FCSTD DOCUMENT  (FreeCAD 0.20R29410 (Git))
Label: trafficModuleV3
License: All rights reserved
LicenseURL: http://en.wikipedia.org/wiki/All_rights_reserved
objects: Part::Feature×121, Sketcher::SketchObject×63, Part::Extrusion×29, Part::Cylinder×26, Part::MultiFuse×25, Part::MultiCommon×20, Part::Loft×17, App::Part×13, Part::Cut×12, Part::Box×7, Part::Cone×1, Part::Compound×1
note: 322 computed .brp shape members not serialized (recipe doc carries the construction recipe); baked Part::Feature solids carry a one-line shape summary decoded from their .brp

FEATURE [Sketcher::SketchObject] Sketch014
  FullyConstrained = true
  sketch-geometry (4):
    g0: LineSegment StartX=0 StartY=275 StartZ=0 EndX=275 EndY=275 EndZ=0
    g1: LineSegment StartX=275 StartY=275 StartZ=0 EndX=275 EndY=0 EndZ=0
    g2: LineSegment StartX=275 StartY=0 StartZ=0 EndX=0 EndY=0 EndZ=0
    g3: LineSegment StartX=0 StartY=0 StartZ=0 EndX=0 EndY=275 EndZ=0
  constraints (11):
    c: Coincident(g0,g1)
    c: Coincident(g1,g2)
    c: Coincident(g2,g3)
    c: Coincident(g3,g0)
    c: Horizontal(g0)
    c: Horizontal(g2)
    c: Vertical(g1)
    c: Vertical(g3)
    c: Coincident(g2,g-1)
    c: DistanceX(g2,g2) = 275
    c: DistanceY(g3,g3) = 275
FEATURE [Sketcher::SketchObject] Sketch015
  FullyConstrained = true
  Placement = pos=(0,0,175.1) rot=(0,0,1;0rad)
  sketch-geometry (5):
    g0: GeomPoint X=137.5 Y=137.5 Z=0
    g1: LineSegment StartX=137.55 StartY=137.55 StartZ=0 EndX=137.55 EndY=137.45 EndZ=0
    g2: LineSegment StartX=137.55 StartY=137.45 StartZ=0 EndX=137.45 EndY=137.45 EndZ=0
    g3: LineSegment StartX=137.45 StartY=137.45 StartZ=0 EndX=137.45 EndY=137.55 EndZ=0
    g4: LineSegment StartX=137.45 StartY=137.55 StartZ=0 EndX=137.55 EndY=137.55 EndZ=0
  constraints (14):
    c: Coincident(g1,g2)
    c: Horizontal(g2)
    c: Vertical(g1)
    c: DistanceX(g2,g2) = 0.1
    c: DistanceX(g2,g0) = 0.05
    c: DistanceY(g1,g1) = 0.1
    c: DistanceY(g1,g0) = -0.05
    c: DistanceX(g0) = 137.5
    c: DistanceY(g0) = 137.5
    c: Coincident(g3,g2)
    c: Vertical(g3)
    c: Coincident(g4,g3)
    c: Coincident(g4,g1)
    c: Horizontal(g4)
FEATURE [Part::Loft] Loft  label="outerLayer"
  Closed = false
  MaxDegree = 5
  Ruled = false
  Sections = -> [Sketch014,Sketch015]
  Solid = true
FEATURE [Part::Feature] Part__Feature025  label="CUI_VGS-35C-12"
  Placement = pos=(86,137.5,21.5) rot=(1,0,0;1.5708rad)
  shape: bbox 82.03 x 100 x 30.06 mm, 2215 faces, 10 solids (baked)
FEATURE [Part::Cylinder] Cylinder004 .. Cylinder009  x6 (patterned run collapsed; names and placements below)
  Angle = 360
  AttacherType = Attacher::AttachEngine3D
  FirstAngle = 0
  Height = 10
  Radius = 2
  SecondAngle = 0
FEATURE [Part::Cylinder] Cylinder010  label="Cylinder"
  Angle = 360
  AttacherType = Attacher::AttachEngine3D
  FirstAngle = 0
  Height = 10
  Radius = 2
  SecondAngle = 0
FEATURE [Part::Cylinder] Cylinder011 .. Cylinder018  x8 (patterned run collapsed; names and placements below)
  Angle = 360
  AttacherType = Attacher::AttachEngine3D
  FirstAngle = 0
  Height = 10
  Radius = 2
  SecondAngle = 0
FEATURE [Part::Feature] Part__Feature  label="MainBoard"
  shape: bbox 50 x 23 x 1.8 mm, 90 faces (baked)
FEATURE [Part::Feature] Part__Feature029  label="USB Type C Port (SMD Type)"
  Placement = pos=(-18.7,0.12,3.4) rot=(0.707107,-0.707107,0;3.14159rad)
  shape: bbox 7.901 x 8.941 x 4.201 mm, 394 faces, 24 solids (baked)
FEATURE [Part::Feature] Part__Feature030  label="LoRaSTM32Chip"
  Placement = pos=(8.97,0,1.8) rot=(0,0,1;0rad)
  shape: bbox 12 x 12 x 2.5 mm, 68 faces (baked)
FEATURE [Part::Feature] Part__Feature031  label="E10_433M_SMA122"
  Placement = pos=(13,-2.15,1.4) rot=(0,0,1;0rad)
  shape: bbox 11.33 x 1.55 x 1.55 mm, 34 faces (baked)
FEATURE [Part::Feature] Part__Feature032  label="E10_433M_SMA123"
  Placement = pos=(13,-2.15,1.4) rot=(0,0,1;0rad)
  shape: bbox 13.33 x 6.493 x 6.493 mm, 59 faces (baked)
FEATURE [Part::Feature] Part__Feature033  label="CP2012"
  Placement = pos=(-8.75,0.13,1.82) rot=(0,0,1;0rad)
  shape: bbox 4 x 4 x 0.7 mm, 6 faces (baked)
FEATURE [Part::Feature] Part__Feature034  label="u.Fl Antenna Connector - 523-A-1JB"
  Placement = pos=(24.2,5.8,1.8) rot=(0,0.707107,0.707107;3.14159rad)
  shape: bbox 3.1 x 3 x 1.25 mm, 82 faces, 5 solids (baked)
FEATURE [Part::Feature] Part__Feature035  label="Top Traces"
  shape: bbox 49.4 x 23 x 0.02 mm, 7906 faces, 207 solids (baked)
FEATURE [App::Part] LoRa_E5_Mini  label="LoRa-E5-Mini"
  Group = -> [Part__Feature,Part__Feature029,Part__Feature030,Part__Feature031,Part__Feature032,Part__Feature033,Part__Feature034,Part__Feature035,Cylinder004,Cylinder005,Cylinder006,Cylinder007,Cylinder008,Cylinder009,Cylinder010,Cylinder011,Cylinder012,Cylinder013,Cylinder014,Cylinder015,Cylinder016,Cylinder017,Cylinder018]
  Origin = -> Origin
  Placement = pos=(100,164,45) rot=(0,0,-1;4.71239rad)
FEATURE [Part::Feature] Part__Feature037  label="ips7100s"
  Placement = pos=(161.5,115,75) rot=(0,0,1;0rad)
  shape: bbox 48.08 x 13.98 x 44.07 mm, 1935 faces (baked)
FEATURE [Part::Feature] Part__Feature007  label="Heat Sink"
  shape: bbox 100 x 91 x 19 mm, 161 faces (baked)
FEATURE [Part::Feature] Part__Feature008  label="Battery Holder"
  shape: bbox 28.5 x 16 x 6 mm, 91 faces (baked)
FEATURE [Part::Feature] Part__Feature009  label="DC Jack"
  shape: bbox 7.6 x 11.5 x 9.75 mm, 10 faces (baked)
FEATURE [Part::Feature] Part__Feature010  label="PCB"
  shape: bbox 90 x 90 x 3.3 mm, 59 faces (baked)
FEATURE [Part::Feature] Part__Feature011  label="HDMI"
  shape: bbox 14.51 x 11.61 x 5.506 mm, 31 faces (baked)
FEATURE [Part::Feature] Part__Feature012  label="Ethernet"
  shape: bbox 15.9 x 21.4 x 13.5 mm, 25 faces (baked)
FEATURE [Part::Feature] Part__Feature013  label="USB 3.0 B"
  shape: bbox 14.55 x 17.5 x 16.15 mm, 36 faces (baked)
FEATURE [Part::Feature] Part__Feature014  label="USB 3.0 A"
  shape: bbox 14.55 x 17.5 x 16.15 mm, 36 faces (baked)
FEATURE [Part::Feature] Part__Feature015  label="Audio Jack"
  shape: bbox 6.5 x 14 x 4 mm, 10 faces (baked)
FEATURE [Part::Feature] Part__Feature016  label="Fan Plug"
  shape: bbox 3.75 x 7.5 x 4.75 mm, 32 faces (baked)
FEATURE [Part::Feature] Part__Feature017  label="REMOCON"
  shape: bbox 7.006 x 5.006 x 12.01 mm, 30 faces (baked)
FEATURE [Part::Feature] Part__Feature018  label="eMMC"
  shape: bbox 13.5 x 18.5 x 2.8 mm, 33 faces (baked)
FEATURE [Part::Feature] Part__Feature019  label="MicroUSB"
  shape: bbox 7.012 x 4.616 x 3.511 mm, 31 faces (baked)
FEATURE [Part::Feature] Part__Feature020  label="Switch"
  shape: bbox 9 x 5.74 x 3.5 mm, 11 faces (baked)
FEATURE [Part::Feature] Part__Feature021  label="MicroSD Card Socket"
  shape: bbox 11.5 x 5.5 x 3.5 mm, 11 faces (baked)
FEATURE [Part::Feature] Part__Feature022  label="7 Pin Header"
  shape: bbox 17.5 x 2.5 x 8 mm, 41 faces (baked)
FEATURE [Part::Feature] Part__Feature023  label="UART"
  shape: bbox 5 x 12.5 x 6 mm, 43 faces (baked)
FEATURE [Part::Feature] Part__Feature024  label="40 Pin Header"
  shape: bbox 5 x 50 x 8 mm, 206 faces (baked)
FEATURE [App::Part] Odroid_N2__v4  label="Odroid-N2+ v4"
  Group = -> [Part__Feature007,Part__Feature008,Part__Feature009,Part__Feature010,Part__Feature011,Part__Feature012,Part__Feature013,Part__Feature014,Part__Feature015,Part__Feature016,Part__Feature017,Part__Feature018,Part__Feature019,Part__Feature020,Part__Feature021,Part__Feature022,Part__Feature023,Part__Feature024]
  Origin = -> Origin002
  Placement = pos=(164,-676,-21.5) rot=(0,0,1;0rad)
FEATURE [Part::Cone] Cone
  Angle = 360
  AttacherType = Attacher::AttachEngine3D
  Height = 1.5
  Placement = pos=(0,0,25.5) rot=(0,0,1;0rad)
  Radius1 = 4
  Radius2 = 3.5
FEATURE [Part::Cylinder] Cylinder020
  Angle = 360
  AttacherType = Attacher::AttachEngine3D
  FirstAngle = 0
  Height = 22
  Placement = pos=(0,0,5) rot=(0,0,1;0rad)
  Radius = 3.2
  SecondAngle = 0
FEATURE [Part::Cylinder] Cylinder021
  Angle = 360
  AttacherType = Attacher::AttachEngine3D
  FirstAngle = 0
  Height = 2
  Placement = pos=(0,0,5) rot=(0,0,1;0rad)
  Radius = 3.55
  SecondAngle = 0
FEATURE [Part::Cylinder] Cylinder022
  Angle = 360
  AttacherType = Attacher::AttachEngine3D
  FirstAngle = 0
  Height = 1
  Placement = pos=(0,0,11) rot=(0,0,1;0rad)
  Radius = 3.55
  SecondAngle = 0
FEATURE [Part::Cylinder] Cylinder023
  Angle = 360
  AttacherType = Attacher::AttachEngine3D
  FirstAngle = 0
  Height = 8
  Placement = pos=(0,0,12) rot=(0,0,1;0rad)
  Radius = 3.25
  SecondAngle = 0
FEATURE [Part::Cylinder] Cylinder024
  Angle = 360
  AttacherType = Attacher::AttachEngine3D
  FirstAngle = 0
  Height = 5.5
  Placement = pos=(0,0,20) rot=(0,0,1;0rad)
  Radius = 4
  SecondAngle = 0
FEATURE [Part::Cylinder] Cylinder025
  Angle = 360
  AttacherType = Attacher::AttachEngine3D
  FirstAngle = 0
  Height = 2
  Placement = pos=(0,0,3) rot=(0,0,1;0rad)
  Radius = 1
  SecondAngle = 0
FEATURE [Part::MultiFuse] Fusion002
  Shapes = -> [Cone,Cylinder020,Cylinder021,Cylinder022,Cylinder023,Cylinder024]
FEATURE [Part::MultiFuse] Fusion055  label="mic"
  Placement = pos=(137.5,137.5,108.25) rot=(0,0,1;3.14159rad)
  Shapes = -> [Cylinder025,Fusion002]
FEATURE [Part::Feature] Part__Feature040  label="CeramicBody (1)"
  shape: bbox 1.8 x 1.23 x 1.23 mm, 10 faces (baked)
FEATURE [Part::Feature] Part__Feature126  label="scd30"
  Placement = pos=(137.5,170,95) rot=(1,0,0;3.14159rad)
  shape: bbox 35.11 x 7.027 x 23.02 mm, 2292 faces, 25 solids (baked)
FEATURE [Part::Feature] Part__Feature127  label="Board"
  shape: bbox 25.4 x 25.4 x 1.57 mm, 211 faces (baked)
FEATURE [Part::Feature] Part__Feature128  label="QFN24_4MM"
  Placement = pos=(12.1412,14.4526,1.57) rot=(0,0,1;3.92699rad)
  shape: bbox 5.657 x 5.657 x 0.9 mm, 172 faces (baked)
FEATURE [Part::Feature] Part__Feature129  label="Part 5"
  shape: bbox 0.48 x 0.6603 x 0.6 mm, 14 faces (baked)
FEATURE [Part::Feature] Part__Feature130  label="Part 6"
  shape: bbox 0.48 x 0.6603 x 0.6 mm, 14 faces (baked)
FEATURE [Part::Feature] Part__Feature131  label="Part 4"
  shape: bbox 0.48 x 0.6603 x 0.6 mm, 14 faces (baked)
FEATURE [Part::Feature] Part__Feature132  label="Part 3"
  shape: bbox 0.48 x 0.6603 x 0.6 mm, 14 faces (baked)
FEATURE [Part::Feature] Part__Feature133  label="Part 010"
  shape: bbox 0.48 x 0.6603 x 0.6 mm, 14 faces (baked)
FEATURE [Part::Feature] Part__Feature134  label="Part 011"
  shape: bbox 3 x 1.4 x 1 mm, 10 faces (baked)
FEATURE [Part::Feature] Part__Feature135  label="Pin1"
  shape: bbox 0.6224 x 1.252 x 1.252 mm, 37 faces (baked)
FEATURE [Part::Feature] Part__Feature136  label="Pin2"
  shape: bbox 0.6224 x 1.252 x 1.252 mm, 37 faces (baked)
FEATURE [Part::Feature] Part__Feature137  label="CeramicBody"
  shape: bbox 1.8 x 1.23 x 1.23 mm, 10 faces (baked)
FEATURE [Part::Feature] Part__Feature138  label="0603-NO (1)"
  Placement = pos=(23.241,6.223,1.57) rot=(0,0,1;0rad)
  shape: bbox 1.7 x 0.9 x 0.55 mm, 52 faces, 3 solids (baked)
FEATURE [Part::Feature] Part__Feature139  label="0603-NO (2)"
  Placement = pos=(13.3858,8.4328,1.57) rot=(0,0,1;0rad)
  shape: bbox 1.7 x 0.9 x 0.55 mm, 52 faces, 3 solids (baked)
FEATURE [Part::Feature] Part__Feature140  label="0603-NO (3)"
  Placement = pos=(1.905,18.923,1.57) rot=(0,0,1;3.14159rad)
  shape: bbox 1.7 x 0.9 x 0.55 mm, 52 faces, 3 solids (baked)
FEATURE [Part::Feature] Part__Feature141  label="Pin1 (1)"
  shape: bbox 0.6224 x 1.252 x 1.252 mm, 37 faces (baked)
FEATURE [Part::Feature] Part__Feature142  label="Pin2 (1)"
  shape: bbox 0.6224 x 1.252 x 1.252 mm, 37 faces (baked)
FEATURE [Part::Feature] Part__Feature143  label="Pin1 (2)"
  shape: bbox 0.6224 x 1.252 x 1.252 mm, 37 faces (baked)
FEATURE [Part::Feature] Part__Feature144  label="Pin2 (2)"
  shape: bbox 0.6224 x 1.252 x 1.252 mm, 37 faces (baked)
FEATURE [Part::Feature] Part__Feature145  label="CeramicBody (2)"
  shape: bbox 1.8 x 1.23 x 1.23 mm, 10 faces (baked)
FEATURE [Part::Feature] Part__Feature146  label="CHIPLED_0603_NOOUTLINE"
  Placement = pos=(23.368,8.509,1.57) rot=(0,0,1;1.5708rad)
  shape: bbox 1.616 x 0.8 x 0.4 mm, 133 faces (baked)
FEATURE [Part::Feature] Part__Feature147  label="CHIPLED_0603_NOOUTLINE (1)"
  Placement = pos=(1.905,16.764,1.57) rot=(0,0,-1;1.5708rad)
  shape: bbox 1.616 x 0.8 x 0.4 mm, 133 faces (baked)
FEATURE [Part::Feature] Part__Feature148  label="JST_SH4"
  Placement = pos=(22.86,12.7,1.57) rot=(0,0,1;1.5708rad)
  shape: bbox 4.95 x 6 x 2.96 mm, 229 faces, 7 solids (baked)
FEATURE [Part::Feature] Part__Feature149  label="JST_SH4 (1)"
  Placement = pos=(2.54,12.7,1.57) rot=(0,0,-1;1.5708rad)
  shape: bbox 4.95 x 6 x 2.96 mm, 229 faces, 7 solids (baked)
FEATURE [Part::Feature] Part__Feature150  label="NEO3535_REVERSE"
  Placement = pos=(12.7,23.114,0) rot=(0,1,0;3.14159rad)
  shape: bbox 5.88 x 2.8 x 1.78 mm, 41 faces, 5 solids (baked)
FEATURE [Part::Feature] Part__Feature151  label="RESPACK_4X0603"
  Placement = pos=(22.86,18.415,1.57) rot=(0,0,1;3.14159rad)
  shape: bbox 3.2 x 1.6 x 0.61 mm, 172 faces (baked)
FEATURE [Part::Feature] Part__Feature152  label="SOT363"
  Placement = pos=(17.399,12.192,1.57) rot=(0,0,-1;1.5708rad)
  shape: bbox 2.208 x 2.208 x 1.121 mm, 178 faces, 4 solids (baked)
FEATURE [Part::Feature] Part__Feature153  label="Printed Circuit Board001"
  shape: bbox 25.4 x 17.78 x 1.6 mm, 42 faces (baked)
FEATURE [Part::Feature] Part__Feature154  label="EAHC2835WD007"
  shape: bbox 3.513 x 2.813 x 0.7485 mm, 108 faces, 4 solids (baked)
FEATURE [Part::Feature] Part__Feature155  label="AS7341 v003"
  Placement = pos=(0,-0.339822,1.6) rot=(0,0,1;0rad)
  shape: bbox 2 x 3.1 x 1.1 mm, 267 faces, 26 solids (baked)
FEATURE [Part::Feature] Part__Feature156  label="CAPC-0805-T0.95-BN v004"
  Placement = pos=(-5.01759,-3.15294,1.6) rot=(0,0,1;0rad)
  shape: bbox 2.1 x 1.35 x 0.95 mm, 42 faces (baked)
FEATURE [Part::Feature] Part__Feature157  label="CAPC-0805-T0.95-BN v005"
  Placement = pos=(-5.48627,2.66154,1.6) rot=(0,0,-1;1.5708rad)
  shape: bbox 1.35 x 2.1 x 0.95 mm, 42 faces (baked)
FEATURE [Part::Feature] Part__Feature158  label="CAPC-0805-T0.95-BN v006"
  Placement = pos=(-3.43627,2.66154,1.6) rot=(0,0,-1;1.5708rad)
  shape: bbox 1.35 x 2.1 x 0.95 mm, 42 faces (baked)
FEATURE [Part::Feature] Part__Feature159  label="CAPC-0603-T0.9-BN v002"
  Placement = pos=(-1.69987,-3.28475,1.6) rot=(0,0,1;0rad)
  shape: bbox 1.7 x 0.9 x 0.9 mm, 42 faces (baked)
FEATURE [Part::Feature] Part__Feature160  label="BODY_MF06A001"
  Placement = pos=(0,0,0.762) rot=(0.57735,-0.57735,-0.57735;2.0944rad)
  shape: bbox 1.601 x 2.921 x 1.016 mm, 42 faces (baked)
FEATURE [Part::Feature] Part__Feature161  label="LEAD_MF06A006"
  Placement = pos=(-0.9652,-0.9525,0.1016) rot=(0.57735,-0.57735,-0.57735;2.0944rad)
  shape: bbox 0.6223 x 0.3749 x 0.8636 mm, 14 faces (baked)
FEATURE [Part::Feature] Part__Feature162  label="LEAD_MF06A007"
  Placement = pos=(-0.9652,0,0.1016) rot=(0.57735,-0.57735,-0.57735;2.0944rad)
  shape: bbox 0.6223 x 0.3749 x 0.8636 mm, 14 faces (baked)
FEATURE [Part::Feature] Part__Feature163  label="LEAD_MF06A008"
  Placement = pos=(-0.9652,0.9525,0.1016) rot=(0.57735,-0.57735,-0.57735;2.0944rad)
  shape: bbox 0.6223 x 0.3749 x 0.8636 mm, 14 faces (baked)
FEATURE [Part::Feature] Part__Feature164  label="LEAD_MF06A009"
  Placement = pos=(0.9652,-0.9525,0.1016) rot=(0.57735,0.57735,0.57735;2.0944rad)
  shape: bbox 0.6223 x 0.3749 x 0.8636 mm, 14 faces (baked)
FEATURE [Part::Feature] Part__Feature165  label="LEAD_MF06A010"
  Placement = pos=(0.9652,0,0.1016) rot=(0.57735,0.57735,0.57735;2.0944rad)
  shape: bbox 0.6223 x 0.3749 x 0.8636 mm, 14 faces (baked)
FEATURE [Part::Feature] Part__Feature166  label="LEAD_MF06A011"
  Placement = pos=(0.9652,0.9525,0.1016) rot=(0.57735,0.57735,0.57735;2.0944rad)
  shape: bbox 0.6223 x 0.3749 x 0.8636 mm, 14 faces (baked)
FEATURE [Part::Feature] Part__Feature167  label="SOT363 v003"
  Placement = pos=(4.97054,-0.645171,1.675) rot=(0,0,1;3.14159rad)
  shape: bbox 2.1 x 2 x 1.1 mm, 94 faces, 7 solids (baked)
FEATURE [Part::Feature] Part__Feature168  label="LED 0603 single color v002"
  Placement = pos=(-9.18406,3.72778,1.60762) rot=(0,0,1;1.5708rad)
  shape: bbox 1.961 x 0.7932 x 0.7145 mm, 63 faces, 5 solids (baked)
FEATURE [Part::Feature] Part__Feature169  label="RESC-0603 v003"
  Placement = pos=(4.83432,-3.67461,1.6) rot=(0,0,1;0rad)
  shape: bbox 1.7 x 0.9 x 0.55 mm, 52 faces, 3 solids (baked)
FEATURE [Part::Feature] Part__Feature170  label="RESC-0603 v004"
  Placement = pos=(-7.14949,3.61248,1.6) rot=(0,0,-1;1.5708rad)
  shape: bbox 0.9 x 1.7 x 0.55 mm, 52 faces, 3 solids (baked)
FEATURE [Part::Feature] Part__Feature171  label="YC164_RESPACK v002"
  Placement = pos=(2.99591,1.52916,1.6) rot=(0,0,1;0rad)
  shape: bbox 3.2 x 1.6 x 0.61 mm, 172 faces (baked)
FEATURE [Part::Feature] Part__Feature172  label="qwicc v004"
  Placement = pos=(-10.8364,0.0607456,1.65) rot=(0,0,-1;1.5708rad)
  shape: bbox 4.95 x 6 x 2.96 mm, 229 faces, 7 solids (baked)
FEATURE [Part::Feature] Part__Feature173  label="qwicc v005"
  Placement = pos=(10.8256,0.00556102,1.65) rot=(0,0,1;1.5708rad)
  shape: bbox 4.95 x 6 x 2.96 mm, 229 faces, 7 solids (baked)
FEATURE [App::Part] _603_NO  label="0603-NO"
  Group = -> [Part__Feature135,Part__Feature136,Part__Feature137]
  Origin = -> Origin012
  Placement = pos=(16.51,8.382,1.57) rot=(0,0,1;0rad)
FEATURE [App::Part] _6700497  label="36700497"
  Group = -> [Part__Feature129,Part__Feature130,Part__Feature131,Part__Feature132,Part__Feature133,Part__Feature134]
  Origin = -> Origin010
  Placement = pos=(0,0,0) rot=(0,0,1;3.14159rad)
FEATURE [App::Part] SOT23_5  label="SOT23-5"
  Group = -> [_6700497]
  Origin = -> Origin011
  Placement = pos=(2.54,6.985,1.57) rot=(0,0,1;3.14159rad)
FEATURE [App::Part] _805_NO  label="0805-NO"
  Group = -> [Part__Feature141,Part__Feature142,Part__Feature040]
  Origin = -> Origin013
  Placement = pos=(7.874,13.589,1.57) rot=(0,0,1;1.5708rad)
FEATURE [App::Part] _805_NO__1_  label="0805-NO (1)"
  Group = -> [Part__Feature143,Part__Feature144,Part__Feature145]
  Origin = -> Origin014
  Placement = pos=(12.827,6.223,1.57) rot=(0,0,1;3.14159rad)
FEATURE [App::Part] Packages
  Group = -> [Part__Feature128,SOT23_5,_603_NO,Part__Feature138,Part__Feature139,Part__Feature140,_805_NO,_805_NO__1_,Part__Feature146,Part__Feature147,Part__Feature148,Part__Feature149,Part__Feature150,Part__Feature151,Part__Feature152]
  Origin = -> Origin015
FEATURE [App::Part] Adafruit_I2C_QT_Rotary_Encoder_v2  label="gps"
  Group = -> [Part__Feature127,Packages]
  Origin = -> Origin016
  Placement = pos=(167.5,167.5,74) rot=(0,0,1;0rad)
FEATURE [App::Part] sot_23_6_v003  label="sot-23-6 v003"
  Group = -> [Part__Feature160,Part__Feature161,Part__Feature162,Part__Feature163,Part__Feature164,Part__Feature165,Part__Feature166]
  Origin = -> Origin017
  Placement = pos=(-4.47945,-0.603742,1.69152) rot=(0,0,1;0rad)
FEATURE [App::Part] Adafruit_AS7341_STEMMA_QT_v003  label="bme280"
  Group = -> [Part__Feature153,Part__Feature154,Part__Feature155,Part__Feature156,Part__Feature157,Part__Feature158,Part__Feature159,sot_23_6_v003,Part__Feature167,Part__Feature168,Part__Feature169,Part__Feature170,Part__Feature171,Part__Feature172,Part__Feature173]
  Origin = -> Origin018
  Placement = pos=(170.5,137.5,95) rot=(-0.707107,0,-0.707107;3.14159rad)
FEATURE [Part::Feature] Part__Feature174  label="Printed Circuit Board002"
  shape: bbox 25.4 x 17.78 x 1.6 mm, 42 faces (baked)
FEATURE [Part::Feature] Part__Feature175  label="EAHC2835WD008"
  shape: bbox 3.513 x 2.813 x 0.7485 mm, 108 faces, 4 solids (baked)
FEATURE [Part::Feature] Part__Feature176  label="AS7341 v004"
  Placement = pos=(0,-0.339822,1.6) rot=(0,0,1;0rad)
  shape: bbox 2 x 3.1 x 1.1 mm, 267 faces, 26 solids (baked)
FEATURE [Part::Feature] Part__Feature177  label="CAPC-0805-T0.95-BN v007"
  Placement = pos=(-5.01759,-3.15294,1.6) rot=(0,0,1;0rad)
  shape: bbox 2.1 x 1.35 x 0.95 mm, 42 faces (baked)
FEATURE [Part::Feature] Part__Feature178  label="CAPC-0805-T0.95-BN v008"
  Placement = pos=(-5.48627,2.66154,1.6) rot=(0,0,-1;1.5708rad)
  shape: bbox 1.35 x 2.1 x 0.95 mm, 42 faces (baked)
FEATURE [Part::Feature] Part__Feature179  label="CAPC-0805-T0.95-BN v009"
  Placement = pos=(-3.43627,2.66154,1.6) rot=(0,0,-1;1.5708rad)
  shape: bbox 1.35 x 2.1 x 0.95 mm, 42 faces (baked)
FEATURE [Part::Feature] Part__Feature180  label="CAPC-0603-T0.9-BN v003"
  Placement = pos=(-1.69987,-3.28475,1.6) rot=(0,0,1;0rad)
  shape: bbox 1.7 x 0.9 x 0.9 mm, 42 faces (baked)
FEATURE [Part::Feature] Part__Feature181  label="BODY_MF06A002"
  Placement = pos=(0,0,0.762) rot=(0.57735,-0.57735,-0.57735;2.0944rad)
  shape: bbox 1.601 x 2.921 x 1.016 mm, 42 faces (baked)
FEATURE [Part::Feature] Part__Feature182  label="LEAD_MF06A012"
  Placement = pos=(-0.9652,-0.9525,0.1016) rot=(0.57735,-0.57735,-0.57735;2.0944rad)
  shape: bbox 0.6223 x 0.3749 x 0.8636 mm, 14 faces (baked)
FEATURE [Part::Feature] Part__Feature183  label="LEAD_MF06A013"
  Placement = pos=(-0.9652,0,0.1016) rot=(0.57735,-0.57735,-0.57735;2.0944rad)
  shape: bbox 0.6223 x 0.3749 x 0.8636 mm, 14 faces (baked)
FEATURE [Part::Feature] Part__Feature184  label="LEAD_MF06A014"
  Placement = pos=(-0.9652,0.9525,0.1016) rot=(0.57735,-0.57735,-0.57735;2.0944rad)
  shape: bbox 0.6223 x 0.3749 x 0.8636 mm, 14 faces (baked)
FEATURE [Part::Feature] Part__Feature185  label="LEAD_MF06A015"
  Placement = pos=(0.9652,-0.9525,0.1016) rot=(0.57735,0.57735,0.57735;2.0944rad)
  shape: bbox 0.6223 x 0.3749 x 0.8636 mm, 14 faces (baked)
FEATURE [Part::Feature] Part__Feature186  label="LEAD_MF06A016"
  Placement = pos=(0.9652,0,0.1016) rot=(0.57735,0.57735,0.57735;2.0944rad)
  shape: bbox 0.6223 x 0.3749 x 0.8636 mm, 14 faces (baked)
FEATURE [Part::Feature] Part__Feature187  label="LEAD_MF06A017"
  Placement = pos=(0.9652,0.9525,0.1016) rot=(0.57735,0.57735,0.57735;2.0944rad)
  shape: bbox 0.6223 x 0.3749 x 0.8636 mm, 14 faces (baked)
FEATURE [Part::Feature] Part__Feature188  label="SOT363 v004"
  Placement = pos=(4.97054,-0.645171,1.675) rot=(0,0,1;3.14159rad)
  shape: bbox 2.1 x 2 x 1.1 mm, 94 faces, 7 solids (baked)
FEATURE [Part::Feature] Part__Feature189  label="LED 0603 single color v003"
  Placement = pos=(-9.18406,3.72778,1.60762) rot=(0,0,1;1.5708rad)
  shape: bbox 1.961 x 0.7932 x 0.7145 mm, 63 faces, 5 solids (baked)
FEATURE [Part::Feature] Part__Feature190  label="RESC-0603 v005"
  Placement = pos=(4.83432,-3.67461,1.6) rot=(0,0,1;0rad)
  shape: bbox 1.7 x 0.9 x 0.55 mm, 52 faces, 3 solids (baked)
FEATURE [Part::Feature] Part__Feature191  label="RESC-0603 v006"
  Placement = pos=(-7.14949,3.61248,1.6) rot=(0,0,-1;1.5708rad)
  shape: bbox 0.9 x 1.7 x 0.55 mm, 52 faces, 3 solids (baked)
FEATURE [Part::Feature] Part__Feature192  label="YC164_RESPACK v003"
  Placement = pos=(2.99591,1.52916,1.6) rot=(0,0,1;0rad)
  shape: bbox 3.2 x 1.6 x 0.61 mm, 172 faces (baked)
FEATURE [Part::Feature] Part__Feature193  label="qwicc v006"
  Placement = pos=(-10.8364,0.0607456,1.65) rot=(0,0,-1;1.5708rad)
  shape: bbox 4.95 x 6 x 2.96 mm, 229 faces, 7 solids (baked)
FEATURE [Part::Feature] Part__Feature194  label="qwicc v007"
  Placement = pos=(10.8256,0.00556102,1.65) rot=(0,0,1;1.5708rad)
  shape: bbox 4.95 x 6 x 2.96 mm, 229 faces, 7 solids (baked)
FEATURE [App::Part] sot_23_6_v004  label="sot-23-6 v004"
  Group = -> [Part__Feature181,Part__Feature182,Part__Feature183,Part__Feature184,Part__Feature185,Part__Feature186,Part__Feature187]
  Origin = -> Origin019
  Placement = pos=(-4.47945,-0.603742,1.69152) rot=(0,0,1;0rad)
FEATURE [App::Part] Adafruit_AS7341_STEMMA_QT_v004  label="bme281"
  Group = -> [Part__Feature174,Part__Feature175,Part__Feature176,Part__Feature177,Part__Feature178,Part__Feature179,Part__Feature180,sot_23_6_v004,Part__Feature188,Part__Feature189,Part__Feature190,Part__Feature191,Part__Feature192,Part__Feature193,Part__Feature194]
  Origin = -> Origin020
  Placement = pos=(104.5,137.5,95) rot=(0,1,0;4.71239rad)
FEATURE [Sketcher::SketchObject] Sketch016
  FullyConstrained = true
  sketch-geometry (4):
    g0: LineSegment StartX=0 StartY=275 StartZ=0 EndX=275 EndY=275 EndZ=0
    g1: LineSegment StartX=275 StartY=275 StartZ=0 EndX=275 EndY=0 EndZ=0
    g2: LineSegment StartX=275 StartY=0 StartZ=0 EndX=0 EndY=0 EndZ=0
    g3: LineSegment StartX=0 StartY=0 StartZ=0 EndX=0 EndY=275 EndZ=0
  constraints (11):
    c: Coincident(g0,g1)
    c: Coincident(g1,g2)
    c: Coincident(g2,g3)
    c: Coincident(g3,g0)
    c: Horizontal(g0)
    c: Horizontal(g2)
    c: Vertical(g1)
    c: Vertical(g3)
    c: Coincident(g2,g-1)
    c: DistanceX(g2,g2) = 275
    c: DistanceY(g3,g3) = 275
FEATURE [Sketcher::SketchObject] Sketch017
  FullyConstrained = true
  Placement = pos=(0,0,175.1) rot=(0,0,1;0rad)
  sketch-geometry (5):
    g0: GeomPoint X=137.5 Y=137.5 Z=0
    g1: LineSegment StartX=137.55 StartY=137.55 StartZ=0 EndX=137.55 EndY=137.45 EndZ=0
    g2: LineSegment StartX=137.55 StartY=137.45 StartZ=0 EndX=137.45 EndY=137.45 EndZ=0
    g3: LineSegment StartX=137.45 StartY=137.45 StartZ=0 EndX=137.45 EndY=137.55 EndZ=0
    g4: LineSegment StartX=137.45 StartY=137.55 StartZ=0 EndX=137.55 EndY=137.55 EndZ=0
  constraints (14):
    c: Coincident(g1,g2)
    c: Horizontal(g2)
    c: Vertical(g1)
    c: DistanceX(g2,g2) = 0.1
    c: DistanceX(g2,g0) = 0.05
    c: DistanceY(g1,g1) = 0.1
    c: DistanceY(g1,g0) = -0.05
    c: DistanceX(g0) = 137.5
    c: DistanceY(g0) = 137.5
    c: Coincident(g3,g2)
    c: Vertical(g3)
    c: Coincident(g4,g3)
    c: Coincident(g4,g1)
    c: Horizontal(g4)
FEATURE [Part::Loft] Loft001  label="outerLayer001"
  Closed = false
  MaxDegree = 5
  Ruled = false
  Sections = -> [Sketch016,Sketch017]
  Solid = true
FEATURE [Sketcher::SketchObject] Sketch018
  FullyConstrained = true
  sketch-geometry (4):
    g0: LineSegment StartX=0 StartY=275 StartZ=0 EndX=275 EndY=275 EndZ=0
    g1: LineSegment StartX=275 StartY=275 StartZ=0 EndX=275 EndY=0 EndZ=0
    g2: LineSegment StartX=275 StartY=0 StartZ=0 EndX=0 EndY=0 EndZ=0
    g3: LineSegment StartX=0 StartY=0 StartZ=0 EndX=0 EndY=275 EndZ=0
  constraints (11):
    c: Coincident(g0,g1)
    c: Coincident(g1,g2)
    c: Coincident(g2,g3)
    c: Coincident(g3,g0)
    c: Horizontal(g0)
    c: Horizontal(g2)
    c: Vertical(g1)
    c: Vertical(g3)
    c: Coincident(g2,g-1)
    c: DistanceX(g2,g2) = 275
    c: DistanceY(g3,g3) = 275
FEATURE [Sketcher::SketchObject] Sketch019
  FullyConstrained = true
  Placement = pos=(0,0,175.1) rot=(0,0,1;0rad)
  sketch-geometry (5):
    g0: GeomPoint X=137.5 Y=137.5 Z=0
    g1: LineSegment StartX=137.55 StartY=137.55 StartZ=0 EndX=137.55 EndY=137.45 EndZ=0
    g2: LineSegment StartX=137.55 StartY=137.45 StartZ=0 EndX=137.45 EndY=137.45 EndZ=0
    g3: LineSegment StartX=137.45 StartY=137.45 StartZ=0 EndX=137.45 EndY=137.55 EndZ=0
    g4: LineSegment StartX=137.45 StartY=137.55 StartZ=0 EndX=137.55 EndY=137.55 EndZ=0
  constraints (14):
    c: Coincident(g1,g2)
    c: Horizontal(g2)
    c: Vertical(g1)
    c: DistanceX(g2,g2) = 0.1
    c: DistanceX(g2,g0) = 0.05
    c: DistanceY(g1,g1) = 0.1
    c: DistanceY(g1,g0) = -0.05
    c: DistanceX(g0) = 137.5
    c: DistanceY(g0) = 137.5
    c: Coincident(g3,g2)
    c: Vertical(g3)
    c: Coincident(g4,g3)
    c: Coincident(g4,g1)
    c: Horizontal(g4)
FEATURE [Part::Loft] Loft002  label="outerLayer002"
  Closed = false
  MaxDegree = 5
  Placement = pos=(0,0,-8) rot=(0,0,1;0rad)
  Ruled = false
  Sections = -> [Sketch018,Sketch019]
  Solid = true
FEATURE [Part::Cut] Cut  label="Shell"
  Base = -> Loft001
  Tool = -> Loft002
FEATURE [Sketcher::SketchObject] Sketch020
  FullyConstrained = true
  sketch-geometry (4):
    g0: LineSegment StartX=0 StartY=275 StartZ=0 EndX=275 EndY=275 EndZ=0
    g1: LineSegment StartX=275 StartY=275 StartZ=0 EndX=275 EndY=0 EndZ=0
    g2: LineSegment StartX=275 StartY=0 StartZ=0 EndX=0 EndY=0 EndZ=0
    g3: LineSegment StartX=0 StartY=0 StartZ=0 EndX=0 EndY=275 EndZ=0
  constraints (11):
    c: Coincident(g0,g1)
    c: Coincident(g1,g2)
    c: Coincident(g2,g3)
    c: Coincident(g3,g0)
    c: Horizontal(g0)
    c: Horizontal(g2)
    c: Vertical(g1)
    c: Vertical(g3)
    c: Coincident(g2,g-1)
    c: DistanceX(g2,g2) = 275
    c: DistanceY(g3,g3) = 275
FEATURE [Part::Extrusion] Extrude  label="level01s"
  Base = -> Sketch020
  Dir = (0,0,1)
  DirMode = 2
  FaceMakerClass = Part::FaceMakerBullseye
  LengthFwd = 10
  LengthRev = 0
  Placement = pos=(0,0,64) rot=(0,0,1;0rad)
  Solid = true
  Symmetric = false
FEATURE [Sketcher::SketchObject] Sketch021
  FullyConstrained = true
  sketch-geometry (4):
    g0: LineSegment StartX=0 StartY=275 StartZ=0 EndX=275 EndY=275 EndZ=0
    g1: LineSegment StartX=275 StartY=275 StartZ=0 EndX=275 EndY=0 EndZ=0
    g2: LineSegment StartX=275 StartY=0 StartZ=0 EndX=0 EndY=0 EndZ=0
    g3: LineSegment StartX=0 StartY=0 StartZ=0 EndX=0 EndY=275 EndZ=0
  constraints (11):
    c: Coincident(g0,g1)
    c: Coincident(g1,g2)
    c: Coincident(g2,g3)
    c: Coincident(g3,g0)
    c: Horizontal(g0)
    c: Horizontal(g2)
    c: Vertical(g1)
    c: Vertical(g3)
    c: Coincident(g2,g-1)
    c: DistanceX(g2,g2) = 275
    c: DistanceY(g3,g3) = 275
FEATURE [Sketcher::SketchObject] Sketch022
  FullyConstrained = true
  Placement = pos=(0,0,175.1) rot=(0,0,1;0rad)
  sketch-geometry (5):
    g0: GeomPoint X=137.5 Y=137.5 Z=0
    g1: LineSegment StartX=137.55 StartY=137.55 StartZ=0 EndX=137.55 EndY=137.45 EndZ=0
    g2: LineSegment StartX=137.55 StartY=137.45 StartZ=0 EndX=137.45 EndY=137.45 EndZ=0
    g3: LineSegment StartX=137.45 StartY=137.45 StartZ=0 EndX=137.45 EndY=137.55 EndZ=0
    g4: LineSegment StartX=137.45 StartY=137.55 StartZ=0 EndX=137.55 EndY=137.55 EndZ=0
  constraints (14):
    c: Coincident(g1,g2)
    c: Horizontal(g2)
    c: Vertical(g1)
    c: DistanceX(g2,g2) = 0.1
    c: DistanceX(g2,g0) = 0.05
    c: DistanceY(g1,g1) = 0.1
    c: DistanceY(g1,g0) = -0.05
    c: DistanceX(g0) = 137.5
    c: DistanceY(g0) = 137.5
    c: Coincident(g3,g2)
    c: Vertical(g3)
    c: Coincident(g4,g3)
    c: Coincident(g4,g1)
    c: Horizontal(g4)
FEATURE [Part::Loft] Loft003  label="outerLayer003"
  Closed = false
  MaxDegree = 5
  Placement = pos=(0,0,-8.25) rot=(0,0,1;0rad)
  Ruled = false
  Sections = -> [Sketch021,Sketch022]
  Solid = true
FEATURE [Part::MultiCommon] Common  label="level1"
  Shapes = -> [Extrude,Loft003]
FEATURE [Sketcher::SketchObject] Sketch
  FullyConstrained = true
  sketch-geometry (4):
    g0: Circle CenterX=75 CenterY=200 CenterZ=0 NormalX=0 NormalY=0 NormalZ=1 AngleXU=0 Radius=7.5
    g1: Circle CenterX=125 CenterY=200 CenterZ=0 NormalX=0 NormalY=0 NormalZ=1 AngleXU=0 Radius=7.5
    g2: Circle CenterX=75 CenterY=75 CenterZ=0 NormalX=0 NormalY=0 NormalZ=1 AngleXU=0 Radius=7.5
    g3: Circle CenterX=200 CenterY=75 CenterZ=0 NormalX=0 NormalY=0 NormalZ=1 AngleXU=0 Radius=7.5
  constraints (12):
    c: Equal(g0,g1)
    c: Equal(g0,g2)
    c: Equal(g0,g3)
    c: Diameter(g0) = 15
    c: DistanceX(g2) = 75
    c: DistanceY(g2) = 75
    c: DistanceX(g2,g0) = 0
    c: DistanceY(g0) = 200
    c: DistanceY(g1,g0) = 0
    c: DistanceX(g0,g1) = 50
    c: DistanceY(g2,g3) = 0
    c: DistanceX(g3) = 200
FEATURE [Part::Extrusion] Extrude001
  Base = -> Sketch
  Dir = (0,0,1)
  DirMode = 2
  FaceMakerClass = Part::FaceMakerBullseye
  LengthFwd = 63.75
  LengthRev = 0
  Solid = true
  Symmetric = false
FEATURE [Sketcher::SketchObject] Sketch023
  FullyConstrained = true
  sketch-geometry (4):
    g0: LineSegment StartX=0 StartY=275 StartZ=0 EndX=275 EndY=275 EndZ=0
    g1: LineSegment StartX=275 StartY=275 StartZ=0 EndX=275 EndY=0 EndZ=0
    g2: LineSegment StartX=275 StartY=0 StartZ=0 EndX=0 EndY=0 EndZ=0
    g3: LineSegment StartX=0 StartY=0 StartZ=0 EndX=0 EndY=275 EndZ=0
  constraints (11):
    c: Coincident(g0,g1)
    c: Coincident(g1,g2)
    c: Coincident(g2,g3)
    c: Coincident(g3,g0)
    c: Horizontal(g0)
    c: Horizontal(g2)
    c: Vertical(g1)
    c: Vertical(g3)
    c: Coincident(g2,g-1)
    c: DistanceX(g2,g2) = 275
    c: DistanceY(g3,g3) = 275
FEATURE [Sketcher::SketchObject] Sketch024
  FullyConstrained = true
  Placement = pos=(0,0,175.1) rot=(0,0,1;0rad)
  sketch-geometry (5):
    g0: GeomPoint X=137.5 Y=137.5 Z=0
    g1: LineSegment StartX=137.55 StartY=137.55 StartZ=0 EndX=137.55 EndY=137.45 EndZ=0
    g2: LineSegment StartX=137.55 StartY=137.45 StartZ=0 EndX=137.45 EndY=137.45 EndZ=0
    g3: LineSegment StartX=137.45 StartY=137.45 StartZ=0 EndX=137.45 EndY=137.55 EndZ=0
    g4: LineSegment StartX=137.45 StartY=137.55 StartZ=0 EndX=137.55 EndY=137.55 EndZ=0
  constraints (14):
    c: Coincident(g1,g2)
    c: Horizontal(g2)
    c: Vertical(g1)
    c: DistanceX(g2,g2) = 0.1
    c: DistanceX(g2,g0) = 0.05
    c: DistanceY(g1,g1) = 0.1
    c: DistanceY(g1,g0) = -0.05
    c: DistanceX(g0) = 137.5
    c: DistanceY(g0) = 137.5
    c: Coincident(g3,g2)
    c: Vertical(g3)
    c: Coincident(g4,g3)
    c: Coincident(g4,g1)
    c: Horizontal(g4)
FEATURE [Part::Loft] Loft004  label="outerLayer004"
  Closed = false
  MaxDegree = 5
  Placement = pos=(0,0,-8.25) rot=(0,0,1;0rad)
  Ruled = false
  Sections = -> [Sketch023,Sketch024]
  Solid = true
FEATURE [Sketcher::SketchObject] Sketch025
  FullyConstrained = true
  sketch-geometry (4):
    g0: LineSegment StartX=0 StartY=275 StartZ=0 EndX=275 EndY=275 EndZ=0
    g1: LineSegment StartX=275 StartY=275 StartZ=0 EndX=275 EndY=0 EndZ=0
    g2: LineSegment StartX=275 StartY=0 StartZ=0 EndX=0 EndY=0 EndZ=0
    g3: LineSegment StartX=0 StartY=0 StartZ=0 EndX=0 EndY=275 EndZ=0
  constraints (11):
    c: Coincident(g0,g1)
    c: Coincident(g1,g2)
    c: Coincident(g2,g3)
    c: Coincident(g3,g0)
    c: Horizontal(g0)
    c: Horizontal(g2)
    c: Vertical(g1)
    c: Vertical(g3)
    c: Coincident(g2,g-1)
    c: DistanceX(g2,g2) = 275
    c: DistanceY(g3,g3) = 275
FEATURE [Part::Extrusion] Extrude002  label="level01s001"
  Base = -> Sketch025
  Dir = (0,0,1)
  DirMode = 2
  FaceMakerClass = Part::FaceMakerBullseye
  LengthFwd = 5
  LengthRev = 0
  Solid = true
  Symmetric = false
FEATURE [Part::MultiCommon] Common001  label="BaseLevel"
  Shapes = -> [Loft004,Extrude002]
FEATURE [Part::MultiFuse] Fusion  label="level2"
  Shapes = -> [Extrude001,Common001]
FEATURE [Sketcher::SketchObject] Sketch026
  FullyConstrained = true
  Placement = pos=(0,0,0) rot=(1,0,0;1.5708rad)
  sketch-geometry (6):
    g0: LineSegment StartX=46 StartY=5 StartZ=0 EndX=40 EndY=5 EndZ=0
    g1: LineSegment StartX=40 StartY=5 StartZ=0 EndX=40 EndY=41.5 EndZ=0
    g2: LineSegment StartX=40 StartY=41.5 StartZ=0 EndX=115 EndY=41.5 EndZ=0
    g3: LineSegment StartX=115 StartY=41.5 StartZ=0 EndX=115 EndY=35.5 EndZ=0
    g4: LineSegment StartX=115 StartY=35.5 StartZ=0 EndX=46 EndY=35.5 EndZ=0
    g5: LineSegment StartX=46 StartY=35.5 StartZ=0 EndX=46 EndY=5 EndZ=0
  constraints (18):
    c: Horizontal(g0)
    c: Coincident(g1,g0)
    c: Vertical(g1)
    c: Coincident(g2,g1)
    c: Horizontal(g2)
    c: Coincident(g3,g2)
    c: Coincident(g4,g3)
    c: Horizontal(g4)
    c: Coincident(g5,g4)
    c: Coincident(g5,g0)
    c: Vertical(g5)
    c: Vertical(g3)
    c: DistanceY(g0) = 5
    c: DistanceY(g3,g3) = 6
    c: DistanceX(g0,g0) = 6
    c: DistanceX(g1) = 40
    c: DistanceX(g2) = 115
    c: DistanceY(g4) = 35.5
FEATURE [Part::Extrusion] Extrude003
  Base = -> Sketch026
  Dir = (0,-1,2e-16)
  DirMode = 2
  FaceMakerClass = Part::FaceMakerBullseye
  LengthFwd = 45
  LengthRev = 0
  Placement = pos=(0,190,0) rot=(0,0,1;0rad)
  Solid = true
  Symmetric = false
FEATURE [Part::MultiFuse] Fusion056  label="level2s"
  Shapes = -> [Fusion,Extrude003]
FEATURE [Sketcher::SketchObject] Sketch027
  FullyConstrained = true
  sketch-geometry (15):
    g0: Circle CenterX=51.75 CenterY=92.5 CenterZ=0 NormalX=0 NormalY=0 NormalZ=1 AngleXU=0 Radius=1.625
    g1: Circle CenterX=87.75 CenterY=108.5 CenterZ=0 NormalX=0 NormalY=0 NormalZ=1 AngleXU=0 Radius=1.625
    g2: Circle CenterX=121.75 CenterY=185.5 CenterZ=0 NormalX=0 NormalY=0 NormalZ=1 AngleXU=0 Radius=2
    g3: Circle CenterX=147.3 CenterY=147.75 CenterZ=0 NormalX=0 NormalY=0 NormalZ=1 AngleXU=0 Radius=1.625
    g4: Circle CenterX=218.8 CenterY=147.75 CenterZ=0 NormalX=0 NormalY=0 NormalZ=1 AngleXU=0 Radius=1.625
    g5: Circle CenterX=218.8 CenterY=219.25 CenterZ=0 NormalX=0 NormalY=0 NormalZ=1 AngleXU=0 Radius=1.625
    g6: Circle CenterX=147.3 CenterY=219.25 CenterZ=0 NormalX=0 NormalY=0 NormalZ=1 AngleXU=0 Radius=1.625
    g7: Circle CenterX=75 CenterY=200 CenterZ=0 NormalX=0 NormalY=0 NormalZ=1 AngleXU=0 Radius=2.8
    g8: Circle CenterX=125 CenterY=200 CenterZ=0 NormalX=0 NormalY=0 NormalZ=1 AngleXU=0 Radius=2.8
    g9: Circle CenterX=200 CenterY=75 CenterZ=0 NormalX=0 NormalY=0 NormalZ=1 AngleXU=0 Radius=2.8
    g10: Circle CenterX=75 CenterY=75 CenterZ=0 NormalX=0 NormalY=0 NormalZ=1 AngleXU=0 Radius=2.8
    g11: Circle CenterX=91 CenterY=186.5 CenterZ=0 NormalX=0 NormalY=0 NormalZ=1 AngleXU=0 Radius=1.65
    g12: Circle CenterX=109 CenterY=186.5 CenterZ=0 NormalX=0 NormalY=0 NormalZ=1 AngleXU=0 Radius=1.65
    g13: Circle CenterX=91 CenterY=151.5 CenterZ=0 NormalX=0 NormalY=0 NormalZ=1 AngleXU=0 Radius=1.65
    g14: Circle CenterX=109 CenterY=151.5 CenterZ=0 NormalX=0 NormalY=0 NormalZ=1 AngleXU=0 Radius=1.65
  constraints (42):
    c: Equal(g0,g1)
    c: Equal(g0, g3-g6) x4
    c: Diameter(g0) = 3.25
    c: DistanceX(g0) = 51.75
    c: DistanceY(g0) = 92.5
    c: DistanceY(g0,g1) = 16
    c: DistanceX(g0,g1) = 36
    c: DistanceY(g1,g2) = 77
    c: DistanceX(g1,g2) = 34
    c: Diameter(g2) = 4
    c: DistanceY(g3) = 147.75
    c: DistanceX(g3) = 147.3
    c: DistanceX(g3,g4) = 71.5
    c: DistanceY(g4,g3) = 0
    c: DistanceX(g3,g6) = 0
    c: DistanceY(g3,g6) = 71.5
    c: DistanceY(g6,g5) = 0
    c: DistanceX(g4,g5) = 0
    c: DistanceY(g10) = 75
    c: DistanceY(g10,g9) = 0
    c: DistanceX(g10) = 75
    c: DistanceX(g10,g9) = 125
    c: DistanceY(g10,g7) = 125
    c: DistanceX(g7,g10) = 0
    c: DistanceX(g7,g8) = 50
    c: DistanceY(g8,g7) = 0
    c: Equal(g7,g8)
    c: Equal(g7,g10)
    c: Equal(g7,g9)
    c: Diameter(g7) = 5.6
    c: Equal(g11,g12)
    c: Equal(g11,g13)
    c: Equal(g11,g14)
    c: Diameter(g11) = 3.3
    c: DistanceY(g13) = 151.5
    c: DistanceX(g13) = 91
    c: DistanceY(g14,g13) = 0
    c: DistanceX(g13,g14) = 18
    c: DistanceY(g13,g11) = 35
    c: DistanceX(g13,g11) = 0
    c: DistanceY(g11,g12) = 0
    c: DistanceX(g12,g14) = 0
FEATURE [Part::Extrusion] Extrude004
  Base = -> Sketch027
  Dir = (0,0,1)
  DirMode = 2
  FaceMakerClass = Part::FaceMakerBullseye
  LengthFwd = 80
  LengthRev = 0
  Solid = true
  Symmetric = false
FEATURE [Part::Cut] Cut001  label="level02"
  Base = -> Fusion056
  Tool = -> Extrude004
FEATURE [Sketcher::SketchObject] Sketch029
  FullyConstrained = true
  Placement = pos=(0,0,0) rot=(1,0,0;1.5708rad)
  sketch-geometry (8):
    g0: LineSegment StartX=105 StartY=74 StartZ=0 EndX=111 EndY=74 EndZ=0
    g1: LineSegment StartX=164 StartY=115.5 StartZ=0 EndX=164 EndY=74 EndZ=0
    g2: LineSegment StartX=164 StartY=74 StartZ=0 EndX=170 EndY=74 EndZ=0
    g3: LineSegment StartX=170 StartY=74 StartZ=0 EndX=170 EndY=119 EndZ=0
    g4: LineSegment StartX=170 StartY=119 StartZ=0 EndX=105 EndY=119 EndZ=0
    g5: LineSegment StartX=105 StartY=119 StartZ=0 EndX=105 EndY=74 EndZ=0
    g6: LineSegment StartX=111 StartY=74 StartZ=0 EndX=111 EndY=115.5 EndZ=0
    g7: LineSegment StartX=111 StartY=115.5 StartZ=0 EndX=164 EndY=115.5 EndZ=0
  constraints (24):
    c: Horizontal(g0)
    c: Vertical(g1)
    c: Horizontal(g2)
    c: Vertical(g3)
    c: Coincident(g4,g3)
    c: Horizontal(g4)
    c: Coincident(g5,g4)
    c: Coincident(g5,g0)
    c: Vertical(g5)
    c: Coincident(g1,g2)
    c: Coincident(g2,g3)
    c: DistanceY(g0,g1) = 0
    c: DistanceY(g0) = 74
    c: DistanceX(g0) = 105
    c: DistanceX(g1,g2) = 6
    c: DistanceX(g2) = 170
    c: Vertical(g6)
    c: Coincident(g7,g6)
    c: Horizontal(g7)
    c: Coincident(g1,g7)
    c: DistanceY(g1,g3) = 3.5
    c: DistanceX(g4,g6) = 6
    c: Coincident(g0,g6)
    c: DistanceY(g0,g6) = 41.5
FEATURE [Part::Extrusion] Extrude005
  Base = -> Sketch029
  Dir = (0,-1,-6e-16)
  DirMode = 2
  FaceMakerClass = Part::FaceMakerBullseye
  LengthFwd = 20
  LengthRev = 0
  Placement = pos=(0,127.5,0) rot=(0,0,1;0rad)
  Reversed = true
  Solid = true
  Symmetric = false
FEATURE [Sketcher::SketchObject] Sketch030
  FullyConstrained = true
  Placement = pos=(0,0,0) rot=(1,0,0;1.5708rad)
  sketch-geometry (10):
    g0: LineSegment StartX=112 StartY=84 StartZ=0 EndX=122 EndY=84 EndZ=0
    g1: LineSegment StartX=122 StartY=84 StartZ=0 EndX=122 EndY=74 EndZ=0
    g2: LineSegment StartX=122 StartY=74 StartZ=0 EndX=112 EndY=74 EndZ=0
    g3: LineSegment StartX=112 StartY=74 StartZ=0 EndX=112 EndY=84 EndZ=0
    g4: LineSegment StartX=153 StartY=120 StartZ=0 EndX=163 EndY=120 EndZ=0
    g5: LineSegment StartX=163 StartY=120 StartZ=0 EndX=163 EndY=74 EndZ=0
    g6: LineSegment StartX=163 StartY=74 StartZ=0 EndX=153 EndY=74 EndZ=0
    g7: LineSegment StartX=153 StartY=74 StartZ=0 EndX=153 EndY=120 EndZ=0
    g8: Circle CenterX=117.1 CenterY=78.6 CenterZ=0 NormalX=0 NormalY=0 NormalZ=1 AngleXU=0 Radius=1.6
    g9: Circle CenterX=157.85 CenterY=115.4 CenterZ=0 NormalX=0 NormalY=0 NormalZ=1 AngleXU=0 Radius=1.6
  constraints (30):
    c: Coincident(g0,g1)
    c: Coincident(g1,g2)
    c: Coincident(g2,g3)
    c: Coincident(g3,g0)
    c: Horizontal(g0)
    c: Horizontal(g2)
    c: Vertical(g1)
    c: Vertical(g3)
    c: Coincident(g4,g5)
    c: Coincident(g5,g6)
    c: Coincident(g6,g7)
    c: Coincident(g7,g4)
    c: Horizontal(g4)
    c: Horizontal(g6)
    c: Vertical(g5)
    c: Vertical(g7)
    c: DistanceX(g2) = 112
    c: DistanceY(g2,g0) = 10
    c: DistanceX(g2,g0) = 10
    c: DistanceY(g2) = 74
    c: DistanceY(g1,g6) = 0
    c: DistanceX(g1,g6) = 31
    c: DistanceX(g4,g4) = 10
    c: DistanceY(g6,g4) = 46
    c: Equal(g8,g9)
    c: Diameter(g8) = 3.2
    c: DistanceY(g2,g8) = 4.6
    c: DistanceX(g2,g8) = 5.1
    c: DistanceX(g8,g9) = 40.75
    c: DistanceY(g8,g9) = 36.8
FEATURE [Part::Extrusion] Extrude006
  Base = -> Sketch030
  Dir = (0,-1,-6e-16)
  DirMode = 2
  FaceMakerClass = Part::FaceMakerBullseye
  LengthFwd = 10
  LengthRev = 0
  Placement = pos=(0,115.25,0) rot=(0,0,1;0rad)
  Reversed = true
  Solid = true
  Symmetric = false
FEATURE [Sketcher::SketchObject] Sketch031
  FullyConstrained = true
  Placement = pos=(0,0,0) rot=(1,0,0;1.5708rad)
  sketch-geometry (10):
    g0: LineSegment StartX=118 StartY=109 StartZ=0 EndX=128 EndY=109 EndZ=0
    g1: LineSegment StartX=128 StartY=109 StartZ=0 EndX=128 EndY=74 EndZ=0
    g2: LineSegment StartX=128 StartY=74 StartZ=0 EndX=118 EndY=74 EndZ=0
    g3: LineSegment StartX=118 StartY=74 StartZ=0 EndX=118 EndY=109 EndZ=0
    g4: LineSegment StartX=150 StartY=92 StartZ=0 EndX=160 EndY=92 EndZ=0
    g5: LineSegment StartX=160 StartY=92 StartZ=0 EndX=160 EndY=74 EndZ=0
    g6: LineSegment StartX=160 StartY=74 StartZ=0 EndX=150 EndY=74 EndZ=0
    g7: LineSegment StartX=150 StartY=74 StartZ=0 EndX=150 EndY=92 EndZ=0
    g8: Circle CenterX=122.95 CenterY=104.43 CenterZ=0 NormalX=0 NormalY=0 NormalZ=1 AngleXU=0 Radius=1.6
    g9: Circle CenterX=154.95 CenterY=88.19 CenterZ=0 NormalX=0 NormalY=0 NormalZ=1 AngleXU=0 Radius=1.6
  constraints (30):
    c: Coincident(g0,g1)
    c: Coincident(g1,g2)
    c: Coincident(g2,g3)
    c: Coincident(g3,g0)
    c: Horizontal(g0)
    c: Horizontal(g2)
    c: Vertical(g1)
    c: Vertical(g3)
    c: Coincident(g4,g5)
    c: Coincident(g5,g6)
    c: Coincident(g6,g7)
    c: Coincident(g7,g4)
    c: Horizontal(g4)
    c: Horizontal(g6)
    c: Vertical(g5)
    c: Vertical(g7)
    c: DistanceY(g2) = 74
    c: DistanceY(g2,g0) = 35
    c: DistanceX(g2,g2) = 10
    c: DistanceX(g2) = 118
    c: DistanceX(g1,g6) = 22
    c: DistanceX(g4,g4) = 10
    c: DistanceY(g6,g4) = 18
    c: DistanceY(g1,g6) = 0
    c: DistanceX(g2,g8) = 4.95
    c: DistanceY(g2,g8) = 30.43
    c: DistanceX(g8,g9) = 32
    c: DistanceY(g9,g8) = 16.24
    c: Equal(g8,g9)
    c: Diameter(g8) = 3.2
FEATURE [Part::Extrusion] Extrude007
  Base = -> Sketch031
  Dir = (0,-1,-3e-16)
  DirMode = 2
  FaceMakerClass = Part::FaceMakerBullseye
  LengthFwd = 10
  LengthRev = 0
  Placement = pos=(0,162.5,0) rot=(0,0,1;0rad)
  Solid = true
  Symmetric = false
FEATURE [Part::MultiFuse] Fusion057  label="levell1s"
  Shapes = -> [Extrude005,Extrude006,Extrude007,Common]
FEATURE [Sketcher::SketchObject] Sketch032
  FullyConstrained = true
  MapMode = 2
  Support = -> [Fusion057]
  sketch-geometry (17):
    g0: ArcOfCircle CenterX=137.5 CenterY=137.5 CenterZ=0 NormalX=0 NormalY=0 NormalZ=1 AngleXU=0 Radius=3.2 StartAngle=3.14159 EndAngle=6.28319
    g1: LineSegment StartX=134.3 StartY=137.5 StartZ=0 EndX=134.3 EndY=147.5 EndZ=0
    g2: LineSegment StartX=134.3 StartY=147.5 StartZ=0 EndX=140.7 EndY=147.5 EndZ=0
    g3: LineSegment StartX=140.7 StartY=147.5 StartZ=0 EndX=140.7 EndY=137.5 EndZ=0
    g4: Circle CenterX=75 CenterY=75 CenterZ=0 NormalX=0 NormalY=0 NormalZ=1 AngleXU=0 Radius=2.125
    g5: Circle CenterX=200 CenterY=75 CenterZ=0 NormalX=0 NormalY=0 NormalZ=1 AngleXU=0 Radius=2.125
    g6: Circle CenterX=75 CenterY=200 CenterZ=0 NormalX=0 NormalY=0 NormalZ=1 AngleXU=0 Radius=2.125
    g7: Circle CenterX=125 CenterY=200 CenterZ=0 NormalX=0 NormalY=0 NormalZ=1 AngleXU=0 Radius=2.125
    g8: Circle CenterX=200 CenterY=200 CenterZ=0 NormalX=0 NormalY=0 NormalZ=1 AngleXU=0 Radius=2.125
    g9: Circle CenterX=170.05 CenterY=190.35 CenterZ=0 NormalX=0 NormalY=0 NormalZ=1 AngleXU=0 Radius=1.6
    g10: Circle CenterX=190.35 CenterY=190.35 CenterZ=0 NormalX=0 NormalY=0 NormalZ=1 AngleXU=0 Radius=1.6
    g11: Circle CenterX=190.4 CenterY=170.05 CenterZ=0 NormalX=0 NormalY=0 NormalZ=1 AngleXU=0 Radius=1.6
    g12: Circle CenterX=170.05 CenterY=170.05 CenterZ=0 NormalX=0 NormalY=0 NormalZ=1 AngleXU=0 Radius=1.6
    g13: Circle CenterX=137.5 CenterY=85 CenterZ=0 NormalX=0 NormalY=0 NormalZ=1 AngleXU=0 Radius=2
    g14: Circle CenterX=137.5 CenterY=190 CenterZ=0 NormalX=0 NormalY=0 NormalZ=1 AngleXU=0 Radius=2
    g15: Circle CenterX=85 CenterY=137.5 CenterZ=0 NormalX=0 NormalY=0 NormalZ=1 AngleXU=0 Radius=2
    g16: Circle CenterX=190 CenterY=137.5 CenterZ=0 NormalX=0 NormalY=0 NormalZ=1 AngleXU=0 Radius=2
  constraints (52):
    c: Coincident(g1,g0)
    c: Vertical(g1)
    c: Coincident(g2,g1)
    c: Horizontal(g2)
    c: Coincident(g3,g2)
    c: Coincident(g3,g0)
    c: Vertical(g3)
    c: DistanceX(g0,g0) = 6.4
    c: Diameter(g0) = 6.4
    c: DistanceY(g0,g0) = 0
    c: DistanceX(g0) = 137.5
    c: DistanceY(g0) = 137.5
    c: DistanceY(g0,g1) = 10
    c: DistanceX(g4) = 75
    c: DistanceY(g4) = 75
    c: DistanceX(g4,g5) = 125
    c: DistanceX(g4,g6) = 0
    c: DistanceY(g4,g6) = 125
    c: DistanceY(g7,g6) = 0
    c: DistanceY(g7,g8) = 0
    c: DistanceX(g8,g5) = 0
    c: Equal(g5,g4)
    c: Equal(g5,g6)
    c: Equal(g5,g7)
    c: Equal(g5,g8)
    c: Diameter(g5) = 4.25
    c: DistanceX(g6,g7) = 50
    c: DistanceY(g5,g4) = 0
    c: DistanceX(g10,g8) = 9.65
    c: DistanceY(g11,g10) = 20.3
    c: DistanceY(g10,g8) = 9.65
    c: Equal(g9,g10)
    c: Equal(g9,g11)
    c: Equal(g9,g12)
    c: Diameter(g9) = 3.2
    c: DistanceX(g12,g11) = 20.35
    c: DistanceY(g12,g9) = 20.3
    c: DistanceX(g9,g10) = 20.3
    c: DistanceY(g12,g11) = 0
    c: DistanceX(g12,g9) = 0
    c: DistanceX(g0,g13) = 0
    c: DistanceX(g0,g14) = 0
    c: Equal(g13,g14)
    c: Diameter(g13) = 4
    c: DistanceY(g4,g13) = 10
    c: DistanceY(g14,g7) = 10
    c: DistanceY(g15,g0) = 0
    c: DistanceY(g16,g0) = 0
    c: DistanceX(g6,g15) = 10
    c: DistanceX(g16,g8) = 10
    c: Equal(g15,g16)
    c: Diameter(g15) = 4
FEATURE [Part::Extrusion] Extrude008
  Base = -> Sketch032
  Dir = (0,0,1)
  DirMode = 2
  FaceMakerClass = Part::FaceMakerBullseye
  LengthFwd = 60
  LengthRev = 0
  Placement = pos=(0,0,64) rot=(0,0,1;0rad)
  Solid = true
  Symmetric = false
FEATURE [Part::Cut] Cut002
  Base = -> Fusion057
  Tool = -> Extrude008
FEATURE [Sketcher::SketchObject] Sketch033
  FullyConstrained = true
  MapMode = 4
  Placement = pos=(0,0,0) rot=(0.57735,0.57735,0.57735;2.0944rad)
  Support = -> [Cut002]
  sketch-geometry (4):
    g0: Circle CenterX=131.15 CenterY=84.85 CenterZ=0 NormalX=0 NormalY=0 NormalZ=1 AngleXU=0 Radius=1.6
    g1: Circle CenterX=143.85 CenterY=84.85 CenterZ=0 NormalX=0 NormalY=0 NormalZ=1 AngleXU=0 Radius=1.6
    g2: Circle CenterX=143.85 CenterY=105.15 CenterZ=0 NormalX=0 NormalY=0 NormalZ=1 AngleXU=0 Radius=1.6
    g3: Circle CenterX=131.15 CenterY=105.15 CenterZ=0 NormalX=0 NormalY=0 NormalZ=1 AngleXU=0 Radius=1.6
  constraints (12):
    c: Equal(g0,g1)
    c: Equal(g0,g2)
    c: Equal(g0,g3)
    c: Diameter(g0) = 3.2
    c: DistanceX(g0) = 131.15
    c: DistanceY(g0) = 84.85
    c: DistanceY(g0,g1) = 0
    c: DistanceX(g0,g1) = 12.7
    c: DistanceX(g0,g3) = 0
    c: DistanceX(g2,g1) = 0
    c: DistanceY(g0,g3) = 20.3
    c: DistanceY(g3,g2) = 0
FEATURE [Part::Extrusion] Extrude009
  Base = -> Sketch033
  Dir = (1,0,0)
  DirMode = 2
  FaceMakerClass = Part::FaceMakerBullseye
  LengthFwd = 75
  LengthRev = 0
  Placement = pos=(100,0,0) rot=(0,0,1;0rad)
  Solid = true
  Symmetric = false
FEATURE [Part::Cut] Cut003  label="level01s002"
  Base = -> Cut002
  Tool = -> Extrude009
FEATURE [Sketcher::SketchObject] Sketch035
  FullyConstrained = true
  Placement = pos=(0,0,0) rot=(1,0,0;1.5708rad)
  sketch-geometry (36):
    g0: LineSegment StartX=50 StartY=66 StartZ=0 EndX=97.5 EndY=93.4241 EndZ=0
    g1: LineSegment StartX=97.5 StartY=93.4241 StartZ=0 EndX=97.5 EndY=97.4241 EndZ=0
    g2: LineSegment StartX=97.5 StartY=97.4241 StartZ=0 EndX=50 EndY=70 EndZ=0
    g3: LineSegment StartX=50 StartY=70 StartZ=0 EndX=50 EndY=66 EndZ=0
    g4: LineSegment StartX=50 StartY=78 StartZ=0 EndX=97.5 EndY=105.424 EndZ=0
    g5: LineSegment StartX=97.5 StartY=105.424 StartZ=0 EndX=97.5 EndY=101.424 EndZ=0
    g6: LineSegment StartX=97.5 StartY=101.424 StartZ=0 EndX=50 EndY=74 EndZ=0
    g7: LineSegment StartX=50 StartY=78 StartZ=0 EndX=50 EndY=74 EndZ=0
    g8: LineSegment StartX=50 StartY=86 StartZ=0 EndX=50 EndY=82 EndZ=0
    g9: LineSegment StartX=50 StartY=82 StartZ=0 EndX=97.5 EndY=109.424 EndZ=0
    g10: LineSegment StartX=97.5 StartY=109.424 StartZ=0 EndX=97.5 EndY=113.424 EndZ=0
    g11: LineSegment StartX=97.5 StartY=113.424 StartZ=0 EndX=50 EndY=86 EndZ=0
    g12: LineSegment StartX=75 StartY=120.424 StartZ=0 EndX=137.5 EndY=156.509 EndZ=0
    g13: LineSegment StartX=75 StartY=120.424 StartZ=0 EndX=75 EndY=116.424 EndZ=0
    g14: LineSegment StartX=75 StartY=116.424 StartZ=0 EndX=137.5 EndY=152.509 EndZ=0
    g15: LineSegment StartX=75 StartY=112.424 StartZ=0 EndX=137.5 EndY=148.509 EndZ=0
    g16: LineSegment StartX=137.5 StartY=144.509 StartZ=0 EndX=75 EndY=108.424 EndZ=0
    g17: LineSegment StartX=75 StartY=108.424 StartZ=0 EndX=75 EndY=112.424 EndZ=0
    g18: LineSegment StartX=137.5 StartY=156.509 StartZ=0 EndX=200 EndY=120.424 EndZ=0
    g19: LineSegment StartX=200 StartY=120.424 StartZ=0 EndX=200 EndY=116.424 EndZ=0
    g20: LineSegment StartX=200 StartY=116.424 StartZ=0 EndX=137.5 EndY=152.509 EndZ=0
    g21: LineSegment StartX=137.5 StartY=148.509 StartZ=0 EndX=200 EndY=112.424 EndZ=0
    g22: LineSegment StartX=200 StartY=112.424 StartZ=0 EndX=200 EndY=108.424 EndZ=0
    g23: LineSegment StartX=200 StartY=108.424 StartZ=0 EndX=137.5 EndY=144.509 EndZ=0
    g24: LineSegment StartX=177.5 StartY=113.424 StartZ=0 EndX=225 EndY=86 EndZ=0
    g25: LineSegment StartX=225 StartY=86 StartZ=0 EndX=225 EndY=82 EndZ=0
    g26: LineSegment StartX=225 StartY=82 StartZ=0 EndX=177.5 EndY=109.424 EndZ=0
    g27: LineSegment StartX=177.5 StartY=109.424 StartZ=0 EndX=177.5 EndY=113.424 EndZ=0
    g28: LineSegment StartX=177.5 StartY=105.424 StartZ=0 EndX=225 EndY=78 EndZ=0
    g29: LineSegment StartX=225 StartY=78 StartZ=0 EndX=225 EndY=74 EndZ=0
    g30: LineSegment StartX=225 StartY=74 StartZ=0 EndX=177.5 EndY=101.424 EndZ=0
    g31: LineSegment StartX=177.5 StartY=101.424 StartZ=0 EndX=177.5 EndY=105.424 EndZ=0
    g32: LineSegment StartX=177.5 StartY=97.4241 StartZ=0 EndX=225 EndY=70 EndZ=0
    g33: LineSegment StartX=225 StartY=70 StartZ=0 EndX=225 EndY=66 EndZ=0
    g34: LineSegment StartX=225 StartY=66 StartZ=0 EndX=177.5 EndY=93.4241 EndZ=0
    g35: LineSegment StartX=177.5 StartY=97.4241 StartZ=0 EndX=177.5 EndY=93.4241 EndZ=0
  constraints (108):
    c: Angle(g0) = 0.523599
    c: DistanceX(g0) = 50
    c: Coincident(g1,g0)
    c: Vertical(g1)
    c: Coincident(g2,g1)
    c: Coincident(g3,g2)
    c: Vertical(g3)
    c: DistanceY(g0,g2) = 4
    c: Parallel(g0,g2)
    c: Coincident(g0,g3)
    c: Coincident(g5,g4)
    c: Coincident(g7,g4)
    c: Coincident(g7,g6)
    c: Coincident(g10,g9)
    c: Coincident(g11,g8)
    c: Vertical(g8)
    c: Vertical(g7)
    c: Vertical(g5)
    c: Vertical(g10)
    c: Coincident(g5,g6)
    c: Coincident(g10,g11)
    c: Coincident(g8,g9)
    c: Parallel(g2,g6)
    c: Parallel(g6,g4)
    c: Parallel(g4,g9)
    c: Parallel(g9,g11)
    c: DistanceX(g6,g2) = 0
    c: DistanceX(g8,g4) = 0
    c: DistanceY(g2,g6) = 4
    c: DistanceY(g6,g4) = 4
    c: DistanceY(g4,g8) = 4
    c: DistanceY(g8,g8) = 4
    c: DistanceX(g5,g1) = 0
    c: DistanceX(g4,g9) = 0
    c: DistanceY(g0) = 66
    c: Coincident(g13,g12)
    c: Vertical(g13)
    c: Coincident(g17,g16)
    c: Coincident(g17,g15)
    c: DistanceY(g16,g10) = 5
    c: Vertical(g17)
    c: Parallel(g16,g11)
    c: DistanceY(g16,g15) = 4
    c: DistanceY(g15,g13) = 4
    c: Coincident(g13,g14)
    c: Parallel(g12,g14)
    c: Parallel(g14,g15)
    c: Parallel(g15,g16)
    c: DistanceY(g13,g12) = 4
    c: DistanceX(g15,g13) = 0
    c: DistanceX(g16,g16) = 62.5
    c: DistanceX(g14,g15) = 0
    c: Coincident(g18,g12)
    c: Coincident(g19,g18)
    c: Vertical(g19)
    c: Coincident(g20,g19)
    c: Coincident(g20,g14)
    c: Coincident(g21,g15)
    c: Coincident(g22,g21)
    c: Coincident(g23,g22)
    c: Coincident(g23,g16)
    c: Parallel(g23,g21)
    c: Parallel(g21,g20)
    c: Parallel(g20,g18)
    c: DistanceX(g14,g12) = 0
    c: DistanceX(g21,g19) = 0
    c: Vertical(g22)
    c: Coincident(g25,g24)
    c: Coincident(g26,g25)
    c: Coincident(g27,g26)
    c: Coincident(g27,g24)
    c: Vertical(g27)
    c: Coincident(g29,g28)
    c: Vertical(g29)
    c: Coincident(g31,g30)
    c: Coincident(g31,g28)
    c: Coincident(g33,g32)
    c: Vertical(g33)
    c: Coincident(g34,g33)
    c: Coincident(g35,g32)
    c: Coincident(g35,g34)
    c: DistanceY(g10,g24) = 0
    c: Vertical(g35)
    c: Vertical(g31)
    c: DistanceX(g28,g24) = 0
    c: DistanceX(g32,g30) = 0
    c: Vertical(g25)
    c: DistanceY(g26,g24) = 4
    c: DistanceY(g28,g26) = 4
    c: DistanceY(g30,g28) = 4
    c: DistanceY(g32,g30) = 4
    c: DistanceY(g34,g32) = 4
    c: Parallel(g34,g32)
    c: Parallel(g32,g30)
    c: Parallel(g30,g28)
    c: Parallel(g28,g26)
    c: Parallel(g26,g24)
    c: Parallel(g24,g23)
    c: Coincident(g29,g30)
    c: DistanceY(g33,g0) = 0
    c: DistanceX(g32,g29) = 0
    c: DistanceX(g28,g25) = 0
    c: DistanceX(g12) = 137.5
    c: DistanceY(g16,g15) = 4
    c: DistanceX(g12,g18) = 125
    c: DistanceY(g22,g16) = 0
    c: DistanceX(g10) = 97.5
    c: DistanceX(g10,g24) = 80
FEATURE [Part::Extrusion] Extrude010
  Base = -> Sketch035
  Dir = (0,-1,2e-16)
  DirMode = 2
  FaceMakerClass = Part::FaceMakerBullseye
  LengthFwd = 275
  LengthRev = 0
  Reversed = true
  Solid = true
  Symmetric = false
FEATURE [Sketcher::SketchObject] Sketch036
  FullyConstrained = true
  Placement = pos=(0,0,0) rot=(1,0,0;1.5708rad)
  sketch-geometry (36):
    g0: LineSegment StartX=50 StartY=66 StartZ=0 EndX=97.5 EndY=93.4241 EndZ=0
    g1: LineSegment StartX=97.5 StartY=93.4241 StartZ=0 EndX=97.5 EndY=97.4241 EndZ=0
    g2: LineSegment StartX=97.5 StartY=97.4241 StartZ=0 EndX=50 EndY=70 EndZ=0
    g3: LineSegment StartX=50 StartY=70 StartZ=0 EndX=50 EndY=66 EndZ=0
    g4: LineSegment StartX=50 StartY=78 StartZ=0 EndX=97.5 EndY=105.424 EndZ=0
    g5: LineSegment StartX=97.5 StartY=105.424 StartZ=0 EndX=97.5 EndY=101.424 EndZ=0
    g6: LineSegment StartX=97.5 StartY=101.424 StartZ=0 EndX=50 EndY=74 EndZ=0
    g7: LineSegment StartX=50 StartY=78 StartZ=0 EndX=50 EndY=74 EndZ=0
    g8: LineSegment StartX=50 StartY=86 StartZ=0 EndX=50 EndY=82 EndZ=0
    g9: LineSegment StartX=50 StartY=82 StartZ=0 EndX=97.5 EndY=109.424 EndZ=0
    g10: LineSegment StartX=97.5 StartY=109.424 StartZ=0 EndX=97.5 EndY=113.424 EndZ=0
    g11: LineSegment StartX=97.5 StartY=113.424 StartZ=0 EndX=50 EndY=86 EndZ=0
    g12: LineSegment StartX=75 StartY=120.424 StartZ=0 EndX=75 EndY=116.424 EndZ=0
    g13: LineSegment StartX=75 StartY=112.424 StartZ=0 EndX=137.5 EndY=148.509 EndZ=0
    g14: LineSegment StartX=137.5 StartY=144.509 StartZ=0 EndX=75 EndY=108.424 EndZ=0
    g15: LineSegment StartX=75 StartY=108.424 StartZ=0 EndX=75 EndY=112.424 EndZ=0
    g16: LineSegment StartX=137.5 StartY=148.509 StartZ=0 EndX=200 EndY=112.424 EndZ=0
    g17: LineSegment StartX=200 StartY=112.424 StartZ=0 EndX=200 EndY=108.424 EndZ=0
    g18: LineSegment StartX=200 StartY=108.424 StartZ=0 EndX=137.5 EndY=144.509 EndZ=0
    g19: LineSegment StartX=177.5 StartY=113.424 StartZ=0 EndX=225 EndY=86 EndZ=0
    g20: LineSegment StartX=225 StartY=86 StartZ=0 EndX=225 EndY=82 EndZ=0
    g21: LineSegment StartX=225 StartY=82 StartZ=0 EndX=177.5 EndY=109.424 EndZ=0
    g22: LineSegment StartX=177.5 StartY=109.424 StartZ=0 EndX=177.5 EndY=113.424 EndZ=0
    g23: LineSegment StartX=177.5 StartY=105.424 StartZ=0 EndX=225 EndY=78 EndZ=0
    g24: LineSegment StartX=225 StartY=78 StartZ=0 EndX=225 EndY=74 EndZ=0
    g25: LineSegment StartX=225 StartY=74 StartZ=0 EndX=177.5 EndY=101.424 EndZ=0
    g26: LineSegment StartX=177.5 StartY=101.424 StartZ=0 EndX=177.5 EndY=105.424 EndZ=0
    g27: LineSegment StartX=177.5 StartY=97.4241 StartZ=0 EndX=225 EndY=70 EndZ=0
    g28: LineSegment StartX=225 StartY=70 StartZ=0 EndX=225 EndY=66 EndZ=0
    g29: LineSegment StartX=225 StartY=66 StartZ=0 EndX=177.5 EndY=93.4241 EndZ=0
    g30: LineSegment StartX=177.5 StartY=97.4241 StartZ=0 EndX=177.5 EndY=93.4241 EndZ=0
    g31: LineSegment StartX=75 StartY=116.424 StartZ=0 EndX=137.5 EndY=152.509 EndZ=0
    g32: LineSegment StartX=137.5 StartY=152.509 StartZ=0 EndX=200 EndY=116.424 EndZ=0
    g33: LineSegment StartX=200 StartY=116.424 StartZ=0 EndX=200 EndY=120.424 EndZ=0
    g34: LineSegment StartX=200 StartY=120.424 StartZ=0 EndX=137.5 EndY=156.509 EndZ=0
    g35: LineSegment StartX=137.5 StartY=156.509 StartZ=0 EndX=75 EndY=120.424 EndZ=0
  constraints (108):
    c: Angle(g0) = 0.523599
    c: DistanceX(g0) = 50
    c: Coincident(g1,g0)
    c: Vertical(g1)
    c: Coincident(g2,g1)
    c: Coincident(g3,g2)
    c: Vertical(g3)
    c: DistanceY(g0,g2) = 4
    c: Parallel(g0,g2)
    c: Coincident(g0,g3)
    c: Coincident(g5,g4)
    c: Coincident(g7,g4)
    c: Coincident(g7,g6)
    c: Coincident(g10,g9)
    c: Coincident(g11,g8)
    c: Vertical(g8)
    c: Vertical(g7)
    c: Vertical(g5)
    c: Vertical(g10)
    c: Coincident(g5,g6)
    c: Coincident(g10,g11)
    c: Coincident(g8,g9)
    c: Parallel(g2,g6)
    c: Parallel(g6,g4)
    c: Parallel(g4,g9)
    c: Parallel(g9,g11)
    c: DistanceX(g6,g2) = 0
    c: DistanceX(g8,g4) = 0
    c: DistanceY(g2,g6) = 4
    c: DistanceY(g6,g4) = 4
    c: DistanceY(g4,g8) = 4
    c: DistanceY(g8,g8) = 4
    c: DistanceX(g5,g1) = 0
    c: DistanceX(g4,g9) = 0
    c: DistanceY(g0) = 66
    c: Vertical(g12)
    c: Coincident(g15,g14)
    c: Coincident(g15,g13)
    c: DistanceY(g14,g10) = 5
    c: Vertical(g15)
    c: Parallel(g14,g11)
    c: DistanceY(g14,g13) = 4
    c: DistanceY(g13,g12) = 4
    c: Parallel(g13,g14)
    c: DistanceY(g12,g12) = 4
    c: DistanceX(g13,g12) = 0
    c: DistanceX(g14,g14) = 62.5
    c: Coincident(g16,g13)
    c: Coincident(g17,g16)
    c: Coincident(g18,g17)
    c: Coincident(g18,g14)
    c: Parallel(g18,g16)
    c: Vertical(g17)
    c: Coincident(g20,g19)
    c: Coincident(g21,g20)
    c: Coincident(g22,g21)
    c: Coincident(g22,g19)
    c: Vertical(g22)
    c: Coincident(g24,g23)
    c: Vertical(g24)
    c: Coincident(g26,g25)
    c: Coincident(g26,g23)
    c: Coincident(g28,g27)
    c: Vertical(g28)
    c: Coincident(g29,g28)
    c: Coincident(g30,g27)
    c: Coincident(g30,g29)
    c: DistanceY(g10,g19) = 0
    c: Vertical(g30)
    c: Vertical(g26)
    c: DistanceX(g23,g19) = 0
    c: DistanceX(g27,g25) = 0
    c: Vertical(g20)
    c: DistanceY(g21,g19) = 4
    c: DistanceY(g23,g21) = 4
    c: DistanceY(g25,g23) = 4
    c: DistanceY(g27,g25) = 4
    c: DistanceY(g29,g27) = 4
    c: Parallel(g29,g27)
    c: Parallel(g27,g25)
    c: Parallel(g25,g23)
    c: Parallel(g23,g21)
    c: Parallel(g21,g19)
    c: Parallel(g19,g18)
    c: Coincident(g24,g25)
    c: DistanceY(g28,g0) = 0
    c: DistanceX(g27,g24) = 0
    c: DistanceX(g23,g20) = 0
    c: DistanceX(g13) = 137.5
    c: DistanceX(g14,g10) = 22.5
    c: DistanceX(g19,g17) = 22.5
    c: DistanceX(g14,g17) = 125
    c: DistanceX(g14,g13) = 0
    c: DistanceY(g17,g14) = 0
    c: Coincident(g31,g12)
    c: Coincident(g32,g31)
    c: Vertical(g33)
    c: Coincident(g34,g33)
    c: Coincident(g35,g12)
    c: DistanceX(g13,g31) = 0
    c: Coincident(g34,g35)
    c: DistanceX(g34,g31) = 0
    c: Parallel(g13,g31)
    c: Parallel(g31,g35)
    c: Parallel(g16,g32)
    c: Parallel(g32,g34)
    c: Coincident(g32,g33)
    c: DistanceX(g16,g32) = 0
FEATURE [Part::Extrusion] Extrude011
  Base = -> Sketch036
  Dir = (0,-1,2e-16)
  DirMode = 2
  FaceMakerClass = Part::FaceMakerBullseye
  LengthFwd = 275
  LengthRev = 0
  Placement = pos=(275,0,0) rot=(0,0,1;1.5708rad)
  Reversed = true
  Solid = true
  Symmetric = false
FEATURE [Part::MultiFuse] Fusion058  label="keeps-legacy"
  Shapes = -> [Extrude010,Extrude011]
FEATURE [Sketcher::SketchObject] Sketch037
  FullyConstrained = true
  sketch-geometry (4):
    g0: LineSegment StartX=0 StartY=275 StartZ=0 EndX=275 EndY=275 EndZ=0
    g1: LineSegment StartX=275 StartY=275 StartZ=0 EndX=275 EndY=0 EndZ=0
    g2: LineSegment StartX=275 StartY=0 StartZ=0 EndX=0 EndY=0 EndZ=0
    g3: LineSegment StartX=0 StartY=0 StartZ=0 EndX=0 EndY=275 EndZ=0
  constraints (11):
    c: Coincident(g0,g1)
    c: Coincident(g1,g2)
    c: Coincident(g2,g3)
    c: Coincident(g3,g0)
    c: Horizontal(g0)
    c: Horizontal(g2)
    c: Vertical(g1)
    c: Vertical(g3)
    c: Coincident(g2,g-1)
    c: DistanceX(g2,g2) = 275
    c: DistanceY(g3,g3) = 275
FEATURE [Sketcher::SketchObject] Sketch038
  FullyConstrained = true
  Placement = pos=(0,0,175.1) rot=(0,0,1;0rad)
  sketch-geometry (5):
    g0: GeomPoint X=137.5 Y=137.5 Z=0
    g1: LineSegment StartX=137.55 StartY=137.55 StartZ=0 EndX=137.55 EndY=137.45 EndZ=0
    g2: LineSegment StartX=137.55 StartY=137.45 StartZ=0 EndX=137.45 EndY=137.45 EndZ=0
    g3: LineSegment StartX=137.45 StartY=137.45 StartZ=0 EndX=137.45 EndY=137.55 EndZ=0
    g4: LineSegment StartX=137.45 StartY=137.55 StartZ=0 EndX=137.55 EndY=137.55 EndZ=0
  constraints (14):
    c: Coincident(g1,g2)
    c: Horizontal(g2)
    c: Vertical(g1)
    c: DistanceX(g2,g2) = 0.1
    c: DistanceX(g2,g0) = 0.05
    c: DistanceY(g1,g1) = 0.1
    c: DistanceY(g1,g0) = -0.05
    c: DistanceX(g0) = 137.5
    c: DistanceY(g0) = 137.5
    c: Coincident(g3,g2)
    c: Vertical(g3)
    c: Coincident(g4,g3)
    c: Coincident(g4,g1)
    c: Horizontal(g4)
FEATURE [Part::Loft] Loft005  label="outerLayer005"
  Closed = false
  MaxDegree = 5
  Ruled = false
  Sections = -> [Sketch037,Sketch038]
  Solid = true
FEATURE [Sketcher::SketchObject] Sketch039
  FullyConstrained = true
  Placement = pos=(0,0,0) rot=(1,0,0;1.5708rad)
  sketch-geometry (28):
    g0: LineSegment StartX=50 StartY=70 StartZ=0 EndX=97.5 EndY=97.4241 EndZ=0
    g1: LineSegment StartX=97.5 StartY=97.4241 StartZ=0 EndX=97.5 EndY=101.424 EndZ=0
    g2: LineSegment StartX=97.5 StartY=101.424 StartZ=0 EndX=50 EndY=74 EndZ=0
    g3: LineSegment StartX=50 StartY=74 StartZ=0 EndX=50 EndY=70 EndZ=0
    g4: LineSegment StartX=50 StartY=82 StartZ=0 EndX=97.5 EndY=109.424 EndZ=0
    g5: LineSegment StartX=97.5 StartY=109.424 StartZ=0 EndX=97.5 EndY=105.424 EndZ=0
    g6: LineSegment StartX=97.5 StartY=105.424 StartZ=0 EndX=50 EndY=78 EndZ=0
    g7: LineSegment StartX=50 StartY=82 StartZ=0 EndX=50 EndY=78 EndZ=0
    g8: LineSegment StartX=75 StartY=116.424 StartZ=0 EndX=137.5 EndY=152.509 EndZ=0
    g9: LineSegment StartX=137.5 StartY=148.509 StartZ=0 EndX=75 EndY=112.424 EndZ=0
    g10: LineSegment StartX=75 StartY=112.424 StartZ=0 EndX=75 EndY=116.424 EndZ=0
    g11: LineSegment StartX=137.5 StartY=152.509 StartZ=0 EndX=200 EndY=116.424 EndZ=0
    g12: LineSegment StartX=200 StartY=116.424 StartZ=0 EndX=200 EndY=112.424 EndZ=0
    g13: LineSegment StartX=200 StartY=112.424 StartZ=0 EndX=137.5 EndY=148.509 EndZ=0
    g14: LineSegment StartX=177.5 StartY=109.424 StartZ=0 EndX=225 EndY=82 EndZ=0
    g15: LineSegment StartX=225 StartY=82 StartZ=0 EndX=225 EndY=78 EndZ=0
    g16: LineSegment StartX=225 StartY=78 StartZ=0 EndX=177.5 EndY=105.424 EndZ=0
    g17: LineSegment StartX=177.5 StartY=105.424 StartZ=0 EndX=177.5 EndY=109.424 EndZ=0
    g18: LineSegment StartX=177.5 StartY=101.424 StartZ=0 EndX=225 EndY=74 EndZ=0
    g19: LineSegment StartX=225 StartY=74 StartZ=0 EndX=225 EndY=70 EndZ=0
    g20: LineSegment StartX=225 StartY=70 StartZ=0 EndX=177.5 EndY=97.4241 EndZ=0
    g21: LineSegment StartX=177.5 StartY=101.424 StartZ=0 EndX=177.5 EndY=97.4241 EndZ=0
    g22: LineSegment StartX=75 StartY=120.424 StartZ=0 EndX=137.5 EndY=156.509 EndZ=0
    g23: LineSegment StartX=137.5 StartY=156.509 StartZ=0 EndX=200 EndY=120.424 EndZ=0
    g24: LineSegment StartX=200 StartY=120.424 StartZ=0 EndX=200 EndY=124.424 EndZ=0
    g25: LineSegment StartX=200 StartY=124.424 StartZ=0 EndX=137.5 EndY=160.509 EndZ=0
    g26: LineSegment StartX=137.5 StartY=160.509 StartZ=0 EndX=75 EndY=124.424 EndZ=0
    g27: LineSegment StartX=75 StartY=124.424 StartZ=0 EndX=75 EndY=120.424 EndZ=0
  constraints (84):
    c: Angle(g0) = 0.523599
    c: DistanceX(g0) = 50
    c: Coincident(g1,g0)
    c: Vertical(g1)
    c: Coincident(g2,g1)
    c: Coincident(g3,g2)
    c: Vertical(g3)
    c: DistanceY(g0,g2) = 4
    c: Parallel(g0,g2)
    c: Coincident(g0,g3)
    c: Coincident(g5,g4)
    c: Coincident(g7,g4)
    c: Coincident(g7,g6)
    c: Vertical(g7)
    c: Vertical(g5)
    c: Coincident(g5,g6)
    c: Parallel(g2,g6)
    c: Parallel(g6,g4)
    c: DistanceX(g6,g2) = 0
    c: DistanceY(g2,g6) = 4
    c: DistanceY(g6,g4) = 4
    c: DistanceX(g5,g1) = 0
    c: DistanceY(g0) = 70
    c: Coincident(g10,g9)
    c: Coincident(g10,g8)
    c: Vertical(g10)
    c: DistanceY(g9,g8) = 4
    c: Parallel(g8,g9)
    c: DistanceX(g9,g9) = 62.5
    c: Coincident(g11,g8)
    c: Coincident(g12,g11)
    c: Coincident(g13,g12)
    c: Coincident(g13,g9)
    c: Parallel(g13,g11)
    c: Vertical(g12)
    c: Coincident(g15,g14)
    c: Vertical(g15)
    c: Coincident(g17,g16)
    c: Coincident(g17,g14)
    c: Coincident(g19,g18)
    c: Vertical(g19)
    c: Coincident(g20,g19)
    c: Coincident(g21,g18)
    c: Coincident(g21,g20)
    c: Vertical(g21)
    c: Vertical(g17)
    c: DistanceX(g18,g16) = 0
    c: DistanceY(g16,g14) = 4
    c: DistanceY(g18,g16) = 4
    c: DistanceY(g20,g18) = 4
    c: Parallel(g20,g18)
    c: Parallel(g18,g16)
    c: Parallel(g16,g14)
    c: Coincident(g15,g16)
    c: DistanceY(g19,g0) = 0
    c: DistanceX(g18,g15) = 0
    c: DistanceY(g4,g9) = 3
    c: DistanceY(g4,g14) = 0
    c: DistanceY(g9,g12) = 0
    c: DistanceX(g9,g8) = 0
    c: Angle(g9) = -2.61799
    c: DistanceX(g9,g4) = 22.5
    c: DistanceX(g14,g12) = 22.5
    c: DistanceX(g9,g14) = 87.5
    c: DistanceX(g8) = 137.5
    c: DistanceX(g9,g12) = 125
    c: Coincident(g23,g22)
    c: Coincident(g24,g23)
    c: Vertical(g24)
    c: Coincident(g26,g25)
    c: Coincident(g27,g22)
    c: Vertical(g27)
    c: DistanceX(g22,g8) = 0
    c: DistanceX(g8,g22) = 0
    c: DistanceX(g25,g22) = 0
    c: Coincident(g24,g25)
    c: Coincident(g26,g27)
    c: DistanceY(g8,g22) = 4
    c: DistanceY(g22,g25) = 4
    c: DistanceY(g11,g23) = 4
    c: DistanceY(g23,g24) = 4
    c: DistanceX(g23,g11) = 0
    c: DistanceY(g8,g22) = 4
    c: DistanceY(g22,g26) = 4
FEATURE [Part::Extrusion] Extrude012  label="cuts"
  Base = -> Sketch039
  Dir = (0,-1,2e-16)
  DirMode = 2
  FaceMakerClass = Part::FaceMakerBullseye
  LengthFwd = 275
  LengthRev = 0
  Reversed = true
  Solid = true
  Symmetric = false
FEATURE [Sketcher::SketchObject] Sketch040
  FullyConstrained = true
  Placement = pos=(0,0,0) rot=(1,0,0;1.5708rad)
  sketch-geometry (28):
    g0: LineSegment StartX=50 StartY=70 StartZ=0 EndX=97.5 EndY=97.4241 EndZ=0
    g1: LineSegment StartX=97.5 StartY=97.4241 StartZ=0 EndX=97.5 EndY=101.424 EndZ=0
    g2: LineSegment StartX=97.5 StartY=101.424 StartZ=0 EndX=50 EndY=74 EndZ=0
    g3: LineSegment StartX=50 StartY=74 StartZ=0 EndX=50 EndY=70 EndZ=0
    g4: LineSegment StartX=50 StartY=82 StartZ=0 EndX=97.5 EndY=109.424 EndZ=0
    g5: LineSegment StartX=97.5 StartY=109.424 StartZ=0 EndX=97.5 EndY=105.424 EndZ=0
    g6: LineSegment StartX=97.5 StartY=105.424 StartZ=0 EndX=50 EndY=78 EndZ=0
    g7: LineSegment StartX=50 StartY=82 StartZ=0 EndX=50 EndY=78 EndZ=0
    g8: LineSegment StartX=75 StartY=116.424 StartZ=0 EndX=137.5 EndY=152.509 EndZ=0
    g9: LineSegment StartX=137.5 StartY=148.509 StartZ=0 EndX=75 EndY=112.424 EndZ=0
    g10: LineSegment StartX=75 StartY=112.424 StartZ=0 EndX=75 EndY=116.424 EndZ=0
    g11: LineSegment StartX=137.5 StartY=152.509 StartZ=0 EndX=200 EndY=116.424 EndZ=0
    g12: LineSegment StartX=200 StartY=116.424 StartZ=0 EndX=200 EndY=112.424 EndZ=0
    g13: LineSegment StartX=200 StartY=112.424 StartZ=0 EndX=137.5 EndY=148.509 EndZ=0
    g14: LineSegment StartX=177.5 StartY=109.424 StartZ=0 EndX=225 EndY=82 EndZ=0
    g15: LineSegment StartX=225 StartY=82 StartZ=0 EndX=225 EndY=78 EndZ=0
    g16: LineSegment StartX=225 StartY=78 StartZ=0 EndX=177.5 EndY=105.424 EndZ=0
    g17: LineSegment StartX=177.5 StartY=105.424 StartZ=0 EndX=177.5 EndY=109.424 EndZ=0
    g18: LineSegment StartX=177.5 StartY=101.424 StartZ=0 EndX=225 EndY=74 EndZ=0
    g19: LineSegment StartX=225 StartY=74 StartZ=0 EndX=225 EndY=70 EndZ=0
    g20: LineSegment StartX=225 StartY=70 StartZ=0 EndX=177.5 EndY=97.4241 EndZ=0
    g21: LineSegment StartX=177.5 StartY=101.424 StartZ=0 EndX=177.5 EndY=97.4241 EndZ=0
    g22: LineSegment StartX=75 StartY=120.424 StartZ=0 EndX=75 EndY=124.424 EndZ=0
    g23: LineSegment StartX=75 StartY=124.424 StartZ=0 EndX=137.5 EndY=160.509 EndZ=0
    g24: LineSegment StartX=137.5 StartY=160.509 StartZ=0 EndX=200 EndY=124.424 EndZ=0
    g25: LineSegment StartX=200 StartY=124.424 StartZ=0 EndX=200 EndY=120.424 EndZ=0
    g26: LineSegment StartX=200 StartY=120.424 StartZ=0 EndX=137.5 EndY=156.509 EndZ=0
    g27: LineSegment StartX=137.5 StartY=156.509 StartZ=0 EndX=75 EndY=120.424 EndZ=0
  constraints (84):
    c: Angle(g0) = 0.523599
    c: DistanceX(g0) = 50
    c: Coincident(g1,g0)
    c: Vertical(g1)
    c: Coincident(g2,g1)
    c: Coincident(g3,g2)
    c: Vertical(g3)
    c: DistanceY(g0,g2) = 4
    c: Parallel(g0,g2)
    c: Coincident(g0,g3)
    c: Coincident(g5,g4)
    c: Coincident(g7,g4)
    c: Coincident(g7,g6)
    c: Vertical(g7)
    c: Vertical(g5)
    c: Coincident(g5,g6)
    c: Parallel(g2,g6)
    c: Parallel(g6,g4)
    c: DistanceX(g6,g2) = 0
    c: DistanceY(g2,g6) = 4
    c: DistanceY(g6,g4) = 4
    c: DistanceX(g5,g1) = 0
    c: DistanceY(g0) = 70
    c: Coincident(g10,g9)
    c: Coincident(g10,g8)
    c: Vertical(g10)
    c: DistanceY(g9,g8) = 4
    c: Parallel(g8,g9)
    c: DistanceX(g9,g9) = 62.5
    c: Coincident(g11,g8)
    c: Coincident(g12,g11)
    c: Coincident(g13,g12)
    c: Coincident(g13,g9)
    c: Parallel(g13,g11)
    c: Vertical(g12)
    c: Coincident(g15,g14)
    c: Vertical(g15)
    c: Coincident(g17,g16)
    c: Coincident(g17,g14)
    c: Coincident(g19,g18)
    c: Vertical(g19)
    c: Coincident(g20,g19)
    c: Coincident(g21,g18)
    c: Coincident(g21,g20)
    c: Vertical(g21)
    c: Vertical(g17)
    c: DistanceX(g18,g16) = 0
    c: DistanceY(g16,g14) = 4
    c: DistanceY(g18,g16) = 4
    c: DistanceY(g20,g18) = 4
    c: Parallel(g20,g18)
    c: Parallel(g18,g16)
    c: Parallel(g16,g14)
    c: Coincident(g15,g16)
    c: DistanceY(g19,g0) = 0
    c: DistanceX(g18,g15) = 0
    c: DistanceX(g14,g14) = 47.5
    c: DistanceX(g4,g4) = 47.5
    c: DistanceX(g4,g14) = 80
    c: Parallel(g9,g4)
    c: DistanceX(g9,g8) = 0
    c: DistanceY(g4,g9) = 3
    c: DistanceY(g14,g12) = 3
    c: DistanceY(g14,g4) = 0
    c: DistanceX(g8) = 137.5
    c: DistanceX(g9,g12) = 125
    c: Vertical(g22)
    c: Coincident(g23,g22)
    c: Coincident(g24,g23)
    c: Coincident(g25,g24)
    c: Vertical(g25)
    c: Coincident(g26,g25)
    c: Coincident(g27,g22)
    c: DistanceX(g22,g8) = 0
    c: DistanceY(g8,g22) = 4
    c: DistanceY(g22,g22) = 4
    c: Coincident(g26,g27)
    c: DistanceX(g26,g8) = 0
    c: DistanceY(g26,g23) = 4
    c: DistanceY(g8,g26) = 4
    c: DistanceX(g23,g26) = 0
    c: DistanceX(g25,g11) = 0
    c: DistanceY(g11,g25) = 4
    c: DistanceY(g25,g24) = 4
FEATURE [Part::Extrusion] Extrude013  label="cuts001"
  Base = -> Sketch040
  Dir = (0,-1,2e-16)
  DirMode = 2
  FaceMakerClass = Part::FaceMakerBullseye
  LengthFwd = 275
  LengthRev = 0
  Placement = pos=(275,0,0) rot=(0,0,1;1.5708rad)
  Reversed = true
  Solid = true
  Symmetric = false
FEATURE [Sketcher::SketchObject] Sketch041
  FullyConstrained = true
  sketch-geometry (4):
    g0: LineSegment StartX=0 StartY=275 StartZ=0 EndX=275 EndY=275 EndZ=0
    g1: LineSegment StartX=275 StartY=275 StartZ=0 EndX=275 EndY=0 EndZ=0
    g2: LineSegment StartX=275 StartY=0 StartZ=0 EndX=0 EndY=0 EndZ=0
    g3: LineSegment StartX=0 StartY=0 StartZ=0 EndX=0 EndY=275 EndZ=0
  constraints (11):
    c: Coincident(g0,g1)
    c: Coincident(g1,g2)
    c: Coincident(g2,g3)
    c: Coincident(g3,g0)
    c: Horizontal(g0)
    c: Horizontal(g2)
    c: Vertical(g1)
    c: Vertical(g3)
    c: Coincident(g2,g-1)
    c: DistanceX(g2,g2) = 275
    c: DistanceY(g3,g3) = 275
FEATURE [Sketcher::SketchObject] Sketch042
  FullyConstrained = true
  Placement = pos=(0,0,175.1) rot=(0,0,1;0rad)
  sketch-geometry (5):
    g0: GeomPoint X=137.5 Y=137.5 Z=0
    g1: LineSegment StartX=137.55 StartY=137.55 StartZ=0 EndX=137.55 EndY=137.45 EndZ=0
    g2: LineSegment StartX=137.55 StartY=137.45 StartZ=0 EndX=137.45 EndY=137.45 EndZ=0
    g3: LineSegment StartX=137.45 StartY=137.45 StartZ=0 EndX=137.45 EndY=137.55 EndZ=0
    g4: LineSegment StartX=137.45 StartY=137.55 StartZ=0 EndX=137.55 EndY=137.55 EndZ=0
  constraints (14):
    c: Coincident(g1,g2)
    c: Horizontal(g2)
    c: Vertical(g1)
    c: DistanceX(g2,g2) = 0.1
    c: DistanceX(g2,g0) = 0.05
    c: DistanceY(g1,g1) = 0.1
    c: DistanceY(g1,g0) = -0.05
    c: DistanceX(g0) = 137.5
    c: DistanceY(g0) = 137.5
    c: Coincident(g3,g2)
    c: Vertical(g3)
    c: Coincident(g4,g3)
    c: Coincident(g4,g1)
    c: Horizontal(g4)
FEATURE [Part::Loft] Loft006  label="outerLayer006"
  Closed = false
  MaxDegree = 5
  Ruled = false
  Sections = -> [Sketch041,Sketch042]
  Solid = true
FEATURE [Sketcher::SketchObject] Sketch043
  FullyConstrained = true
  sketch-geometry (4):
    g0: LineSegment StartX=0 StartY=275 StartZ=0 EndX=275 EndY=275 EndZ=0
    g1: LineSegment StartX=275 StartY=275 StartZ=0 EndX=275 EndY=0 EndZ=0
    g2: LineSegment StartX=275 StartY=0 StartZ=0 EndX=0 EndY=0 EndZ=0
    g3: LineSegment StartX=0 StartY=0 StartZ=0 EndX=0 EndY=275 EndZ=0
  constraints (11):
    c: Coincident(g0,g1)
    c: Coincident(g1,g2)
    c: Coincident(g2,g3)
    c: Coincident(g3,g0)
    c: Horizontal(g0)
    c: Horizontal(g2)
    c: Vertical(g1)
    c: Vertical(g3)
    c: Coincident(g2,g-1)
    c: DistanceX(g2,g2) = 275
    c: DistanceY(g3,g3) = 275
FEATURE [Sketcher::SketchObject] Sketch044
  FullyConstrained = true
  Placement = pos=(0,0,175.1) rot=(0,0,1;0rad)
  sketch-geometry (5):
    g0: GeomPoint X=137.5 Y=137.5 Z=0
    g1: LineSegment StartX=137.55 StartY=137.55 StartZ=0 EndX=137.55 EndY=137.45 EndZ=0
    g2: LineSegment StartX=137.55 StartY=137.45 StartZ=0 EndX=137.45 EndY=137.45 EndZ=0
    g3: LineSegment StartX=137.45 StartY=137.45 StartZ=0 EndX=137.45 EndY=137.55 EndZ=0
    g4: LineSegment StartX=137.45 StartY=137.55 StartZ=0 EndX=137.55 EndY=137.55 EndZ=0
  constraints (14):
    c: Coincident(g1,g2)
    c: Horizontal(g2)
    c: Vertical(g1)
    c: DistanceX(g2,g2) = 0.1
    c: DistanceX(g2,g0) = 0.05
    c: DistanceY(g1,g1) = 0.1
    c: DistanceY(g1,g0) = -0.05
    c: DistanceX(g0) = 137.5
    c: DistanceY(g0) = 137.5
    c: Coincident(g3,g2)
    c: Vertical(g3)
    c: Coincident(g4,g3)
    c: Coincident(g4,g1)
    c: Horizontal(g4)
FEATURE [Part::Loft] Loft007  label="outerLayer007"
  Closed = false
  MaxDegree = 5
  Placement = pos=(0,0,-8) rot=(0,0,1;0rad)
  Ruled = false
  Sections = -> [Sketch043,Sketch044]
  Solid = true
FEATURE [Part::Cut] Cut004  label="Shell001"
  Base = -> Loft006
  Tool = -> Loft007
FEATURE [Sketcher::SketchObject] Sketch045
  FullyConstrained = true
  Placement = pos=(0,0,0) rot=(1,0,0;1.5708rad)
  sketch-geometry (3):
    g0: LineSegment StartX=15 StartY=0 StartZ=0 EndX=260 EndY=0 EndZ=0
    g1: LineSegment StartX=260 StartY=0 StartZ=0 EndX=137.5 EndY=160 EndZ=0
    g2: LineSegment StartX=137.5 StartY=160 StartZ=0 EndX=15 EndY=0 EndZ=0
  constraints (9):
    c: Horizontal(g0)
    c: Coincident(g1,g0)
    c: Coincident(g2,g1)
    c: DistanceX(g0) = 260
    c: DistanceX(g1) = 137.5
    c: DistanceY(g1) = 160
    c: Coincident(g0,g2)
    c: DistanceY(g0,g-1) = 0
    c: DistanceX(g-1,g0) = 15
FEATURE [Part::Extrusion] Extrude014
  Base = -> Sketch045
  Dir = (0,-1,-6e-16)
  DirMode = 2
  FaceMakerClass = Part::FaceMakerBullseye
  LengthFwd = 275
  LengthRev = 0
  Placement = pos=(0,0,0) rot=(0,0,1;1.5708rad)
  Solid = true
  Symmetric = false
FEATURE [Sketcher::SketchObject] Sketch046
  FullyConstrained = true
  Placement = pos=(0,0,0) rot=(1,0,0;1.5708rad)
  sketch-geometry (3):
    g0: LineSegment StartX=15 StartY=0 StartZ=0 EndX=260 EndY=0 EndZ=0
    g1: LineSegment StartX=260 StartY=0 StartZ=0 EndX=137.5 EndY=160 EndZ=0
    g2: LineSegment StartX=137.5 StartY=160 StartZ=0 EndX=15 EndY=0 EndZ=0
  constraints (9):
    c: Horizontal(g0)
    c: Coincident(g1,g0)
    c: Coincident(g2,g1)
    c: DistanceX(g0) = 260
    c: DistanceX(g1) = 137.5
    c: DistanceY(g1) = 160
    c: Coincident(g0,g2)
    c: DistanceY(g0,g-1) = 0
    c: DistanceX(g-1,g0) = 15
FEATURE [Part::Extrusion] Extrude015
  Base = -> Sketch046
  Dir = (0,-1,2e-16)
  DirMode = 2
  FaceMakerClass = Part::FaceMakerBullseye
  LengthFwd = 275
  LengthRev = 0
  Reversed = true
  Solid = true
  Symmetric = false
FEATURE [Part::MultiCommon] Common003  label="cuts002"
  Shapes = -> [Extrude014,Extrude012]
FEATURE [Part::MultiCommon] Common004  label="cuts003"
  Shapes = -> [Extrude015,Extrude013]
FEATURE [Part::MultiFuse] Fusion059  label="cuts004"
  Shapes = -> [Common004,Common003]
FEATURE [Sketcher::SketchObject] Sketch047
  FullyConstrained = true
  Placement = pos=(0,0,0) rot=(1,0,0;1.5708rad)
  sketch-geometry (28):
    g0: LineSegment StartX=50 StartY=70 StartZ=0 EndX=97.5 EndY=97.4241 EndZ=0
    g1: LineSegment StartX=97.5 StartY=97.4241 StartZ=0 EndX=97.5 EndY=101.424 EndZ=0
    g2: LineSegment StartX=97.5 StartY=101.424 StartZ=0 EndX=50 EndY=74 EndZ=0
    g3: LineSegment StartX=50 StartY=74 StartZ=0 EndX=50 EndY=70 EndZ=0
    g4: LineSegment StartX=50 StartY=82 StartZ=0 EndX=97.5 EndY=109.424 EndZ=0
    g5: LineSegment StartX=97.5 StartY=109.424 StartZ=0 EndX=97.5 EndY=105.424 EndZ=0
    g6: LineSegment StartX=97.5 StartY=105.424 StartZ=0 EndX=50 EndY=78 EndZ=0
    g7: LineSegment StartX=50 StartY=82 StartZ=0 EndX=50 EndY=78 EndZ=0
    g8: LineSegment StartX=75 StartY=116.424 StartZ=0 EndX=137.5 EndY=152.509 EndZ=0
    g9: LineSegment StartX=137.5 StartY=148.509 StartZ=0 EndX=75 EndY=112.424 EndZ=0
    g10: LineSegment StartX=75 StartY=112.424 StartZ=0 EndX=75 EndY=116.424 EndZ=0
    g11: LineSegment StartX=137.5 StartY=152.509 StartZ=0 EndX=200 EndY=116.424 EndZ=0
    g12: LineSegment StartX=200 StartY=116.424 StartZ=0 EndX=200 EndY=112.424 EndZ=0
    g13: LineSegment StartX=200 StartY=112.424 StartZ=0 EndX=137.5 EndY=148.509 EndZ=0
    g14: LineSegment StartX=177.5 StartY=109.424 StartZ=0 EndX=225 EndY=82 EndZ=0
    g15: LineSegment StartX=225 StartY=82 StartZ=0 EndX=225 EndY=78 EndZ=0
    g16: LineSegment StartX=225 StartY=78 StartZ=0 EndX=177.5 EndY=105.424 EndZ=0
    g17: LineSegment StartX=177.5 StartY=105.424 StartZ=0 EndX=177.5 EndY=109.424 EndZ=0
    g18: LineSegment StartX=177.5 StartY=101.424 StartZ=0 EndX=225 EndY=74 EndZ=0
    g19: LineSegment StartX=225 StartY=74 StartZ=0 EndX=225 EndY=70 EndZ=0
    g20: LineSegment StartX=225 StartY=70 StartZ=0 EndX=177.5 EndY=97.4241 EndZ=0
    g21: LineSegment StartX=177.5 StartY=101.424 StartZ=0 EndX=177.5 EndY=97.4241 EndZ=0
    g22: LineSegment StartX=75 StartY=120.424 StartZ=0 EndX=137.5 EndY=156.509 EndZ=0
    g23: LineSegment StartX=137.5 StartY=156.509 StartZ=0 EndX=200 EndY=120.424 EndZ=0
    g24: LineSegment StartX=200 StartY=120.424 StartZ=0 EndX=200 EndY=124.424 EndZ=0
    g25: LineSegment StartX=200 StartY=124.424 StartZ=0 EndX=137.5 EndY=160.509 EndZ=0
    g26: LineSegment StartX=137.5 StartY=160.509 StartZ=0 EndX=75 EndY=124.424 EndZ=0
    g27: LineSegment StartX=75 StartY=124.424 StartZ=0 EndX=75 EndY=120.424 EndZ=0
  constraints (84):
    c: Angle(g0) = 0.523599
    c: DistanceX(g0) = 50
    c: Coincident(g1,g0)
    c: Vertical(g1)
    c: Coincident(g2,g1)
    c: Coincident(g3,g2)
    c: Vertical(g3)
    c: DistanceY(g0,g2) = 4
    c: Parallel(g0,g2)
    c: Coincident(g0,g3)
    c: Coincident(g5,g4)
    c: Coincident(g7,g4)
    c: Coincident(g7,g6)
    c: Vertical(g7)
    c: Vertical(g5)
    c: Coincident(g5,g6)
    c: Parallel(g2,g6)
    c: Parallel(g6,g4)
    c: DistanceX(g6,g2) = 0
    c: DistanceY(g2,g6) = 4
    c: DistanceY(g6,g4) = 4
    c: DistanceX(g5,g1) = 0
    c: DistanceY(g0) = 70
    c: Coincident(g10,g9)
    c: Coincident(g10,g8)
    c: Vertical(g10)
    c: DistanceY(g9,g8) = 4
    c: Parallel(g8,g9)
    c: DistanceX(g9,g9) = 62.5
    c: Coincident(g11,g8)
    c: Coincident(g12,g11)
    c: Coincident(g13,g12)
    c: Coincident(g13,g9)
    c: Parallel(g13,g11)
    c: Vertical(g12)
    c: Coincident(g15,g14)
    c: Vertical(g15)
    c: Coincident(g17,g16)
    c: Coincident(g17,g14)
    c: Coincident(g19,g18)
    c: Vertical(g19)
    c: Coincident(g20,g19)
    c: Coincident(g21,g18)
    c: Coincident(g21,g20)
    c: Vertical(g21)
    c: Vertical(g17)
    c: DistanceX(g18,g16) = 0
    c: DistanceY(g16,g14) = 4
    c: DistanceY(g18,g16) = 4
    c: DistanceY(g20,g18) = 4
    c: Parallel(g20,g18)
    c: Parallel(g18,g16)
    c: Parallel(g16,g14)
    c: Coincident(g15,g16)
    c: DistanceY(g19,g0) = 0
    c: DistanceX(g18,g15) = 0
    c: DistanceY(g4,g9) = 3
    c: DistanceY(g4,g14) = 0
    c: DistanceY(g9,g12) = 0
    c: DistanceX(g9,g8) = 0
    c: Angle(g9) = -2.61799
    c: DistanceX(g9,g4) = 22.5
    c: DistanceX(g14,g12) = 22.5
    c: DistanceX(g9,g14) = 87.5
    c: DistanceX(g8) = 137.5
    c: DistanceX(g9,g12) = 125
    c: Coincident(g23,g22)
    c: Coincident(g24,g23)
    c: Vertical(g24)
    c: Coincident(g26,g25)
    c: Coincident(g27,g22)
    c: Vertical(g27)
    c: DistanceX(g22,g8) = 0
    c: DistanceX(g8,g22) = 0
    c: DistanceX(g25,g22) = 0
    c: Coincident(g24,g25)
    c: Coincident(g26,g27)
    c: DistanceY(g8,g22) = 4
    c: DistanceY(g22,g25) = 4
    c: DistanceY(g11,g23) = 4
    c: DistanceY(g23,g24) = 4
    c: DistanceX(g23,g11) = 0
    c: DistanceY(g8,g22) = 4
    c: DistanceY(g22,g26) = 4
FEATURE [Part::Extrusion] Extrude016  label="cuts007"
  Base = -> Sketch047
  Dir = (0,-1,2e-16)
  DirMode = 2
  FaceMakerClass = Part::FaceMakerBullseye
  LengthFwd = 275
  LengthRev = 0
  Reversed = true
  Solid = true
  Symmetric = false
FEATURE [Sketcher::SketchObject] Sketch048
  FullyConstrained = true
  Placement = pos=(0,0,0) rot=(1,0,0;1.5708rad)
  sketch-geometry (28):
    g0: LineSegment StartX=50 StartY=70 StartZ=0 EndX=97.5 EndY=97.4241 EndZ=0
    g1: LineSegment StartX=97.5 StartY=97.4241 StartZ=0 EndX=97.5 EndY=101.424 EndZ=0
    g2: LineSegment StartX=97.5 StartY=101.424 StartZ=0 EndX=50 EndY=74 EndZ=0
    g3: LineSegment StartX=50 StartY=74 StartZ=0 EndX=50 EndY=70 EndZ=0
    g4: LineSegment StartX=50 StartY=82 StartZ=0 EndX=97.5 EndY=109.424 EndZ=0
    g5: LineSegment StartX=97.5 StartY=109.424 StartZ=0 EndX=97.5 EndY=105.424 EndZ=0
    g6: LineSegment StartX=97.5 StartY=105.424 StartZ=0 EndX=50 EndY=78 EndZ=0
    g7: LineSegment StartX=50 StartY=82 StartZ=0 EndX=50 EndY=78 EndZ=0
    g8: LineSegment StartX=75 StartY=116.424 StartZ=0 EndX=137.5 EndY=152.509 EndZ=0
    g9: LineSegment StartX=137.5 StartY=148.509 StartZ=0 EndX=75 EndY=112.424 EndZ=0
    g10: LineSegment StartX=75 StartY=112.424 StartZ=0 EndX=75 EndY=116.424 EndZ=0
    g11: LineSegment StartX=137.5 StartY=152.509 StartZ=0 EndX=200 EndY=116.424 EndZ=0
    g12: LineSegment StartX=200 StartY=116.424 StartZ=0 EndX=200 EndY=112.424 EndZ=0
    g13: LineSegment StartX=200 StartY=112.424 StartZ=0 EndX=137.5 EndY=148.509 EndZ=0
    g14: LineSegment StartX=177.5 StartY=109.424 StartZ=0 EndX=225 EndY=82 EndZ=0
    g15: LineSegment StartX=225 StartY=82 StartZ=0 EndX=225 EndY=78 EndZ=0
    g16: LineSegment StartX=225 StartY=78 StartZ=0 EndX=177.5 EndY=105.424 EndZ=0
    g17: LineSegment StartX=177.5 StartY=105.424 StartZ=0 EndX=177.5 EndY=109.424 EndZ=0
    g18: LineSegment StartX=177.5 StartY=101.424 StartZ=0 EndX=225 EndY=74 EndZ=0
    g19: LineSegment StartX=225 StartY=74 StartZ=0 EndX=225 EndY=70 EndZ=0
    g20: LineSegment StartX=225 StartY=70 StartZ=0 EndX=177.5 EndY=97.4241 EndZ=0
    g21: LineSegment StartX=177.5 StartY=101.424 StartZ=0 EndX=177.5 EndY=97.4241 EndZ=0
    g22: LineSegment StartX=75 StartY=120.424 StartZ=0 EndX=75 EndY=124.424 EndZ=0
    g23: LineSegment StartX=75 StartY=124.424 StartZ=0 EndX=137.5 EndY=160.509 EndZ=0
    g24: LineSegment StartX=137.5 StartY=160.509 StartZ=0 EndX=200 EndY=124.424 EndZ=0
    g25: LineSegment StartX=200 StartY=124.424 StartZ=0 EndX=200 EndY=120.424 EndZ=0
    g26: LineSegment StartX=200 StartY=120.424 StartZ=0 EndX=137.5 EndY=156.509 EndZ=0
    g27: LineSegment StartX=137.5 StartY=156.509 StartZ=0 EndX=75 EndY=120.424 EndZ=0
  constraints (84):
    c: Angle(g0) = 0.523599
    c: DistanceX(g0) = 50
    c: Coincident(g1,g0)
    c: Vertical(g1)
    c: Coincident(g2,g1)
    c: Coincident(g3,g2)
    c: Vertical(g3)
    c: DistanceY(g0,g2) = 4
    c: Parallel(g0,g2)
    c: Coincident(g0,g3)
    c: Coincident(g5,g4)
    c: Coincident(g7,g4)
    c: Coincident(g7,g6)
    c: Vertical(g7)
    c: Vertical(g5)
    c: Coincident(g5,g6)
    c: Parallel(g2,g6)
    c: Parallel(g6,g4)
    c: DistanceX(g6,g2) = 0
    c: DistanceY(g2,g6) = 4
    c: DistanceY(g6,g4) = 4
    c: DistanceX(g5,g1) = 0
    c: DistanceY(g0) = 70
    c: Coincident(g10,g9)
    c: Coincident(g10,g8)
    c: Vertical(g10)
    c: DistanceY(g9,g8) = 4
    c: Parallel(g8,g9)
    c: DistanceX(g9,g9) = 62.5
    c: Coincident(g11,g8)
    c: Coincident(g12,g11)
    c: Coincident(g13,g12)
    c: Coincident(g13,g9)
    c: Parallel(g13,g11)
    c: Vertical(g12)
    c: Coincident(g15,g14)
    c: Vertical(g15)
    c: Coincident(g17,g16)
    c: Coincident(g17,g14)
    c: Coincident(g19,g18)
    c: Vertical(g19)
    c: Coincident(g20,g19)
    c: Coincident(g21,g18)
    c: Coincident(g21,g20)
    c: Vertical(g21)
    c: Vertical(g17)
    c: DistanceX(g18,g16) = 0
    c: DistanceY(g16,g14) = 4
    c: DistanceY(g18,g16) = 4
    c: DistanceY(g20,g18) = 4
    c: Parallel(g20,g18)
    c: Parallel(g18,g16)
    c: Parallel(g16,g14)
    c: Coincident(g15,g16)
    c: DistanceY(g19,g0) = 0
    c: DistanceX(g18,g15) = 0
    c: DistanceX(g14,g14) = 47.5
    c: DistanceX(g4,g4) = 47.5
    c: DistanceX(g4,g14) = 80
    c: Parallel(g9,g4)
    c: DistanceX(g9,g8) = 0
    c: DistanceY(g4,g9) = 3
    c: DistanceY(g14,g12) = 3
    c: DistanceY(g14,g4) = 0
    c: DistanceX(g8) = 137.5
    c: DistanceX(g9,g12) = 125
    c: Vertical(g22)
    c: Coincident(g23,g22)
    c: Coincident(g24,g23)
    c: Coincident(g25,g24)
    c: Vertical(g25)
    c: Coincident(g26,g25)
    c: Coincident(g27,g22)
    c: DistanceX(g22,g8) = 0
    c: DistanceY(g8,g22) = 4
    c: DistanceY(g22,g22) = 4
    c: Coincident(g26,g27)
    c: DistanceX(g26,g8) = 0
    c: DistanceY(g26,g23) = 4
    c: DistanceY(g8,g26) = 4
    c: DistanceX(g23,g26) = 0
    c: DistanceX(g25,g11) = 0
    c: DistanceY(g11,g25) = 4
    c: DistanceY(g25,g24) = 4
FEATURE [Part::Extrusion] Extrude017  label="cuts008"
  Base = -> Sketch048
  Dir = (0,-1,2e-16)
  DirMode = 2
  FaceMakerClass = Part::FaceMakerBullseye
  LengthFwd = 275
  LengthRev = 0
  Placement = pos=(275,0,0) rot=(0,0,1;1.5708rad)
  Reversed = true
  Solid = true
  Symmetric = false
FEATURE [Sketcher::SketchObject] Sketch049
  FullyConstrained = true
  Placement = pos=(0,0,0) rot=(1,0,0;1.5708rad)
  sketch-geometry (3):
    g0: LineSegment StartX=15 StartY=0 StartZ=0 EndX=260 EndY=0 EndZ=0
    g1: LineSegment StartX=260 StartY=0 StartZ=0 EndX=137.5 EndY=160 EndZ=0
    g2: LineSegment StartX=137.5 StartY=160 StartZ=0 EndX=15 EndY=0 EndZ=0
  constraints (9):
    c: Horizontal(g0)
    c: Coincident(g1,g0)
    c: Coincident(g2,g1)
    c: DistanceX(g0) = 260
    c: DistanceX(g1) = 137.5
    c: DistanceY(g1) = 160
    c: Coincident(g0,g2)
    c: DistanceY(g0,g-1) = 0
    c: DistanceX(g-1,g0) = 15
FEATURE [Part::Extrusion] Extrude018
  Base = -> Sketch049
  Dir = (0,-1,-6e-16)
  DirMode = 2
  FaceMakerClass = Part::FaceMakerBullseye
  LengthFwd = 275
  LengthRev = 0
  Placement = pos=(0,0,0) rot=(0,0,1;1.5708rad)
  Solid = true
  Symmetric = false
FEATURE [Part::MultiCommon] Common005  label="cuts005"
  Shapes = -> [Extrude018,Extrude016]
FEATURE [Sketcher::SketchObject] Sketch050
  FullyConstrained = true
  Placement = pos=(0,0,0) rot=(1,0,0;1.5708rad)
  sketch-geometry (3):
    g0: LineSegment StartX=15 StartY=0 StartZ=0 EndX=260 EndY=0 EndZ=0
    g1: LineSegment StartX=260 StartY=0 StartZ=0 EndX=137.5 EndY=160 EndZ=0
    g2: LineSegment StartX=137.5 StartY=160 StartZ=0 EndX=15 EndY=0 EndZ=0
  constraints (9):
    c: Horizontal(g0)
    c: Coincident(g1,g0)
    c: Coincident(g2,g1)
    c: DistanceX(g0) = 260
    c: DistanceX(g1) = 137.5
    c: DistanceY(g1) = 160
    c: Coincident(g0,g2)
    c: DistanceY(g0,g-1) = 0
    c: DistanceX(g-1,g0) = 15
FEATURE [Part::Extrusion] Extrude019
  Base = -> Sketch050
  Dir = (0,-1,2e-16)
  DirMode = 2
  FaceMakerClass = Part::FaceMakerBullseye
  LengthFwd = 275
  LengthRev = 0
  Reversed = true
  Solid = true
  Symmetric = false
FEATURE [Part::MultiCommon] Common006  label="cuts006"
  Shapes = -> [Extrude019,Extrude017]
FEATURE [Part::MultiFuse] Fusion060  label="keep001"
  Placement = pos=(0,0,4) rot=(0,0,1;0rad)
  Shapes = -> [Common006,Common005]
FEATURE [Part::MultiCommon] Common007  label="keeps001"
  Shapes = -> [Loft005,Fusion060]
FEATURE [Part::MultiFuse] Fusion061  label="shell"
  Shapes = -> [Cut004,Common007]
FEATURE [Part::Cut] Cut005  label="shell001-Legacy"
  Base = -> Fusion061
  Tool = -> Fusion059
FEATURE [Sketcher::SketchObject] Sketch051
  FullyConstrained = true
  sketch-geometry (4):
    g0: LineSegment StartX=0 StartY=275 StartZ=0 EndX=275 EndY=275 EndZ=0
    g1: LineSegment StartX=275 StartY=275 StartZ=0 EndX=275 EndY=0 EndZ=0
    g2: LineSegment StartX=275 StartY=0 StartZ=0 EndX=0 EndY=0 EndZ=0
    g3: LineSegment StartX=0 StartY=0 StartZ=0 EndX=0 EndY=275 EndZ=0
  constraints (11):
    c: Coincident(g0,g1)
    c: Coincident(g1,g2)
    c: Coincident(g2,g3)
    c: Coincident(g3,g0)
    c: Horizontal(g0)
    c: Horizontal(g2)
    c: Vertical(g1)
    c: Vertical(g3)
    c: Coincident(g2,g-1)
    c: DistanceX(g2,g2) = 275
    c: DistanceY(g3,g3) = 275
FEATURE [Sketcher::SketchObject] Sketch052
  FullyConstrained = true
  Placement = pos=(0,0,175.1) rot=(0,0,1;0rad)
  sketch-geometry (5):
    g0: GeomPoint X=137.5 Y=137.5 Z=0
    g1: LineSegment StartX=137.55 StartY=137.55 StartZ=0 EndX=137.55 EndY=137.45 EndZ=0
    g2: LineSegment StartX=137.55 StartY=137.45 StartZ=0 EndX=137.45 EndY=137.45 EndZ=0
    g3: LineSegment StartX=137.45 StartY=137.45 StartZ=0 EndX=137.45 EndY=137.55 EndZ=0
    g4: LineSegment StartX=137.45 StartY=137.55 StartZ=0 EndX=137.55 EndY=137.55 EndZ=0
  constraints (14):
    c: Coincident(g1,g2)
    c: Horizontal(g2)
    c: Vertical(g1)
    c: DistanceX(g2,g2) = 0.1
    c: DistanceX(g2,g0) = 0.05
    c: DistanceY(g1,g1) = 0.1
    c: DistanceY(g1,g0) = -0.05
    c: DistanceX(g0) = 137.5
    c: DistanceY(g0) = 137.5
    c: Coincident(g3,g2)
    c: Vertical(g3)
    c: Coincident(g4,g3)
    c: Coincident(g4,g1)
    c: Horizontal(g4)
FEATURE [Part::Loft] Loft008  label="outerLayer008"
  Closed = false
  MaxDegree = 5
  Ruled = false
  Sections = -> [Sketch051,Sketch052]
  Solid = true
FEATURE [Sketcher::SketchObject] Sketch053
  FullyConstrained = true
  sketch-geometry (4):
    g0: LineSegment StartX=0 StartY=275 StartZ=0 EndX=275 EndY=275 EndZ=0
    g1: LineSegment StartX=275 StartY=275 StartZ=0 EndX=275 EndY=0 EndZ=0
    g2: LineSegment StartX=275 StartY=0 StartZ=0 EndX=0 EndY=0 EndZ=0
    g3: LineSegment StartX=0 StartY=0 StartZ=0 EndX=0 EndY=275 EndZ=0
  constraints (11):
    c: Coincident(g0,g1)
    c: Coincident(g1,g2)
    c: Coincident(g2,g3)
    c: Coincident(g3,g0)
    c: Horizontal(g0)
    c: Horizontal(g2)
    c: Vertical(g1)
    c: Vertical(g3)
    c: Coincident(g2,g-1)
    c: DistanceX(g2,g2) = 275
    c: DistanceY(g3,g3) = 275
FEATURE [Sketcher::SketchObject] Sketch054
  FullyConstrained = true
  Placement = pos=(0,0,175.1) rot=(0,0,1;0rad)
  sketch-geometry (5):
    g0: GeomPoint X=137.5 Y=137.5 Z=0
    g1: LineSegment StartX=137.55 StartY=137.55 StartZ=0 EndX=137.55 EndY=137.45 EndZ=0
    g2: LineSegment StartX=137.55 StartY=137.45 StartZ=0 EndX=137.45 EndY=137.45 EndZ=0
    g3: LineSegment StartX=137.45 StartY=137.45 StartZ=0 EndX=137.45 EndY=137.55 EndZ=0
    g4: LineSegment StartX=137.45 StartY=137.55 StartZ=0 EndX=137.55 EndY=137.55 EndZ=0
  constraints (14):
    c: Coincident(g1,g2)
    c: Horizontal(g2)
    c: Vertical(g1)
    c: DistanceX(g2,g2) = 0.1
    c: DistanceX(g2,g0) = 0.05
    c: DistanceY(g1,g1) = 0.1
    c: DistanceY(g1,g0) = -0.05
    c: DistanceX(g0) = 137.5
    c: DistanceY(g0) = 137.5
    c: Coincident(g3,g2)
    c: Vertical(g3)
    c: Coincident(g4,g3)
    c: Coincident(g4,g1)
    c: Horizontal(g4)
FEATURE [Part::Loft] Loft009  label="outerLayer009"
  Closed = false
  MaxDegree = 5
  Placement = pos=(0,0,-8) rot=(0,0,1;0rad)
  Ruled = false
  Sections = -> [Sketch053,Sketch054]
  Solid = true
FEATURE [Part::Cut] Cut006  label="Shell002"
  Base = -> Loft008
  Tool = -> Loft009
FEATURE [Part::MultiCommon] Common008  label="keepLegacy"
  Shapes = -> [Fusion058,Cut006]
FEATURE [Sketcher::SketchObject] Sketch055
  FullyConstrained = true
  Placement = pos=(0,0,0) rot=(1,0,0;1.5708rad)
  sketch-geometry (28):
    g0: LineSegment StartX=50 StartY=70 StartZ=0 EndX=97.5 EndY=97.4241 EndZ=0
    g1: LineSegment StartX=97.5 StartY=97.4241 StartZ=0 EndX=97.5 EndY=101.424 EndZ=0
    g2: LineSegment StartX=97.5 StartY=101.424 StartZ=0 EndX=50 EndY=74 EndZ=0
    g3: LineSegment StartX=50 StartY=74 StartZ=0 EndX=50 EndY=70 EndZ=0
    g4: LineSegment StartX=50 StartY=82 StartZ=0 EndX=97.5 EndY=109.424 EndZ=0
    g5: LineSegment StartX=97.5 StartY=109.424 StartZ=0 EndX=97.5 EndY=105.424 EndZ=0
    g6: LineSegment StartX=97.5 StartY=105.424 StartZ=0 EndX=50 EndY=78 EndZ=0
    g7: LineSegment StartX=50 StartY=82 StartZ=0 EndX=50 EndY=78 EndZ=0
    g8: LineSegment StartX=75 StartY=116.424 StartZ=0 EndX=137.5 EndY=152.509 EndZ=0
    g9: LineSegment StartX=137.5 StartY=148.509 StartZ=0 EndX=75 EndY=112.424 EndZ=0
    g10: LineSegment StartX=75 StartY=112.424 StartZ=0 EndX=75 EndY=116.424 EndZ=0
    g11: LineSegment StartX=137.5 StartY=152.509 StartZ=0 EndX=200 EndY=116.424 EndZ=0
    g12: LineSegment StartX=200 StartY=116.424 StartZ=0 EndX=200 EndY=112.424 EndZ=0
    g13: LineSegment StartX=200 StartY=112.424 StartZ=0 EndX=137.5 EndY=148.509 EndZ=0
    g14: LineSegment StartX=177.5 StartY=109.424 StartZ=0 EndX=225 EndY=82 EndZ=0
    g15: LineSegment StartX=225 StartY=82 StartZ=0 EndX=225 EndY=78 EndZ=0
    g16: LineSegment StartX=225 StartY=78 StartZ=0 EndX=177.5 EndY=105.424 EndZ=0
    g17: LineSegment StartX=177.5 StartY=105.424 StartZ=0 EndX=177.5 EndY=109.424 EndZ=0
    g18: LineSegment StartX=177.5 StartY=101.424 StartZ=0 EndX=225 EndY=74 EndZ=0
    g19: LineSegment StartX=225 StartY=74 StartZ=0 EndX=225 EndY=70 EndZ=0
    g20: LineSegment StartX=225 StartY=70 StartZ=0 EndX=177.5 EndY=97.4241 EndZ=0
    g21: LineSegment StartX=177.5 StartY=101.424 StartZ=0 EndX=177.5 EndY=97.4241 EndZ=0
    g22: LineSegment StartX=75 StartY=120.424 StartZ=0 EndX=137.5 EndY=156.509 EndZ=0
    g23: LineSegment StartX=137.5 StartY=156.509 StartZ=0 EndX=200 EndY=120.424 EndZ=0
    g24: LineSegment StartX=200 StartY=120.424 StartZ=0 EndX=200 EndY=124.424 EndZ=0
    g25: LineSegment StartX=200 StartY=124.424 StartZ=0 EndX=137.5 EndY=160.509 EndZ=0
    g26: LineSegment StartX=137.5 StartY=160.509 StartZ=0 EndX=75 EndY=124.424 EndZ=0
    g27: LineSegment StartX=75 StartY=124.424 StartZ=0 EndX=75 EndY=120.424 EndZ=0
  constraints (84):
    c: Angle(g0) = 0.523599
    c: DistanceX(g0) = 50
    c: Coincident(g1,g0)
    c: Vertical(g1)
    c: Coincident(g2,g1)
    c: Coincident(g3,g2)
    c: Vertical(g3)
    c: DistanceY(g0,g2) = 4
    c: Parallel(g0,g2)
    c: Coincident(g0,g3)
    c: Coincident(g5,g4)
    c: Coincident(g7,g4)
    c: Coincident(g7,g6)
    c: Vertical(g7)
    c: Vertical(g5)
    c: Coincident(g5,g6)
    c: Parallel(g2,g6)
    c: Parallel(g6,g4)
    c: DistanceX(g6,g2) = 0
    c: DistanceY(g2,g6) = 4
    c: DistanceY(g6,g4) = 4
    c: DistanceX(g5,g1) = 0
    c: DistanceY(g0) = 70
    c: Coincident(g10,g9)
    c: Coincident(g10,g8)
    c: Vertical(g10)
    c: DistanceY(g9,g8) = 4
    c: Parallel(g8,g9)
    c: DistanceX(g9,g9) = 62.5
    c: Coincident(g11,g8)
    c: Coincident(g12,g11)
    c: Coincident(g13,g12)
    c: Coincident(g13,g9)
    c: Parallel(g13,g11)
    c: Vertical(g12)
    c: Coincident(g15,g14)
    c: Vertical(g15)
    c: Coincident(g17,g16)
    c: Coincident(g17,g14)
    c: Coincident(g19,g18)
    c: Vertical(g19)
    c: Coincident(g20,g19)
    c: Coincident(g21,g18)
    c: Coincident(g21,g20)
    c: Vertical(g21)
    c: Vertical(g17)
    c: DistanceX(g18,g16) = 0
    c: DistanceY(g16,g14) = 4
    c: DistanceY(g18,g16) = 4
    c: DistanceY(g20,g18) = 4
    c: Parallel(g20,g18)
    c: Parallel(g18,g16)
    c: Parallel(g16,g14)
    c: Coincident(g15,g16)
    c: DistanceY(g19,g0) = 0
    c: DistanceX(g18,g15) = 0
    c: DistanceY(g4,g9) = 3
    c: DistanceY(g4,g14) = 0
    c: DistanceY(g9,g12) = 0
    c: DistanceX(g9,g8) = 0
    c: Angle(g9) = -2.61799
    c: DistanceX(g9,g4) = 22.5
    c: DistanceX(g14,g12) = 22.5
    c: DistanceX(g9,g14) = 87.5
    c: DistanceX(g8) = 137.5
    c: DistanceX(g9,g12) = 125
    c: Coincident(g23,g22)
    c: Coincident(g24,g23)
    c: Vertical(g24)
    c: Coincident(g26,g25)
    c: Coincident(g27,g22)
    c: Vertical(g27)
    c: DistanceX(g22,g8) = 0
    c: DistanceX(g8,g22) = 0
    c: DistanceX(g25,g22) = 0
    c: Coincident(g24,g25)
    c: Coincident(g26,g27)
    c: DistanceY(g8,g22) = 4
    c: DistanceY(g22,g25) = 4
    c: DistanceY(g11,g23) = 4
    c: DistanceY(g23,g24) = 4
    c: DistanceX(g23,g11) = 0
    c: DistanceY(g8,g22) = 4
    c: DistanceY(g22,g26) = 4
FEATURE [Part::Extrusion] Extrude020  label="cuts011"
  Base = -> Sketch055
  Dir = (0,-1,2e-16)
  DirMode = 2
  FaceMakerClass = Part::FaceMakerBullseye
  LengthFwd = 275
  LengthRev = 0
  Reversed = true
  Solid = true
  Symmetric = false
FEATURE [Sketcher::SketchObject] Sketch056
  FullyConstrained = true
  Placement = pos=(0,0,0) rot=(1,0,0;1.5708rad)
  sketch-geometry (28):
    g0: LineSegment StartX=50 StartY=70 StartZ=0 EndX=97.5 EndY=97.4241 EndZ=0
    g1: LineSegment StartX=97.5 StartY=97.4241 StartZ=0 EndX=97.5 EndY=101.424 EndZ=0
    g2: LineSegment StartX=97.5 StartY=101.424 StartZ=0 EndX=50 EndY=74 EndZ=0
    g3: LineSegment StartX=50 StartY=74 StartZ=0 EndX=50 EndY=70 EndZ=0
    g4: LineSegment StartX=50 StartY=82 StartZ=0 EndX=97.5 EndY=109.424 EndZ=0
    g5: LineSegment StartX=97.5 StartY=109.424 StartZ=0 EndX=97.5 EndY=105.424 EndZ=0
    g6: LineSegment StartX=97.5 StartY=105.424 StartZ=0 EndX=50 EndY=78 EndZ=0
    g7: LineSegment StartX=50 StartY=82 StartZ=0 EndX=50 EndY=78 EndZ=0
    g8: LineSegment StartX=75 StartY=116.424 StartZ=0 EndX=137.5 EndY=152.509 EndZ=0
    g9: LineSegment StartX=137.5 StartY=148.509 StartZ=0 EndX=75 EndY=112.424 EndZ=0
    g10: LineSegment StartX=75 StartY=112.424 StartZ=0 EndX=75 EndY=116.424 EndZ=0
    g11: LineSegment StartX=137.5 StartY=152.509 StartZ=0 EndX=200 EndY=116.424 EndZ=0
    g12: LineSegment StartX=200 StartY=116.424 StartZ=0 EndX=200 EndY=112.424 EndZ=0
    g13: LineSegment StartX=200 StartY=112.424 StartZ=0 EndX=137.5 EndY=148.509 EndZ=0
    g14: LineSegment StartX=177.5 StartY=109.424 StartZ=0 EndX=225 EndY=82 EndZ=0
    g15: LineSegment StartX=225 StartY=82 StartZ=0 EndX=225 EndY=78 EndZ=0
    g16: LineSegment StartX=225 StartY=78 StartZ=0 EndX=177.5 EndY=105.424 EndZ=0
    g17: LineSegment StartX=177.5 StartY=105.424 StartZ=0 EndX=177.5 EndY=109.424 EndZ=0
    g18: LineSegment StartX=177.5 StartY=101.424 StartZ=0 EndX=225 EndY=74 EndZ=0
    g19: LineSegment StartX=225 StartY=74 StartZ=0 EndX=225 EndY=70 EndZ=0
    g20: LineSegment StartX=225 StartY=70 StartZ=0 EndX=177.5 EndY=97.4241 EndZ=0
    g21: LineSegment StartX=177.5 StartY=101.424 StartZ=0 EndX=177.5 EndY=97.4241 EndZ=0
    g22: LineSegment StartX=75 StartY=120.424 StartZ=0 EndX=75 EndY=124.424 EndZ=0
    g23: LineSegment StartX=75 StartY=124.424 StartZ=0 EndX=137.5 EndY=160.509 EndZ=0
    g24: LineSegment StartX=137.5 StartY=160.509 StartZ=0 EndX=200 EndY=124.424 EndZ=0
    g25: LineSegment StartX=200 StartY=124.424 StartZ=0 EndX=200 EndY=120.424 EndZ=0
    g26: LineSegment StartX=200 StartY=120.424 StartZ=0 EndX=137.5 EndY=156.509 EndZ=0
    g27: LineSegment StartX=137.5 StartY=156.509 StartZ=0 EndX=75 EndY=120.424 EndZ=0
  constraints (84):
    c: Angle(g0) = 0.523599
    c: DistanceX(g0) = 50
    c: Coincident(g1,g0)
    c: Vertical(g1)
    c: Coincident(g2,g1)
    c: Coincident(g3,g2)
    c: Vertical(g3)
    c: DistanceY(g0,g2) = 4
    c: Parallel(g0,g2)
    c: Coincident(g0,g3)
    c: Coincident(g5,g4)
    c: Coincident(g7,g4)
    c: Coincident(g7,g6)
    c: Vertical(g7)
    c: Vertical(g5)
    c: Coincident(g5,g6)
    c: Parallel(g2,g6)
    c: Parallel(g6,g4)
    c: DistanceX(g6,g2) = 0
    c: DistanceY(g2,g6) = 4
    c: DistanceY(g6,g4) = 4
    c: DistanceX(g5,g1) = 0
    c: DistanceY(g0) = 70
    c: Coincident(g10,g9)
    c: Coincident(g10,g8)
    c: Vertical(g10)
    c: DistanceY(g9,g8) = 4
    c: Parallel(g8,g9)
    c: DistanceX(g9,g9) = 62.5
    c: Coincident(g11,g8)
    c: Coincident(g12,g11)
    c: Coincident(g13,g12)
    c: Coincident(g13,g9)
    c: Parallel(g13,g11)
    c: Vertical(g12)
    c: Coincident(g15,g14)
    c: Vertical(g15)
    c: Coincident(g17,g16)
    c: Coincident(g17,g14)
    c: Coincident(g19,g18)
    c: Vertical(g19)
    c: Coincident(g20,g19)
    c: Coincident(g21,g18)
    c: Coincident(g21,g20)
    c: Vertical(g21)
    c: Vertical(g17)
    c: DistanceX(g18,g16) = 0
    c: DistanceY(g16,g14) = 4
    c: DistanceY(g18,g16) = 4
    c: DistanceY(g20,g18) = 4
    c: Parallel(g20,g18)
    c: Parallel(g18,g16)
    c: Parallel(g16,g14)
    c: Coincident(g15,g16)
    c: DistanceY(g19,g0) = 0
    c: DistanceX(g18,g15) = 0
    c: DistanceX(g14,g14) = 47.5
    c: DistanceX(g4,g4) = 47.5
    c: DistanceX(g4,g14) = 80
    c: Parallel(g9,g4)
    c: DistanceX(g9,g8) = 0
    c: DistanceY(g4,g9) = 3
    c: DistanceY(g14,g12) = 3
    c: DistanceY(g14,g4) = 0
    c: DistanceX(g8) = 137.5
    c: DistanceX(g9,g12) = 125
    c: Vertical(g22)
    c: Coincident(g23,g22)
    c: Coincident(g24,g23)
    c: Coincident(g25,g24)
    c: Vertical(g25)
    c: Coincident(g26,g25)
    c: Coincident(g27,g22)
    c: DistanceX(g22,g8) = 0
    c: DistanceY(g8,g22) = 4
    c: DistanceY(g22,g22) = 4
    c: Coincident(g26,g27)
    c: DistanceX(g26,g8) = 0
    c: DistanceY(g26,g23) = 4
    c: DistanceY(g8,g26) = 4
    c: DistanceX(g23,g26) = 0
    c: DistanceX(g25,g11) = 0
    c: DistanceY(g11,g25) = 4
    c: DistanceY(g25,g24) = 4
FEATURE [Part::Extrusion] Extrude021  label="cuts012"
  Base = -> Sketch056
  Dir = (0,-1,2e-16)
  DirMode = 2
  FaceMakerClass = Part::FaceMakerBullseye
  LengthFwd = 275
  LengthRev = 0
  Placement = pos=(275,0,0) rot=(0,0,1;1.5708rad)
  Reversed = true
  Solid = true
  Symmetric = false
FEATURE [Sketcher::SketchObject] Sketch057
  FullyConstrained = true
  Placement = pos=(0,0,0) rot=(1,0,0;1.5708rad)
  sketch-geometry (3):
    g0: LineSegment StartX=15 StartY=0 StartZ=0 EndX=260 EndY=0 EndZ=0
    g1: LineSegment StartX=260 StartY=0 StartZ=0 EndX=137.5 EndY=160 EndZ=0
    g2: LineSegment StartX=137.5 StartY=160 StartZ=0 EndX=15 EndY=0 EndZ=0
  constraints (9):
    c: Horizontal(g0)
    c: Coincident(g1,g0)
    c: Coincident(g2,g1)
    c: DistanceX(g0) = 260
    c: DistanceX(g1) = 137.5
    c: DistanceY(g1) = 160
    c: Coincident(g0,g2)
    c: DistanceY(g0,g-1) = 0
    c: DistanceX(g-1,g0) = 15
FEATURE [Part::Extrusion] Extrude022
  Base = -> Sketch057
  Dir = (0,-1,-6e-16)
  DirMode = 2
  FaceMakerClass = Part::FaceMakerBullseye
  LengthFwd = 275
  LengthRev = 0
  Placement = pos=(0,0,0) rot=(0,0,1;1.5708rad)
  Solid = true
  Symmetric = false
FEATURE [Part::MultiCommon] Common009  label="cuts009"
  Shapes = -> [Extrude022,Extrude020]
FEATURE [Sketcher::SketchObject] Sketch058
  FullyConstrained = true
  Placement = pos=(0,0,0) rot=(1,0,0;1.5708rad)
  sketch-geometry (3):
    g0: LineSegment StartX=15 StartY=0 StartZ=0 EndX=260 EndY=0 EndZ=0
    g1: LineSegment StartX=260 StartY=0 StartZ=0 EndX=137.5 EndY=160 EndZ=0
    g2: LineSegment StartX=137.5 StartY=160 StartZ=0 EndX=15 EndY=0 EndZ=0
  constraints (9):
    c: Horizontal(g0)
    c: Coincident(g1,g0)
    c: Coincident(g2,g1)
    c: DistanceX(g0) = 260
    c: DistanceX(g1) = 137.5
    c: DistanceY(g1) = 160
    c: Coincident(g0,g2)
    c: DistanceY(g0,g-1) = 0
    c: DistanceX(g-1,g0) = 15
FEATURE [Part::Extrusion] Extrude023
  Base = -> Sketch058
  Dir = (0,-1,2e-16)
  DirMode = 2
  FaceMakerClass = Part::FaceMakerBullseye
  LengthFwd = 275
  LengthRev = 0
  Reversed = true
  Solid = true
  Symmetric = false
FEATURE [Part::MultiCommon] Common010  label="cuts010"
  Shapes = -> [Extrude023,Extrude021]
FEATURE [Part::MultiFuse] Fusion062  label="cuts013"
  Shapes = -> [Common010,Common009]
FEATURE [Sketcher::SketchObject] Sketch059
  FullyConstrained = true
  sketch-geometry (4):
    g0: LineSegment StartX=0 StartY=275 StartZ=0 EndX=275 EndY=275 EndZ=0
    g1: LineSegment StartX=275 StartY=275 StartZ=0 EndX=275 EndY=0 EndZ=0
    g2: LineSegment StartX=275 StartY=0 StartZ=0 EndX=0 EndY=0 EndZ=0
    g3: LineSegment StartX=0 StartY=0 StartZ=0 EndX=0 EndY=275 EndZ=0
  constraints (11):
    c: Coincident(g0,g1)
    c: Coincident(g1,g2)
    c: Coincident(g2,g3)
    c: Coincident(g3,g0)
    c: Horizontal(g0)
    c: Horizontal(g2)
    c: Vertical(g1)
    c: Vertical(g3)
    c: Coincident(g2,g-1)
    c: DistanceX(g2,g2) = 275
    c: DistanceY(g3,g3) = 275
FEATURE [Sketcher::SketchObject] Sketch060
  FullyConstrained = true
  Placement = pos=(0,0,175.1) rot=(0,0,1;0rad)
  sketch-geometry (5):
    g0: GeomPoint X=137.5 Y=137.5 Z=0
    g1: LineSegment StartX=137.55 StartY=137.55 StartZ=0 EndX=137.55 EndY=137.45 EndZ=0
    g2: LineSegment StartX=137.55 StartY=137.45 StartZ=0 EndX=137.45 EndY=137.45 EndZ=0
    g3: LineSegment StartX=137.45 StartY=137.45 StartZ=0 EndX=137.45 EndY=137.55 EndZ=0
    g4: LineSegment StartX=137.45 StartY=137.55 StartZ=0 EndX=137.55 EndY=137.55 EndZ=0
  constraints (14):
    c: Coincident(g1,g2)
    c: Horizontal(g2)
    c: Vertical(g1)
    c: DistanceX(g2,g2) = 0.1
    c: DistanceX(g2,g0) = 0.05
    c: DistanceY(g1,g1) = 0.1
    c: DistanceY(g1,g0) = -0.05
    c: DistanceX(g0) = 137.5
    c: DistanceY(g0) = 137.5
    c: Coincident(g3,g2)
    c: Vertical(g3)
    c: Coincident(g4,g3)
    c: Coincident(g4,g1)
    c: Horizontal(g4)
FEATURE [Part::Loft] Loft010  label="outerLayer010"
  Closed = false
  MaxDegree = 5
  Ruled = false
  Sections = -> [Sketch059,Sketch060]
  Solid = true
FEATURE [Sketcher::SketchObject] Sketch061
  FullyConstrained = true
  sketch-geometry (4):
    g0: LineSegment StartX=0 StartY=275 StartZ=0 EndX=275 EndY=275 EndZ=0
    g1: LineSegment StartX=275 StartY=275 StartZ=0 EndX=275 EndY=0 EndZ=0
    g2: LineSegment StartX=275 StartY=0 StartZ=0 EndX=0 EndY=0 EndZ=0
    g3: LineSegment StartX=0 StartY=0 StartZ=0 EndX=0 EndY=275 EndZ=0
  constraints (11):
    c: Coincident(g0,g1)
    c: Coincident(g1,g2)
    c: Coincident(g2,g3)
    c: Coincident(g3,g0)
    c: Horizontal(g0)
    c: Horizontal(g2)
    c: Vertical(g1)
    c: Vertical(g3)
    c: Coincident(g2,g-1)
    c: DistanceX(g2,g2) = 275
    c: DistanceY(g3,g3) = 275
FEATURE [Sketcher::SketchObject] Sketch062
  FullyConstrained = true
  Placement = pos=(0,0,175.1) rot=(0,0,1;0rad)
  sketch-geometry (5):
    g0: GeomPoint X=137.5 Y=137.5 Z=0
    g1: LineSegment StartX=137.55 StartY=137.55 StartZ=0 EndX=137.55 EndY=137.45 EndZ=0
    g2: LineSegment StartX=137.55 StartY=137.45 StartZ=0 EndX=137.45 EndY=137.45 EndZ=0
    g3: LineSegment StartX=137.45 StartY=137.45 StartZ=0 EndX=137.45 EndY=137.55 EndZ=0
    g4: LineSegment StartX=137.45 StartY=137.55 StartZ=0 EndX=137.55 EndY=137.55 EndZ=0
  constraints (14):
    c: Coincident(g1,g2)
    c: Horizontal(g2)
    c: Vertical(g1)
    c: DistanceX(g2,g2) = 0.1
    c: DistanceX(g2,g0) = 0.05
    c: DistanceY(g1,g1) = 0.1
    c: DistanceY(g1,g0) = -0.05
    c: DistanceX(g0) = 137.5
    c: DistanceY(g0) = 137.5
    c: Coincident(g3,g2)
    c: Vertical(g3)
    c: Coincident(g4,g3)
    c: Coincident(g4,g1)
    c: Horizontal(g4)
FEATURE [Part::Loft] Loft011  label="outerLayer011"
  Closed = false
  MaxDegree = 5
  Ruled = false
  Sections = -> [Sketch061,Sketch062]
  Solid = true
FEATURE [Sketcher::SketchObject] Sketch063
  FullyConstrained = true
  sketch-geometry (4):
    g0: LineSegment StartX=0 StartY=275 StartZ=0 EndX=275 EndY=275 EndZ=0
    g1: LineSegment StartX=275 StartY=275 StartZ=0 EndX=275 EndY=0 EndZ=0
    g2: LineSegment StartX=275 StartY=0 StartZ=0 EndX=0 EndY=0 EndZ=0
    g3: LineSegment StartX=0 StartY=0 StartZ=0 EndX=0 EndY=275 EndZ=0
  constraints (11):
    c: Coincident(g0,g1)
    c: Coincident(g1,g2)
    c: Coincident(g2,g3)
    c: Coincident(g3,g0)
    c: Horizontal(g0)
    c: Horizontal(g2)
    c: Vertical(g1)
    c: Vertical(g3)
    c: Coincident(g2,g-1)
    c: DistanceX(g2,g2) = 275
    c: DistanceY(g3,g3) = 275
FEATURE [Sketcher::SketchObject] Sketch064
  FullyConstrained = true
  Placement = pos=(0,0,175.1) rot=(0,0,1;0rad)
  sketch-geometry (5):
    g0: GeomPoint X=137.5 Y=137.5 Z=0
    g1: LineSegment StartX=137.55 StartY=137.55 StartZ=0 EndX=137.55 EndY=137.45 EndZ=0
    g2: LineSegment StartX=137.55 StartY=137.45 StartZ=0 EndX=137.45 EndY=137.45 EndZ=0
    g3: LineSegment StartX=137.45 StartY=137.45 StartZ=0 EndX=137.45 EndY=137.55 EndZ=0
    g4: LineSegment StartX=137.45 StartY=137.55 StartZ=0 EndX=137.55 EndY=137.55 EndZ=0
  constraints (14):
    c: Coincident(g1,g2)
    c: Horizontal(g2)
    c: Vertical(g1)
    c: DistanceX(g2,g2) = 0.1
    c: DistanceX(g2,g0) = 0.05
    c: DistanceY(g1,g1) = 0.1
    c: DistanceY(g1,g0) = -0.05
    c: DistanceX(g0) = 137.5
    c: DistanceY(g0) = 137.5
    c: Coincident(g3,g2)
    c: Vertical(g3)
    c: Coincident(g4,g3)
    c: Coincident(g4,g1)
    c: Horizontal(g4)
FEATURE [Part::Loft] Loft012  label="outerLayer012"
  Closed = false
  MaxDegree = 5
  Placement = pos=(0,0,-8) rot=(0,0,1;0rad)
  Ruled = false
  Sections = -> [Sketch063,Sketch064]
  Solid = true
FEATURE [Part::Cut] Cut007  label="Shell003"
  Base = -> Loft011
  Tool = -> Loft012
FEATURE [Sketcher::SketchObject] Sketch065
  FullyConstrained = true
  Placement = pos=(0,0,0) rot=(1,0,0;1.5708rad)
  sketch-geometry (28):
    g0: LineSegment StartX=50 StartY=70 StartZ=0 EndX=97.5 EndY=97.4241 EndZ=0
    g1: LineSegment StartX=97.5 StartY=97.4241 StartZ=0 EndX=97.5 EndY=101.424 EndZ=0
    g2: LineSegment StartX=97.5 StartY=101.424 StartZ=0 EndX=50 EndY=74 EndZ=0
    g3: LineSegment StartX=50 StartY=74 StartZ=0 EndX=50 EndY=70 EndZ=0
    g4: LineSegment StartX=50 StartY=82 StartZ=0 EndX=97.5 EndY=109.424 EndZ=0
    g5: LineSegment StartX=97.5 StartY=109.424 StartZ=0 EndX=97.5 EndY=105.424 EndZ=0
    g6: LineSegment StartX=97.5 StartY=105.424 StartZ=0 EndX=50 EndY=78 EndZ=0
    g7: LineSegment StartX=50 StartY=82 StartZ=0 EndX=50 EndY=78 EndZ=0
    g8: LineSegment StartX=75 StartY=116.424 StartZ=0 EndX=137.5 EndY=152.509 EndZ=0
    g9: LineSegment StartX=137.5 StartY=148.509 StartZ=0 EndX=75 EndY=112.424 EndZ=0
    g10: LineSegment StartX=75 StartY=112.424 StartZ=0 EndX=75 EndY=116.424 EndZ=0
    g11: LineSegment StartX=137.5 StartY=152.509 StartZ=0 EndX=200 EndY=116.424 EndZ=0
    g12: LineSegment StartX=200 StartY=116.424 StartZ=0 EndX=200 EndY=112.424 EndZ=0
    g13: LineSegment StartX=200 StartY=112.424 StartZ=0 EndX=137.5 EndY=148.509 EndZ=0
    g14: LineSegment StartX=177.5 StartY=109.424 StartZ=0 EndX=225 EndY=82 EndZ=0
    g15: LineSegment StartX=225 StartY=82 StartZ=0 EndX=225 EndY=78 EndZ=0
    g16: LineSegment StartX=225 StartY=78 StartZ=0 EndX=177.5 EndY=105.424 EndZ=0
    g17: LineSegment StartX=177.5 StartY=105.424 StartZ=0 EndX=177.5 EndY=109.424 EndZ=0
    g18: LineSegment StartX=177.5 StartY=101.424 StartZ=0 EndX=225 EndY=74 EndZ=0
    g19: LineSegment StartX=225 StartY=74 StartZ=0 EndX=225 EndY=70 EndZ=0
    g20: LineSegment StartX=225 StartY=70 StartZ=0 EndX=177.5 EndY=97.4241 EndZ=0
    g21: LineSegment StartX=177.5 StartY=101.424 StartZ=0 EndX=177.5 EndY=97.4241 EndZ=0
    g22: LineSegment StartX=75 StartY=120.424 StartZ=0 EndX=137.5 EndY=156.509 EndZ=0
    g23: LineSegment StartX=137.5 StartY=156.509 StartZ=0 EndX=200 EndY=120.424 EndZ=0
    g24: LineSegment StartX=200 StartY=120.424 StartZ=0 EndX=200 EndY=124.424 EndZ=0
    g25: LineSegment StartX=200 StartY=124.424 StartZ=0 EndX=137.5 EndY=160.509 EndZ=0
    g26: LineSegment StartX=137.5 StartY=160.509 StartZ=0 EndX=75 EndY=124.424 EndZ=0
    g27: LineSegment StartX=75 StartY=124.424 StartZ=0 EndX=75 EndY=120.424 EndZ=0
  constraints (84):
    c: Angle(g0) = 0.523599
    c: DistanceX(g0) = 50
    c: Coincident(g1,g0)
    c: Vertical(g1)
    c: Coincident(g2,g1)
    c: Coincident(g3,g2)
    c: Vertical(g3)
    c: DistanceY(g0,g2) = 4
    c: Parallel(g0,g2)
    c: Coincident(g0,g3)
    c: Coincident(g5,g4)
    c: Coincident(g7,g4)
    c: Coincident(g7,g6)
    c: Vertical(g7)
    c: Vertical(g5)
    c: Coincident(g5,g6)
    c: Parallel(g2,g6)
    c: Parallel(g6,g4)
    c: DistanceX(g6,g2) = 0
    c: DistanceY(g2,g6) = 4
    c: DistanceY(g6,g4) = 4
    c: DistanceX(g5,g1) = 0
    c: DistanceY(g0) = 70
    c: Coincident(g10,g9)
    c: Coincident(g10,g8)
    c: Vertical(g10)
    c: DistanceY(g9,g8) = 4
    c: Parallel(g8,g9)
    c: DistanceX(g9,g9) = 62.5
    c: Coincident(g11,g8)
    c: Coincident(g12,g11)
    c: Coincident(g13,g12)
    c: Coincident(g13,g9)
    c: Parallel(g13,g11)
    c: Vertical(g12)
    c: Coincident(g15,g14)
    c: Vertical(g15)
    c: Coincident(g17,g16)
    c: Coincident(g17,g14)
    c: Coincident(g19,g18)
    c: Vertical(g19)
    c: Coincident(g20,g19)
    c: Coincident(g21,g18)
    c: Coincident(g21,g20)
    c: Vertical(g21)
    c: Vertical(g17)
    c: DistanceX(g18,g16) = 0
    c: DistanceY(g16,g14) = 4
    c: DistanceY(g18,g16) = 4
    c: DistanceY(g20,g18) = 4
    c: Parallel(g20,g18)
    c: Parallel(g18,g16)
    c: Parallel(g16,g14)
    c: Coincident(g15,g16)
    c: DistanceY(g19,g0) = 0
    c: DistanceX(g18,g15) = 0
    c: DistanceY(g4,g9) = 3
    c: DistanceY(g4,g14) = 0
    c: DistanceY(g9,g12) = 0
    c: DistanceX(g9,g8) = 0
    c: Angle(g9) = -2.61799
    c: DistanceX(g9,g4) = 22.5
    c: DistanceX(g14,g12) = 22.5
    c: DistanceX(g9,g14) = 87.5
    c: DistanceX(g8) = 137.5
    c: DistanceX(g9,g12) = 125
    c: Coincident(g23,g22)
    c: Coincident(g24,g23)
    c: Vertical(g24)
    c: Coincident(g26,g25)
    c: Coincident(g27,g22)
    c: Vertical(g27)
    c: DistanceX(g22,g8) = 0
    c: DistanceX(g8,g22) = 0
    c: DistanceX(g25,g22) = 0
    c: Coincident(g24,g25)
    c: Coincident(g26,g27)
    c: DistanceY(g8,g22) = 4
    c: DistanceY(g22,g25) = 4
    c: DistanceY(g11,g23) = 4
    c: DistanceY(g23,g24) = 4
    c: DistanceX(g23,g11) = 0
    c: DistanceY(g8,g22) = 4
    c: DistanceY(g22,g26) = 4
FEATURE [Part::Extrusion] Extrude024  label="cuts016"
  Base = -> Sketch065
  Dir = (0,-1,2e-16)
  DirMode = 2
  FaceMakerClass = Part::FaceMakerBullseye
  LengthFwd = 275
  LengthRev = 0
  Reversed = true
  Solid = true
  Symmetric = false
FEATURE [Sketcher::SketchObject] Sketch066
  FullyConstrained = true
  Placement = pos=(0,0,0) rot=(1,0,0;1.5708rad)
  sketch-geometry (28):
    g0: LineSegment StartX=50 StartY=70 StartZ=0 EndX=97.5 EndY=97.4241 EndZ=0
    g1: LineSegment StartX=97.5 StartY=97.4241 StartZ=0 EndX=97.5 EndY=101.424 EndZ=0
    g2: LineSegment StartX=97.5 StartY=101.424 StartZ=0 EndX=50 EndY=74 EndZ=0
    g3: LineSegment StartX=50 StartY=74 StartZ=0 EndX=50 EndY=70 EndZ=0
    g4: LineSegment StartX=50 StartY=82 StartZ=0 EndX=97.5 EndY=109.424 EndZ=0
    g5: LineSegment StartX=97.5 StartY=109.424 StartZ=0 EndX=97.5 EndY=105.424 EndZ=0
    g6: LineSegment StartX=97.5 StartY=105.424 StartZ=0 EndX=50 EndY=78 EndZ=0
    g7: LineSegment StartX=50 StartY=82 StartZ=0 EndX=50 EndY=78 EndZ=0
    g8: LineSegment StartX=75 StartY=116.424 StartZ=0 EndX=137.5 EndY=152.509 EndZ=0
    g9: LineSegment StartX=137.5 StartY=148.509 StartZ=0 EndX=75 EndY=112.424 EndZ=0
    g10: LineSegment StartX=75 StartY=112.424 StartZ=0 EndX=75 EndY=116.424 EndZ=0
    g11: LineSegment StartX=137.5 StartY=152.509 StartZ=0 EndX=200 EndY=116.424 EndZ=0
    g12: LineSegment StartX=200 StartY=116.424 StartZ=0 EndX=200 EndY=112.424 EndZ=0
    g13: LineSegment StartX=200 StartY=112.424 StartZ=0 EndX=137.5 EndY=148.509 EndZ=0
    g14: LineSegment StartX=177.5 StartY=109.424 StartZ=0 EndX=225 EndY=82 EndZ=0
    g15: LineSegment StartX=225 StartY=82 StartZ=0 EndX=225 EndY=78 EndZ=0
    g16: LineSegment StartX=225 StartY=78 StartZ=0 EndX=177.5 EndY=105.424 EndZ=0
    g17: LineSegment StartX=177.5 StartY=105.424 StartZ=0 EndX=177.5 EndY=109.424 EndZ=0
    g18: LineSegment StartX=177.5 StartY=101.424 StartZ=0 EndX=225 EndY=74 EndZ=0
    g19: LineSegment StartX=225 StartY=74 StartZ=0 EndX=225 EndY=70 EndZ=0
    g20: LineSegment StartX=225 StartY=70 StartZ=0 EndX=177.5 EndY=97.4241 EndZ=0
    g21: LineSegment StartX=177.5 StartY=101.424 StartZ=0 EndX=177.5 EndY=97.4241 EndZ=0
    g22: LineSegment StartX=75 StartY=120.424 StartZ=0 EndX=75 EndY=124.424 EndZ=0
    g23: LineSegment StartX=75 StartY=124.424 StartZ=0 EndX=137.5 EndY=160.509 EndZ=0
    g24: LineSegment StartX=137.5 StartY=160.509 StartZ=0 EndX=200 EndY=124.424 EndZ=0
    g25: LineSegment StartX=200 StartY=124.424 StartZ=0 EndX=200 EndY=120.424 EndZ=0
    g26: LineSegment StartX=200 StartY=120.424 StartZ=0 EndX=137.5 EndY=156.509 EndZ=0
    g27: LineSegment StartX=137.5 StartY=156.509 StartZ=0 EndX=75 EndY=120.424 EndZ=0
  constraints (84):
    c: Angle(g0) = 0.523599
    c: DistanceX(g0) = 50
    c: Coincident(g1,g0)
    c: Vertical(g1)
    c: Coincident(g2,g1)
    c: Coincident(g3,g2)
    c: Vertical(g3)
    c: DistanceY(g0,g2) = 4
    c: Parallel(g0,g2)
    c: Coincident(g0,g3)
    c: Coincident(g5,g4)
    c: Coincident(g7,g4)
    c: Coincident(g7,g6)
    c: Vertical(g7)
    c: Vertical(g5)
    c: Coincident(g5,g6)
    c: Parallel(g2,g6)
    c: Parallel(g6,g4)
    c: DistanceX(g6,g2) = 0
    c: DistanceY(g2,g6) = 4
    c: DistanceY(g6,g4) = 4
    c: DistanceX(g5,g1) = 0
    c: DistanceY(g0) = 70
    c: Coincident(g10,g9)
    c: Coincident(g10,g8)
    c: Vertical(g10)
    c: DistanceY(g9,g8) = 4
    c: Parallel(g8,g9)
    c: DistanceX(g9,g9) = 62.5
    c: Coincident(g11,g8)
    c: Coincident(g12,g11)
    c: Coincident(g13,g12)
    c: Coincident(g13,g9)
    c: Parallel(g13,g11)
    c: Vertical(g12)
    c: Coincident(g15,g14)
    c: Vertical(g15)
    c: Coincident(g17,g16)
    c: Coincident(g17,g14)
    c: Coincident(g19,g18)
    c: Vertical(g19)
    c: Coincident(g20,g19)
    c: Coincident(g21,g18)
    c: Coincident(g21,g20)
    c: Vertical(g21)
    c: Vertical(g17)
    c: DistanceX(g18,g16) = 0
    c: DistanceY(g16,g14) = 4
    c: DistanceY(g18,g16) = 4
    c: DistanceY(g20,g18) = 4
    c: Parallel(g20,g18)
    c: Parallel(g18,g16)
    c: Parallel(g16,g14)
    c: Coincident(g15,g16)
    c: DistanceY(g19,g0) = 0
    c: DistanceX(g18,g15) = 0
    c: DistanceX(g14,g14) = 47.5
    c: DistanceX(g4,g4) = 47.5
    c: DistanceX(g4,g14) = 80
    c: Parallel(g9,g4)
    c: DistanceX(g9,g8) = 0
    c: DistanceY(g4,g9) = 3
    c: DistanceY(g14,g12) = 3
    c: DistanceY(g14,g4) = 0
    c: DistanceX(g8) = 137.5
    c: DistanceX(g9,g12) = 125
    c: Vertical(g22)
    c: Coincident(g23,g22)
    c: Coincident(g24,g23)
    c: Coincident(g25,g24)
    c: Vertical(g25)
    c: Coincident(g26,g25)
    c: Coincident(g27,g22)
    c: DistanceX(g22,g8) = 0
    c: DistanceY(g8,g22) = 4
    c: DistanceY(g22,g22) = 4
    c: Coincident(g26,g27)
    c: DistanceX(g26,g8) = 0
    c: DistanceY(g26,g23) = 4
    c: DistanceY(g8,g26) = 4
    c: DistanceX(g23,g26) = 0
    c: DistanceX(g25,g11) = 0
    c: DistanceY(g11,g25) = 4
    c: DistanceY(g25,g24) = 4
FEATURE [Part::Extrusion] Extrude025  label="cuts017"
  Base = -> Sketch066
  Dir = (0,-1,2e-16)
  DirMode = 2
  FaceMakerClass = Part::FaceMakerBullseye
  LengthFwd = 275
  LengthRev = 0
  Placement = pos=(275,0,0) rot=(0,0,1;1.5708rad)
  Reversed = true
  Solid = true
  Symmetric = false
FEATURE [Sketcher::SketchObject] Sketch067
  FullyConstrained = true
  Placement = pos=(0,0,0) rot=(1,0,0;1.5708rad)
  sketch-geometry (3):
    g0: LineSegment StartX=15 StartY=0 StartZ=0 EndX=260 EndY=0 EndZ=0
    g1: LineSegment StartX=260 StartY=0 StartZ=0 EndX=137.5 EndY=160 EndZ=0
    g2: LineSegment StartX=137.5 StartY=160 StartZ=0 EndX=15 EndY=0 EndZ=0
  constraints (9):
    c: Horizontal(g0)
    c: Coincident(g1,g0)
    c: Coincident(g2,g1)
    c: DistanceX(g0) = 260
    c: DistanceX(g1) = 137.5
    c: DistanceY(g1) = 160
    c: Coincident(g0,g2)
    c: DistanceY(g0,g-1) = 0
    c: DistanceX(g-1,g0) = 15
FEATURE [Part::Extrusion] Extrude026
  Base = -> Sketch067
  Dir = (0,-1,-6e-16)
  DirMode = 2
  FaceMakerClass = Part::FaceMakerBullseye
  LengthFwd = 275
  LengthRev = 0
  Placement = pos=(0,0,0) rot=(0,0,1;1.5708rad)
  Solid = true
  Symmetric = false
FEATURE [Part::MultiCommon] Common011  label="cuts014"
  Shapes = -> [Extrude026,Extrude024]
FEATURE [Sketcher::SketchObject] Sketch068
  FullyConstrained = true
  Placement = pos=(0,0,0) rot=(1,0,0;1.5708rad)
  sketch-geometry (3):
    g0: LineSegment StartX=15 StartY=0 StartZ=0 EndX=260 EndY=0 EndZ=0
    g1: LineSegment StartX=260 StartY=0 StartZ=0 EndX=137.5 EndY=160 EndZ=0
    g2: LineSegment StartX=137.5 StartY=160 StartZ=0 EndX=15 EndY=0 EndZ=0
  constraints (9):
    c: Horizontal(g0)
    c: Coincident(g1,g0)
    c: Coincident(g2,g1)
    c: DistanceX(g0) = 260
    c: DistanceX(g1) = 137.5
    c: DistanceY(g1) = 160
    c: Coincident(g0,g2)
    c: DistanceY(g0,g-1) = 0
    c: DistanceX(g-1,g0) = 15
FEATURE [Part::Extrusion] Extrude027
  Base = -> Sketch068
  Dir = (0,-1,2e-16)
  DirMode = 2
  FaceMakerClass = Part::FaceMakerBullseye
  LengthFwd = 275
  LengthRev = 0
  Reversed = true
  Solid = true
  Symmetric = false
FEATURE [Part::MultiCommon] Common012  label="cuts015"
  Shapes = -> [Extrude027,Extrude025]
FEATURE [Part::MultiFuse] Fusion063  label="keep002"
  Placement = pos=(0,0,4) rot=(0,0,1;0rad)
  Shapes = -> [Common012,Common011]
FEATURE [Part::MultiCommon] Common013  label="keeps002"
  Shapes = -> [Loft010,Fusion063]
FEATURE [Part::MultiFuse] Fusion064  label="shell002"
  Shapes = -> [Cut007,Common013]
FEATURE [Part::MultiFuse] Fusion065  label="shellLegacy"
  Shapes = -> [Common008,Fusion064]
FEATURE [Part::Cut] Cut008  label="shellNow"
  Base = -> Fusion065
  Tool = -> Fusion062
FEATURE [Sketcher::SketchObject] Sketch069
  FullyConstrained = true
  sketch-geometry (4):
    g0: LineSegment StartX=0 StartY=275 StartZ=0 EndX=275 EndY=275 EndZ=0
    g1: LineSegment StartX=275 StartY=275 StartZ=0 EndX=275 EndY=0 EndZ=0
    g2: LineSegment StartX=275 StartY=0 StartZ=0 EndX=0 EndY=0 EndZ=0
    g3: LineSegment StartX=0 StartY=0 StartZ=0 EndX=0 EndY=275 EndZ=0
  constraints (11):
    c: Coincident(g0,g1)
    c: Coincident(g1,g2)
    c: Coincident(g2,g3)
    c: Coincident(g3,g0)
    c: Horizontal(g0)
    c: Horizontal(g2)
    c: Vertical(g1)
    c: Vertical(g3)
    c: Coincident(g2,g-1)
    c: DistanceX(g2,g2) = 275
    c: DistanceY(g3,g3) = 275
FEATURE [Sketcher::SketchObject] Sketch070
  FullyConstrained = true
  Placement = pos=(0,0,175.1) rot=(0,0,1;0rad)
  sketch-geometry (5):
    g0: GeomPoint X=137.5 Y=137.5 Z=0
    g1: LineSegment StartX=137.55 StartY=137.55 StartZ=0 EndX=137.55 EndY=137.45 EndZ=0
    g2: LineSegment StartX=137.55 StartY=137.45 StartZ=0 EndX=137.45 EndY=137.45 EndZ=0
    g3: LineSegment StartX=137.45 StartY=137.45 StartZ=0 EndX=137.45 EndY=137.55 EndZ=0
    g4: LineSegment StartX=137.45 StartY=137.55 StartZ=0 EndX=137.55 EndY=137.55 EndZ=0
  constraints (14):
    c: Coincident(g1,g2)
    c: Horizontal(g2)
    c: Vertical(g1)
    c: DistanceX(g2,g2) = 0.1
    c: DistanceX(g2,g0) = 0.05
    c: DistanceY(g1,g1) = 0.1
    c: DistanceY(g1,g0) = -0.05
    c: DistanceX(g0) = 137.5
    c: DistanceY(g0) = 137.5
    c: Coincident(g3,g2)
    c: Vertical(g3)
    c: Coincident(g4,g3)
    c: Coincident(g4,g1)
    c: Horizontal(g4)
FEATURE [Part::Loft] Loft013  label="outerLayer013"
  Closed = false
  MaxDegree = 5
  Ruled = false
  Sections = -> [Sketch069,Sketch070]
  Solid = true
FEATURE [Sketcher::SketchObject] Sketch071
  FullyConstrained = true
  sketch-geometry (4):
    g0: LineSegment StartX=0 StartY=275 StartZ=0 EndX=275 EndY=275 EndZ=0
    g1: LineSegment StartX=275 StartY=275 StartZ=0 EndX=275 EndY=0 EndZ=0
    g2: LineSegment StartX=275 StartY=0 StartZ=0 EndX=0 EndY=0 EndZ=0
    g3: LineSegment StartX=0 StartY=0 StartZ=0 EndX=0 EndY=275 EndZ=0
  constraints (11):
    c: Coincident(g0,g1)
    c: Coincident(g1,g2)
    c: Coincident(g2,g3)
    c: Coincident(g3,g0)
    c: Horizontal(g0)
    c: Horizontal(g2)
    c: Vertical(g1)
    c: Vertical(g3)
    c: Coincident(g2,g-1)
    c: DistanceX(g2,g2) = 275
    c: DistanceY(g3,g3) = 275
FEATURE [Sketcher::SketchObject] Sketch072
  FullyConstrained = true
  Placement = pos=(0,0,175.1) rot=(0,0,1;0rad)
  sketch-geometry (5):
    g0: GeomPoint X=137.5 Y=137.5 Z=0
    g1: LineSegment StartX=137.55 StartY=137.55 StartZ=0 EndX=137.55 EndY=137.45 EndZ=0
    g2: LineSegment StartX=137.55 StartY=137.45 StartZ=0 EndX=137.45 EndY=137.45 EndZ=0
    g3: LineSegment StartX=137.45 StartY=137.45 StartZ=0 EndX=137.45 EndY=137.55 EndZ=0
    g4: LineSegment StartX=137.45 StartY=137.55 StartZ=0 EndX=137.55 EndY=137.55 EndZ=0
  constraints (14):
    c: Coincident(g1,g2)
    c: Horizontal(g2)
    c: Vertical(g1)
    c: DistanceX(g2,g2) = 0.1
    c: DistanceX(g2,g0) = 0.05
    c: DistanceY(g1,g1) = 0.1
    c: DistanceY(g1,g0) = -0.05
    c: DistanceX(g0) = 137.5
    c: DistanceY(g0) = 137.5
    c: Coincident(g3,g2)
    c: Vertical(g3)
    c: Coincident(g4,g3)
    c: Coincident(g4,g1)
    c: Horizontal(g4)
FEATURE [Part::Loft] Loft014  label="outerLayer014"
  Closed = false
  MaxDegree = 5
  Placement = pos=(0,0,-4) rot=(0,0,1;0rad)
  Ruled = false
  Sections = -> [Sketch071,Sketch072]
  Solid = true
FEATURE [Part::Box] Box  label="Cube"
  AttacherType = Attacher::AttachEngine3D
  Height = 60
  Length = 275
  Width = 275
FEATURE [Part::Cut] Cut009  label="topLidKeep"
  Base = -> Loft013
  Tool = -> Box
FEATURE [Part::Box] Box001  label="Cube001"
  AttacherType = Attacher::AttachEngine3D
  Height = 64
  Length = 275
  Width = 275
FEATURE [Part::MultiCommon] Common014
  Shapes = -> [Loft014,Box001]
FEATURE [Part::Cut] Cut010  label="topShellKeep"
  Base = -> Cut009
  Tool = -> Common014
FEATURE [Part::MultiCommon] Common015  label="topShellKeep001"
  Shapes = -> [Cut008,Cut010]
FEATURE [Sketcher::SketchObject] Sketch073
  FullyConstrained = true
  sketch-geometry (4):
    g0: LineSegment StartX=0 StartY=275 StartZ=0 EndX=275 EndY=275 EndZ=0
    g1: LineSegment StartX=275 StartY=275 StartZ=0 EndX=275 EndY=0 EndZ=0
    g2: LineSegment StartX=275 StartY=0 StartZ=0 EndX=0 EndY=0 EndZ=0
    g3: LineSegment StartX=0 StartY=0 StartZ=0 EndX=0 EndY=275 EndZ=0
  constraints (11):
    c: Coincident(g0,g1)
    c: Coincident(g1,g2)
    c: Coincident(g2,g3)
    c: Coincident(g3,g0)
    c: Horizontal(g0)
    c: Horizontal(g2)
    c: Vertical(g1)
    c: Vertical(g3)
    c: Coincident(g2,g-1)
    c: DistanceX(g2,g2) = 275
    c: DistanceY(g3,g3) = 275
FEATURE [Sketcher::SketchObject] Sketch074
  FullyConstrained = true
  Placement = pos=(0,0,175.1) rot=(0,0,1;0rad)
  sketch-geometry (5):
    g0: GeomPoint X=137.5 Y=137.5 Z=0
    g1: LineSegment StartX=137.55 StartY=137.55 StartZ=0 EndX=137.55 EndY=137.45 EndZ=0
    g2: LineSegment StartX=137.55 StartY=137.45 StartZ=0 EndX=137.45 EndY=137.45 EndZ=0
    g3: LineSegment StartX=137.45 StartY=137.45 StartZ=0 EndX=137.45 EndY=137.55 EndZ=0
    g4: LineSegment StartX=137.45 StartY=137.55 StartZ=0 EndX=137.55 EndY=137.55 EndZ=0
  constraints (14):
    c: Coincident(g1,g2)
    c: Horizontal(g2)
    c: Vertical(g1)
    c: DistanceX(g2,g2) = 0.1
    c: DistanceX(g2,g0) = 0.05
    c: DistanceY(g1,g1) = 0.1
    c: DistanceY(g1,g0) = -0.05
    c: DistanceX(g0) = 137.5
    c: DistanceY(g0) = 137.5
    c: Coincident(g3,g2)
    c: Vertical(g3)
    c: Coincident(g4,g3)
    c: Coincident(g4,g1)
    c: Horizontal(g4)
FEATURE [Part::Loft] Loft015  label="outerLayer015"
  Closed = false
  MaxDegree = 5
  Ruled = false
  Sections = -> [Sketch073,Sketch074]
  Solid = true
FEATURE [Sketcher::SketchObject] Sketch075
  FullyConstrained = true
  sketch-geometry (4):
    g0: LineSegment StartX=0 StartY=275 StartZ=0 EndX=275 EndY=275 EndZ=0
    g1: LineSegment StartX=275 StartY=275 StartZ=0 EndX=275 EndY=0 EndZ=0
    g2: LineSegment StartX=275 StartY=0 StartZ=0 EndX=0 EndY=0 EndZ=0
    g3: LineSegment StartX=0 StartY=0 StartZ=0 EndX=0 EndY=275 EndZ=0
  constraints (11):
    c: Coincident(g0,g1)
    c: Coincident(g1,g2)
    c: Coincident(g2,g3)
    c: Coincident(g3,g0)
    c: Horizontal(g0)
    c: Horizontal(g2)
    c: Vertical(g1)
    c: Vertical(g3)
    c: Coincident(g2,g-1)
    c: DistanceX(g2,g2) = 275
    c: DistanceY(g3,g3) = 275
FEATURE [Sketcher::SketchObject] Sketch076
  FullyConstrained = true
  Placement = pos=(0,0,175.1) rot=(0,0,1;0rad)
  sketch-geometry (5):
    g0: GeomPoint X=137.5 Y=137.5 Z=0
    g1: LineSegment StartX=137.55 StartY=137.55 StartZ=0 EndX=137.55 EndY=137.45 EndZ=0
    g2: LineSegment StartX=137.55 StartY=137.45 StartZ=0 EndX=137.45 EndY=137.45 EndZ=0
    g3: LineSegment StartX=137.45 StartY=137.45 StartZ=0 EndX=137.45 EndY=137.55 EndZ=0
    g4: LineSegment StartX=137.45 StartY=137.55 StartZ=0 EndX=137.55 EndY=137.55 EndZ=0
  constraints (14):
    c: Coincident(g1,g2)
    c: Horizontal(g2)
    c: Vertical(g1)
    c: DistanceX(g2,g2) = 0.1
    c: DistanceX(g2,g0) = 0.05
    c: DistanceY(g1,g1) = 0.1
    c: DistanceY(g1,g0) = -0.05
    c: DistanceX(g0) = 137.5
    c: DistanceY(g0) = 137.5
    c: Coincident(g3,g2)
    c: Vertical(g3)
    c: Coincident(g4,g3)
    c: Coincident(g4,g1)
    c: Horizontal(g4)
FEATURE [Part::Loft] Loft016  label="outerLayer016"
  Closed = false
  MaxDegree = 5
  Placement = pos=(0,0,-4.25) rot=(0,0,1;0rad)
  Ruled = false
  Sections = -> [Sketch075,Sketch076]
  Solid = true
FEATURE [Part::Box] Box002  label="Cube002"
  AttacherType = Attacher::AttachEngine3D
  Height = 63.75
  Length = 275
  Width = 275
FEATURE [Part::MultiCommon] Common016
  Shapes = -> [Loft015,Box002]
FEATURE [Part::MultiCommon] Common017
  Shapes = -> [Cut,Common016]
FEATURE [Part::Box] Box003  label="Cube003"
  AttacherType = Attacher::AttachEngine3D
  Height = 3.75
  Length = 275
  Placement = pos=(0,0,59.75) rot=(0,0,1;0rad)
  Width = 275
FEATURE [Part::MultiCommon] Common018
  Shapes = -> [Loft016,Box003]
FEATURE [Part::Box] Box004  label="Cube004"
  AttacherType = Attacher::AttachEngine3D
  Height = 59.75
  Length = 275
  Width = 275
FEATURE [Part::MultiFuse] Fusion066
  Shapes = -> [Common018,Box004]
FEATURE [Part::MultiCommon] Common019  label="bottomShellKeep"
  Shapes = -> [Common017,Fusion066]
FEATURE [Part::Box] Box005  label="Cube005"
  AttacherType = Attacher::AttachEngine3D
  Height = 13
  Length = 67
  Placement = pos=(-20.5,-34,56) rot=(0,0,1;0rad)
  Width = 18
FEATURE [Part::Cylinder] Cylinder  label="Cylinder026"
  Angle = 360
  AttacherType = Attacher::AttachEngine3D
  FirstAngle = 0
  Height = 13
  Placement = pos=(-20.5,-25,56) rot=(0,0,1;0rad)
  Radius = 9
  SecondAngle = 0
FEATURE [Part::Cylinder] Cylinder026  label="antennaIn002"
  Angle = 360
  AttacherType = Attacher::AttachEngine3D
  FirstAngle = 0
  Height = 10
  Placement = pos=(-23,0,65) rot=(0,0,1;0rad)
  Radius = 3.25
  SecondAngle = 0
FEATURE [Part::Cylinder] Cylinder027  label="antennaIn003"
  Angle = 360
  AttacherType = Attacher::AttachEngine3D
  FirstAngle = 0
  Height = 10
  Placement = pos=(-23,0,69) rot=(0,0,1;0rad)
  Radius = 5.75
  SecondAngle = 0
FEATURE [Part::Cylinder] Cylinder028  label="antennaIn004"
  Angle = 360
  AttacherType = Attacher::AttachEngine3D
  FirstAngle = 0
  Height = 10
  Placement = pos=(-23,0,65) rot=(0,0,1;0rad)
  Radius = 3.25
  SecondAngle = 0
FEATURE [Part::Cylinder] Cylinder029  label="antennaIn005"
  Angle = 360
  AttacherType = Attacher::AttachEngine3D
  FirstAngle = 0
  Height = 10
  Placement = pos=(-23,0,69) rot=(0,0,1;0rad)
  Radius = 5.75
  SecondAngle = 0
FEATURE [Part::MultiFuse] Fusion067
  Placement = pos=(0,0,-1) rot=(0,0,1;0rad)
  Shapes = -> [Cylinder,Box005]
FEATURE [Part::MultiFuse] Fusion004
  Placement = pos=(2.5,-25,-6) rot=(0,0,1;0rad)
  Shapes = -> [Cylinder026,Cylinder027]
FEATURE [Part::MultiFuse] Fusion005
  Placement = pos=(2.5,-25,-19.5) rot=(0,0,1;0rad)
  Shapes = -> [Cylinder028,Cylinder029]
FEATURE [Part::MultiFuse] Fusion006  label="antennaCuts"
  Shapes = -> [Fusion004,Fusion005]
FEATURE [Part::Cut] Cut011  label="antennaHolder"
  Base = -> Fusion067
  Placement = pos=(162.5,175,95.5) rot=(0,0,-1;1.5708rad)
  Tool = -> Fusion006
FEATURE [Part::Feature] Part__Feature195  label="ANT-868-PW-QW-UFL-BODY002"
  shape: bbox 15.69 x 84 x 15.69 mm, 56 faces (baked)
FEATURE [Part::Feature] Part__Feature196  label="Screw002"
  Placement = pos=(0,-7.05,0) rot=(0,0,1;0rad)
  shape: bbox 7.002 x 7.052 x 7.002 mm, 20 faces (baked)
FEATURE [Part::Feature] Part__Feature197  label="Ring002"
  shape: bbox 9.2 x 6 x 9.2 mm, 8 faces, 2 solids (baked)
FEATURE [Part::Compound] Compound003  label="loraAntenna001"
  Links = -> [Part__Feature197,Part__Feature195,Part__Feature196]
  Placement = pos=(137.5,195.5,163.5) rot=(0.57735,-0.57735,-0.57735;2.0944rad)
FEATURE [Part::Box] Box006  label="Cube006"
  AttacherType = Attacher::AttachEngine3D
  Height = 50
  Length = 18
  Placement = pos=(128.5,175.75,113.5) rot=(0,0,1;0rad)
  Width = 10
FEATURE [Part::MultiFuse] Fusion068  label="antennaHolder001"
  Shapes = -> [Box006,Cut011]
FEATURE [Part::Feature] Part__Feature104  label="5862K227_Neodymium_Bottom_Leg005"
  Placement = pos=(30,30,-4) rot=(-1,0,0;1.5708rad)
  shape: bbox 13.75 x 13.75 x 6.35 mm, 14 faces (baked)
FEATURE [Part::Feature] Part__Feature105  label="91698A721_M3_MagnetScrew14mm_leg_1_Down001"
  Placement = pos=(30,30,-2) rot=(0,0,1;0rad)
  shape: bbox 5.601 x 5.601 x 14.23 mm, 86 faces (baked)
FEATURE [Part::Feature] Part__Feature106  label="91698A721_M3_MagnetScrew14mm_Leg1_Up001"
  Placement = pos=(30,30,2) rot=(0,1,0;3.14159rad)
  shape: bbox 5.601 x 5.601 x 14.23 mm, 86 faces (baked)
FEATURE [Part::Feature] Part__Feature107  label="94459A130_M3_HeatSetInserts_Down_Leg005"
  Placement = pos=(30,30,-10) rot=(1,0,0;1.5708rad)
  shape: bbox 4.74 x 4.749 x 4.466 mm, 209 faces (baked)
FEATURE [Part::Feature] Part__Feature108  label="5862K227_Magnet_Leg_1_Up001"
  Placement = pos=(30,30,4) rot=(-1,0,0;1.5708rad)
  shape: bbox 13.75 x 13.75 x 6.35 mm, 14 faces (baked)
FEATURE [Part::MultiFuse] Fusion023  label="coupledMagnetsV1-M3Large"
  Placement = pos=(107.5,55,81.25) rot=(0,0,1;0rad)
  Shapes = -> [Part__Feature104,Part__Feature105,Part__Feature106,Part__Feature107,Part__Feature108]
FEATURE [Part::Feature] Part__Feature198  label="5862K227_Neodymium_Bottom_Leg006"
  Placement = pos=(30,30,-4) rot=(-1,0,0;1.5708rad)
  shape: bbox 13.75 x 13.75 x 6.35 mm, 14 faces (baked)
FEATURE [Part::Feature] Part__Feature199  label="91698A721_M3_MagnetScrew14mm_leg_1_Down002"
  Placement = pos=(30,30,-2) rot=(0,0,1;0rad)
  shape: bbox 5.601 x 5.601 x 14.23 mm, 86 faces (baked)
FEATURE [Part::Feature] Part__Feature200  label="91698A721_M3_MagnetScrew14mm_Leg1_Up002"
  Placement = pos=(30,30,2) rot=(0,1,0;3.14159rad)
  shape: bbox 5.601 x 5.601 x 14.23 mm, 86 faces (baked)
FEATURE [Part::Feature] Part__Feature201  label="94459A130_M3_HeatSetInserts_Down_Leg006"
  Placement = pos=(30,30,-10) rot=(1,0,0;1.5708rad)
  shape: bbox 4.74 x 4.749 x 4.466 mm, 209 faces (baked)
FEATURE [Part::Feature] Part__Feature202  label="5862K227_Magnet_Leg_1_Up002"
  Placement = pos=(30,30,4) rot=(-1,0,0;1.5708rad)
  shape: bbox 13.75 x 13.75 x 6.35 mm, 14 faces (baked)
FEATURE [Part::MultiFuse] Fusion069  label="coupledMagnetsV1-M3Large001"
  Placement = pos=(55,107.5,81.25) rot=(0,0,1;0rad)
  Shapes = -> [Part__Feature198,Part__Feature199,Part__Feature200,Part__Feature201,Part__Feature202]
FEATURE [Part::Feature] Part__Feature208  label="5862K227_Neodymium_Bottom_Leg008"
  Placement = pos=(30,30,-4) rot=(-1,0,0;1.5708rad)
  shape: bbox 13.75 x 13.75 x 6.35 mm, 14 faces (baked)
FEATURE [Part::Feature] Part__Feature209  label="91698A721_M3_MagnetScrew14mm_leg_1_Down004"
  Placement = pos=(30,30,-2) rot=(0,0,1;0rad)
  shape: bbox 5.601 x 5.601 x 14.23 mm, 86 faces (baked)
FEATURE [Part::Feature] Part__Feature210  label="91698A721_M3_MagnetScrew14mm_Leg1_Up004"
  Placement = pos=(30,30,2) rot=(0,1,0;3.14159rad)
  shape: bbox 5.601 x 5.601 x 14.23 mm, 86 faces (baked)
FEATURE [Part::Feature] Part__Feature211  label="94459A130_M3_HeatSetInserts_Down_Leg008"
  Placement = pos=(30,30,-10) rot=(1,0,0;1.5708rad)
  shape: bbox 4.74 x 4.749 x 4.466 mm, 209 faces (baked)
FEATURE [Part::Feature] Part__Feature212  label="5862K227_Magnet_Leg_1_Up004"
  Placement = pos=(30,30,4) rot=(-1,0,0;1.5708rad)
  shape: bbox 13.75 x 13.75 x 6.35 mm, 14 faces (baked)
FEATURE [Part::MultiFuse] Fusion071  label="coupledMagnetsV1-M3Large003"
  Placement = pos=(160,107.5,81.25) rot=(0,0,1;0rad)
  Shapes = -> [Part__Feature208,Part__Feature209,Part__Feature210,Part__Feature211,Part__Feature212]
FEATURE [Part::Feature] Part__Feature213  label="5862K227_Neodymium_Bottom_Leg009"
  Placement = pos=(30,30,-4) rot=(-1,0,0;1.5708rad)
  shape: bbox 13.75 x 13.75 x 6.35 mm, 14 faces (baked)
FEATURE [Part::Feature] Part__Feature214  label="91698A721_M3_MagnetScrew14mm_leg_1_Down005"
  Placement = pos=(30,30,-2) rot=(0,0,1;0rad)
  shape: bbox 5.601 x 5.601 x 14.23 mm, 86 faces (baked)
FEATURE [Part::Feature] Part__Feature215  label="91698A721_M3_MagnetScrew14mm_Leg1_Up005"
  Placement = pos=(30,30,2) rot=(0,1,0;3.14159rad)
  shape: bbox 5.601 x 5.601 x 14.23 mm, 86 faces (baked)
FEATURE [Part::Feature] Part__Feature216  label="94459A130_M3_HeatSetInserts_Down_Leg009"
  Placement = pos=(30,30,-10) rot=(1,0,0;1.5708rad)
  shape: bbox 4.74 x 4.749 x 4.466 mm, 209 faces (baked)
FEATURE [Part::Feature] Part__Feature217  label="5862K227_Magnet_Leg_1_Up005"
  Placement = pos=(30,30,4) rot=(-1,0,0;1.5708rad)
  shape: bbox 13.75 x 13.75 x 6.35 mm, 14 faces (baked)
FEATURE [Part::MultiFuse] Fusion072  label="coupledMagnetsV1-M3Large004"
  Placement = pos=(107.5,160,81.25) rot=(0,0,1;0rad)
  Shapes = -> [Part__Feature213,Part__Feature214,Part__Feature215,Part__Feature216,Part__Feature217]
FEATURE [Part::MultiFuse] Fusion073  label="magnetMountsLevel1"
  Shapes = -> [Fusion023,Fusion069,Fusion071,Fusion072]
FEATURE [Sketcher::SketchObject] Sketch077
  FullyConstrained = true
  Placement = pos=(0,0,88.5) rot=(0,0,1;0rad)
  sketch-geometry (8):
    g0: Circle CenterX=85 CenterY=137.5 CenterZ=0 NormalX=0 NormalY=0 NormalZ=1 AngleXU=0 Radius=7.5
    g1: Circle CenterX=137.5 CenterY=85 CenterZ=0 NormalX=0 NormalY=0 NormalZ=1 AngleXU=0 Radius=7.5
    g2: Circle CenterX=190 CenterY=137.5 CenterZ=0 NormalX=0 NormalY=0 NormalZ=1 AngleXU=0 Radius=7.5
    g3: Circle CenterX=137.5 CenterY=190 CenterZ=0 NormalX=0 NormalY=0 NormalZ=1 AngleXU=0 Radius=7.5
    g4: Circle CenterX=85 CenterY=137.5 CenterZ=0 NormalX=0 NormalY=0 NormalZ=1 AngleXU=0 Radius=2
    g5: Circle CenterX=190 CenterY=137.5 CenterZ=0 NormalX=0 NormalY=0 NormalZ=1 AngleXU=0 Radius=2
    g6: Circle CenterX=137.5 CenterY=85 CenterZ=0 NormalX=0 NormalY=0 NormalZ=1 AngleXU=0 Radius=2
    g7: Circle CenterX=137.5 CenterY=190 CenterZ=0 NormalX=0 NormalY=0 NormalZ=1 AngleXU=0 Radius=2
  constraints (20):
    c: DistanceX(g-1,g1) = 137.5
    c: DistanceY(g-1,g1) = 85
    c: DistanceX(g0,g1) = 52.5
    c: DistanceX(g1,g2) = 52.5
    c: DistanceY(g0,g3) = 52.5
    c: DistanceX(g3,g1) = 0
    c: DistanceY(g2,g0) = 0
    c: DistanceY(g1,g0) = 52.5
    c: Equal(g3,g2)
    c: Equal(g3,g1)
    c: Equal(g3,g0)
    c: Diameter(g3) = 15
    c: Coincident(g4,g0)
    c: Coincident(g5,g2)
    c: Coincident(g6,g1)
    c: Coincident(g7,g3)
    c: Equal(g5,g6)
    c: Equal(g5,g4)
    c: Equal(g5,g7)
    c: Diameter(g5) = 4
FEATURE [Part::Extrusion] Extrude028
  Base = -> Sketch077
  Dir = (0,0,1)
  DirMode = 2
  FaceMakerClass = Part::FaceMakerBullseye
  LengthFwd = 25
  LengthRev = 0
  Solid = true
  Symmetric = false
FEATURE [Part::MultiCommon] Common020  label="magnetMountHolds"
  Shapes = -> [Loft,Extrude028]
FEATURE [Part::MultiFuse] Fusion074  label="topLid"
  Shapes = -> [Common020,Common015]
